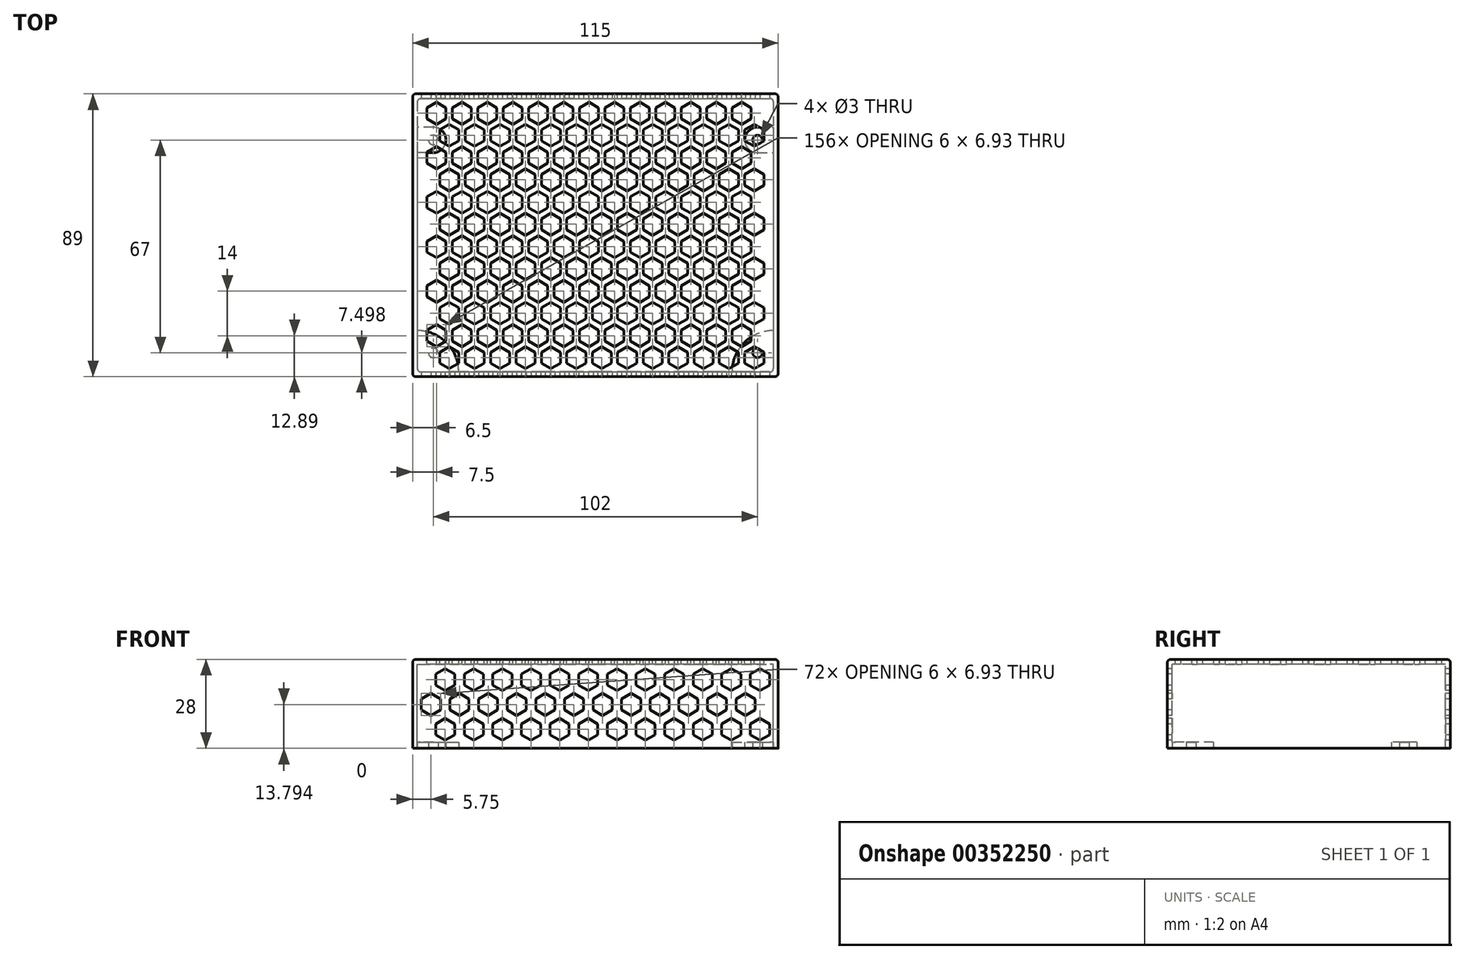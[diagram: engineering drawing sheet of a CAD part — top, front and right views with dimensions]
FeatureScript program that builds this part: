
annotation { "Feature Type Name" : "Feature", "Feature Type Description" : "" }
export const myFeature = defineFeature(function(context is Context, id is Id, definition is map)
    precondition{}
    {
        {
            var Q0;
            Q0=qCreatedBy(makeId("Top.planeOp"),FACE);
            var sketch = newSketch(context, id + "F0", { "sketchPlane" : qUnion([Q0])});
            skCircle(sketch, "E0.cCircle", {"center": v(-32, -14) * mm, "radius": 3 * mm, "construction": true});
            skLineSegment(sketch, "E0.0", {"start": v(-29, -15.73) * mm, "end": v(-32, -17.46) * mm});
            skLineSegment(sketch, "E0.1", {"start": v(-32, -17.46) * mm, "end": v(-35, -15.73) * mm});
            skLineSegment(sketch, "E0.2", {"start": v(-35, -15.73) * mm, "end": v(-35, -12.27) * mm});
            skLineSegment(sketch, "E0.3", {"start": v(-35, -12.27) * mm, "end": v(-32, -10.54) * mm});
            skLineSegment(sketch, "E0.4", {"start": v(-32, -10.54) * mm, "end": v(-29, -12.27) * mm});
            skLineSegment(sketch, "E0.5", {"start": v(-29, -12.27) * mm, "end": v(-29, -15.73) * mm});
            skPoint(sketch, "E0.0.midPoint", {"position": v(-30.5, -16.6) * mm});
            skCircle(sketch, "E1.cCircle", {"center": v(-28, -20.93) * mm, "radius": 3 * mm, "construction": true});
            skLineSegment(sketch, "E1.0", {"start": v(-25, -22.66) * mm, "end": v(-28, -24.4) * mm});
            skLineSegment(sketch, "E1.1", {"start": v(-28, -24.4) * mm, "end": v(-31, -22.66) * mm});
            skLineSegment(sketch, "E1.2", {"start": v(-31, -22.66) * mm, "end": v(-31, -19.2) * mm});
            skLineSegment(sketch, "E1.3", {"start": v(-31, -19.2) * mm, "end": v(-28, -17.46) * mm});
            skLineSegment(sketch, "E1.4", {"start": v(-28, -17.46) * mm, "end": v(-25, -19.2) * mm});
            skLineSegment(sketch, "E1.5", {"start": v(-25, -19.2) * mm, "end": v(-25, -22.66) * mm});
            skPoint(sketch, "E1.0.midPoint", {"position": v(-26.5, -23.53) * mm});
            skCircle(sketch, "E2.0.1.0", {"center": v(-28, -6.93) * mm, "radius": 3 * mm, "construction": true});
            skLineSegment(sketch, "E2.0.1.1", {"start": v(-28, -10.4) * mm, "end": v(-31, -8.66) * mm});
            skLineSegment(sketch, "E2.0.1.2", {"start": v(-31, -8.66) * mm, "end": v(-31, -5.2) * mm});
            skLineSegment(sketch, "E2.0.1.3", {"start": v(-31, -5.2) * mm, "end": v(-28, -3.46) * mm});
            skLineSegment(sketch, "E2.0.1.4", {"start": v(-28, -3.46) * mm, "end": v(-25, -5.2) * mm});
            skPoint(sketch, "E2.0.1.5", {"position": v(-26.5, -9.53) * mm});
            skPoint(sketch, "E2.0.1.6", {"position": v(-30.5, -2.6) * mm});
            skLineSegment(sketch, "E2.0.1.7", {"start": v(-25, -5.2) * mm, "end": v(-25, -8.66) * mm});
            skLineSegment(sketch, "E2.0.1.8", {"start": v(-29, 1.73) * mm, "end": v(-29, -1.73) * mm});
            skLineSegment(sketch, "E2.0.1.9", {"start": v(-32, 3.46) * mm, "end": v(-29, 1.73) * mm});
            skLineSegment(sketch, "E2.0.1.10", {"start": v(-35, 1.73) * mm, "end": v(-32, 3.46) * mm});
            skLineSegment(sketch, "E2.0.1.11", {"start": v(-35, -1.73) * mm, "end": v(-35, 1.73) * mm});
            skLineSegment(sketch, "E2.0.1.12", {"start": v(-32, -3.46) * mm, "end": v(-35, -1.73) * mm});
            skCircle(sketch, "E2.0.1.13", {"center": v(-32, 0) * mm, "radius": 3 * mm, "construction": true});
            skLineSegment(sketch, "E2.0.1.14", {"start": v(-25, -8.66) * mm, "end": v(-28, -10.4) * mm});
            skLineSegment(sketch, "E2.0.1.15", {"start": v(-29, -1.73) * mm, "end": v(-32, -3.46) * mm});
            skCircle(sketch, "E2.0.2.0", {"center": v(-28, 7.07) * mm, "radius": 3 * mm, "construction": true});
            skLineSegment(sketch, "E2.0.2.1", {"start": v(-28, 3.6) * mm, "end": v(-31, 5.34) * mm});
            skLineSegment(sketch, "E2.0.2.2", {"start": v(-31, 5.34) * mm, "end": v(-31, 8.8) * mm});
            skLineSegment(sketch, "E2.0.2.3", {"start": v(-31, 8.8) * mm, "end": v(-28, 10.54) * mm});
            skLineSegment(sketch, "E2.0.2.4", {"start": v(-28, 10.54) * mm, "end": v(-25, 8.8) * mm});
            skPoint(sketch, "E2.0.2.5", {"position": v(-26.5, 4.47) * mm});
            skPoint(sketch, "E2.0.2.6", {"position": v(-30.5, 11.4) * mm});
            skLineSegment(sketch, "E2.0.2.7", {"start": v(-25, 8.8) * mm, "end": v(-25, 5.34) * mm});
            skLineSegment(sketch, "E2.0.2.8", {"start": v(-29, 15.73) * mm, "end": v(-29, 12.27) * mm});
            skLineSegment(sketch, "E2.0.2.9", {"start": v(-32, 17.46) * mm, "end": v(-29, 15.73) * mm});
            skLineSegment(sketch, "E2.0.2.10", {"start": v(-35, 15.73) * mm, "end": v(-32, 17.46) * mm});
            skLineSegment(sketch, "E2.0.2.11", {"start": v(-35, 12.27) * mm, "end": v(-35, 15.73) * mm});
            skLineSegment(sketch, "E2.0.2.12", {"start": v(-32, 10.54) * mm, "end": v(-35, 12.27) * mm});
            skCircle(sketch, "E2.0.2.13", {"center": v(-32, 14) * mm, "radius": 3 * mm, "construction": true});
            skLineSegment(sketch, "E2.0.2.14", {"start": v(-25, 5.34) * mm, "end": v(-28, 3.6) * mm});
            skLineSegment(sketch, "E2.0.2.15", {"start": v(-29, 12.27) * mm, "end": v(-32, 10.54) * mm});
            skCircle(sketch, "E2.0.3.0", {"center": v(-28, 21.07) * mm, "radius": 3 * mm, "construction": true});
            skLineSegment(sketch, "E2.0.3.1", {"start": v(-28, 17.6) * mm, "end": v(-31, 19.34) * mm});
            skLineSegment(sketch, "E2.0.3.2", {"start": v(-31, 19.34) * mm, "end": v(-31, 22.8) * mm});
            skLineSegment(sketch, "E2.0.3.3", {"start": v(-31, 22.8) * mm, "end": v(-28, 24.54) * mm});
            skLineSegment(sketch, "E2.0.3.4", {"start": v(-28, 24.54) * mm, "end": v(-25, 22.8) * mm});
            skPoint(sketch, "E2.0.3.5", {"position": v(-26.5, 18.47) * mm});
            skPoint(sketch, "E2.0.3.6", {"position": v(-30.5, 25.4) * mm});
            skLineSegment(sketch, "E2.0.3.7", {"start": v(-25, 22.8) * mm, "end": v(-25, 19.34) * mm});
            skLineSegment(sketch, "E2.0.3.8", {"start": v(-29, 29.73) * mm, "end": v(-29, 26.27) * mm});
            skLineSegment(sketch, "E2.0.3.9", {"start": v(-32, 31.46) * mm, "end": v(-29, 29.73) * mm});
            skLineSegment(sketch, "E2.0.3.10", {"start": v(-35, 29.73) * mm, "end": v(-32, 31.46) * mm});
            skLineSegment(sketch, "E2.0.3.11", {"start": v(-35, 26.27) * mm, "end": v(-35, 29.73) * mm});
            skLineSegment(sketch, "E2.0.3.12", {"start": v(-32, 24.54) * mm, "end": v(-35, 26.27) * mm});
            skCircle(sketch, "E2.0.3.13", {"center": v(-32, 28) * mm, "radius": 3 * mm, "construction": true});
            skLineSegment(sketch, "E2.0.3.14", {"start": v(-25, 19.34) * mm, "end": v(-28, 17.6) * mm});
            skLineSegment(sketch, "E2.0.3.15", {"start": v(-29, 26.27) * mm, "end": v(-32, 24.54) * mm});
            skCircle(sketch, "E2.1.0.0", {"center": v(-20, -20.93) * mm, "radius": 3 * mm, "construction": true});
            skLineSegment(sketch, "E2.1.0.1", {"start": v(-20, -24.4) * mm, "end": v(-23, -22.66) * mm});
            skLineSegment(sketch, "E2.1.0.2", {"start": v(-23, -22.66) * mm, "end": v(-23, -19.2) * mm});
            skLineSegment(sketch, "E2.1.0.3", {"start": v(-23, -19.2) * mm, "end": v(-20, -17.46) * mm});
            skLineSegment(sketch, "E2.1.0.4", {"start": v(-20, -17.46) * mm, "end": v(-17, -19.2) * mm});
            skPoint(sketch, "E2.1.0.5", {"position": v(-18.5, -23.53) * mm});
            skPoint(sketch, "E2.1.0.6", {"position": v(-22.5, -16.6) * mm});
            skLineSegment(sketch, "E2.1.0.7", {"start": v(-17, -19.2) * mm, "end": v(-17, -22.66) * mm});
            skLineSegment(sketch, "E2.1.0.8", {"start": v(-21, -12.27) * mm, "end": v(-21, -15.73) * mm});
            skLineSegment(sketch, "E2.1.0.9", {"start": v(-24, -10.54) * mm, "end": v(-21, -12.27) * mm});
            skLineSegment(sketch, "E2.1.0.10", {"start": v(-27, -12.27) * mm, "end": v(-24, -10.54) * mm});
            skLineSegment(sketch, "E2.1.0.11", {"start": v(-27, -15.73) * mm, "end": v(-27, -12.27) * mm});
            skLineSegment(sketch, "E2.1.0.12", {"start": v(-24, -17.46) * mm, "end": v(-27, -15.73) * mm});
            skCircle(sketch, "E2.1.0.13", {"center": v(-24, -14) * mm, "radius": 3 * mm, "construction": true});
            skLineSegment(sketch, "E2.1.0.14", {"start": v(-17, -22.66) * mm, "end": v(-20, -24.4) * mm});
            skLineSegment(sketch, "E2.1.0.15", {"start": v(-21, -15.73) * mm, "end": v(-24, -17.46) * mm});
            skCircle(sketch, "E2.1.1.0", {"center": v(-20, -6.93) * mm, "radius": 3 * mm, "construction": true});
            skLineSegment(sketch, "E2.1.1.1", {"start": v(-20, -10.4) * mm, "end": v(-23, -8.66) * mm});
            skLineSegment(sketch, "E2.1.1.2", {"start": v(-23, -8.66) * mm, "end": v(-23, -5.2) * mm});
            skLineSegment(sketch, "E2.1.1.3", {"start": v(-23, -5.2) * mm, "end": v(-20, -3.46) * mm});
            skLineSegment(sketch, "E2.1.1.4", {"start": v(-20, -3.46) * mm, "end": v(-17, -5.2) * mm});
            skPoint(sketch, "E2.1.1.5", {"position": v(-18.5, -9.53) * mm});
            skPoint(sketch, "E2.1.1.6", {"position": v(-22.5, -2.6) * mm});
            skLineSegment(sketch, "E2.1.1.7", {"start": v(-17, -5.2) * mm, "end": v(-17, -8.66) * mm});
            skLineSegment(sketch, "E2.1.1.8", {"start": v(-21, 1.73) * mm, "end": v(-21, -1.73) * mm});
            skLineSegment(sketch, "E2.1.1.9", {"start": v(-24, 3.46) * mm, "end": v(-21, 1.73) * mm});
            skLineSegment(sketch, "E2.1.1.10", {"start": v(-27, 1.73) * mm, "end": v(-24, 3.46) * mm});
            skLineSegment(sketch, "E2.1.1.11", {"start": v(-27, -1.73) * mm, "end": v(-27, 1.73) * mm});
            skLineSegment(sketch, "E2.1.1.12", {"start": v(-24, -3.46) * mm, "end": v(-27, -1.73) * mm});
            skCircle(sketch, "E2.1.1.13", {"center": v(-24, 0) * mm, "radius": 3 * mm, "construction": true});
            skLineSegment(sketch, "E2.1.1.14", {"start": v(-17, -8.66) * mm, "end": v(-20, -10.4) * mm});
            skLineSegment(sketch, "E2.1.1.15", {"start": v(-21, -1.73) * mm, "end": v(-24, -3.46) * mm});
            skCircle(sketch, "E2.1.2.0", {"center": v(-20, 7.07) * mm, "radius": 3 * mm, "construction": true});
            skLineSegment(sketch, "E2.1.2.1", {"start": v(-20, 3.6) * mm, "end": v(-23, 5.34) * mm});
            skLineSegment(sketch, "E2.1.2.2", {"start": v(-23, 5.34) * mm, "end": v(-23, 8.8) * mm});
            skLineSegment(sketch, "E2.1.2.3", {"start": v(-23, 8.8) * mm, "end": v(-20, 10.54) * mm});
            skLineSegment(sketch, "E2.1.2.4", {"start": v(-20, 10.54) * mm, "end": v(-17, 8.8) * mm});
            skPoint(sketch, "E2.1.2.5", {"position": v(-18.5, 4.47) * mm});
            skPoint(sketch, "E2.1.2.6", {"position": v(-22.5, 11.4) * mm});
            skLineSegment(sketch, "E2.1.2.7", {"start": v(-17, 8.8) * mm, "end": v(-17, 5.34) * mm});
            skLineSegment(sketch, "E2.1.2.8", {"start": v(-21, 15.73) * mm, "end": v(-21, 12.27) * mm});
            skLineSegment(sketch, "E2.1.2.9", {"start": v(-24, 17.46) * mm, "end": v(-21, 15.73) * mm});
            skLineSegment(sketch, "E2.1.2.10", {"start": v(-27, 15.73) * mm, "end": v(-24, 17.46) * mm});
            skLineSegment(sketch, "E2.1.2.11", {"start": v(-27, 12.27) * mm, "end": v(-27, 15.73) * mm});
            skLineSegment(sketch, "E2.1.2.12", {"start": v(-24, 10.54) * mm, "end": v(-27, 12.27) * mm});
            skCircle(sketch, "E2.1.2.13", {"center": v(-24, 14) * mm, "radius": 3 * mm, "construction": true});
            skLineSegment(sketch, "E2.1.2.14", {"start": v(-17, 5.34) * mm, "end": v(-20, 3.6) * mm});
            skLineSegment(sketch, "E2.1.2.15", {"start": v(-21, 12.27) * mm, "end": v(-24, 10.54) * mm});
            skCircle(sketch, "E2.1.3.0", {"center": v(-20, 21.07) * mm, "radius": 3 * mm, "construction": true});
            skLineSegment(sketch, "E2.1.3.1", {"start": v(-20, 17.6) * mm, "end": v(-23, 19.34) * mm});
            skLineSegment(sketch, "E2.1.3.2", {"start": v(-23, 19.34) * mm, "end": v(-23, 22.8) * mm});
            skLineSegment(sketch, "E2.1.3.3", {"start": v(-23, 22.8) * mm, "end": v(-20, 24.54) * mm});
            skLineSegment(sketch, "E2.1.3.4", {"start": v(-20, 24.54) * mm, "end": v(-17, 22.8) * mm});
            skPoint(sketch, "E2.1.3.5", {"position": v(-18.5, 18.47) * mm});
            skPoint(sketch, "E2.1.3.6", {"position": v(-22.5, 25.4) * mm});
            skLineSegment(sketch, "E2.1.3.7", {"start": v(-17, 22.8) * mm, "end": v(-17, 19.34) * mm});
            skLineSegment(sketch, "E2.1.3.8", {"start": v(-21, 29.73) * mm, "end": v(-21, 26.27) * mm});
            skLineSegment(sketch, "E2.1.3.9", {"start": v(-24, 31.46) * mm, "end": v(-21, 29.73) * mm});
            skLineSegment(sketch, "E2.1.3.10", {"start": v(-27, 29.73) * mm, "end": v(-24, 31.46) * mm});
            skLineSegment(sketch, "E2.1.3.11", {"start": v(-27, 26.27) * mm, "end": v(-27, 29.73) * mm});
            skLineSegment(sketch, "E2.1.3.12", {"start": v(-24, 24.54) * mm, "end": v(-27, 26.27) * mm});
            skCircle(sketch, "E2.1.3.13", {"center": v(-24, 28) * mm, "radius": 3 * mm, "construction": true});
            skLineSegment(sketch, "E2.1.3.14", {"start": v(-17, 19.34) * mm, "end": v(-20, 17.6) * mm});
            skLineSegment(sketch, "E2.1.3.15", {"start": v(-21, 26.27) * mm, "end": v(-24, 24.54) * mm});
            skCircle(sketch, "E2.2.0.0", {"center": v(-12, -20.93) * mm, "radius": 3 * mm, "construction": true});
            skLineSegment(sketch, "E2.2.0.1", {"start": v(-12, -24.4) * mm, "end": v(-15, -22.66) * mm});
            skLineSegment(sketch, "E2.2.0.2", {"start": v(-15, -22.66) * mm, "end": v(-15, -19.2) * mm});
            skLineSegment(sketch, "E2.2.0.3", {"start": v(-15, -19.2) * mm, "end": v(-12, -17.46) * mm});
            skLineSegment(sketch, "E2.2.0.4", {"start": v(-12, -17.46) * mm, "end": v(-9, -19.2) * mm});
            skPoint(sketch, "E2.2.0.5", {"position": v(-10.5, -23.53) * mm});
            skPoint(sketch, "E2.2.0.6", {"position": v(-14.5, -16.6) * mm});
            skLineSegment(sketch, "E2.2.0.7", {"start": v(-9, -19.2) * mm, "end": v(-9, -22.66) * mm});
            skLineSegment(sketch, "E2.2.0.8", {"start": v(-13, -12.27) * mm, "end": v(-13, -15.73) * mm});
            skLineSegment(sketch, "E2.2.0.9", {"start": v(-16, -10.54) * mm, "end": v(-13, -12.27) * mm});
            skLineSegment(sketch, "E2.2.0.10", {"start": v(-19, -12.27) * mm, "end": v(-16, -10.54) * mm});
            skLineSegment(sketch, "E2.2.0.11", {"start": v(-19, -15.73) * mm, "end": v(-19, -12.27) * mm});
            skLineSegment(sketch, "E2.2.0.12", {"start": v(-16, -17.46) * mm, "end": v(-19, -15.73) * mm});
            skCircle(sketch, "E2.2.0.13", {"center": v(-16, -14) * mm, "radius": 3 * mm, "construction": true});
            skLineSegment(sketch, "E2.2.0.14", {"start": v(-9, -22.66) * mm, "end": v(-12, -24.4) * mm});
            skLineSegment(sketch, "E2.2.0.15", {"start": v(-13, -15.73) * mm, "end": v(-16, -17.46) * mm});
            skCircle(sketch, "E2.2.1.0", {"center": v(-12, -6.93) * mm, "radius": 3 * mm, "construction": true});
            skLineSegment(sketch, "E2.2.1.1", {"start": v(-12, -10.4) * mm, "end": v(-15, -8.66) * mm});
            skLineSegment(sketch, "E2.2.1.2", {"start": v(-15, -8.66) * mm, "end": v(-15, -5.2) * mm});
            skLineSegment(sketch, "E2.2.1.3", {"start": v(-15, -5.2) * mm, "end": v(-12, -3.46) * mm});
            skLineSegment(sketch, "E2.2.1.4", {"start": v(-12, -3.46) * mm, "end": v(-9, -5.2) * mm});
            skPoint(sketch, "E2.2.1.5", {"position": v(-10.5, -9.53) * mm});
            skPoint(sketch, "E2.2.1.6", {"position": v(-14.5, -2.6) * mm});
            skLineSegment(sketch, "E2.2.1.7", {"start": v(-9, -5.2) * mm, "end": v(-9, -8.66) * mm});
            skLineSegment(sketch, "E2.2.1.8", {"start": v(-13, 1.73) * mm, "end": v(-13, -1.73) * mm});
            skLineSegment(sketch, "E2.2.1.9", {"start": v(-16, 3.46) * mm, "end": v(-13, 1.73) * mm});
            skLineSegment(sketch, "E2.2.1.10", {"start": v(-19, 1.73) * mm, "end": v(-16, 3.46) * mm});
            skLineSegment(sketch, "E2.2.1.11", {"start": v(-19, -1.73) * mm, "end": v(-19, 1.73) * mm});
            skLineSegment(sketch, "E2.2.1.12", {"start": v(-16, -3.46) * mm, "end": v(-19, -1.73) * mm});
            skCircle(sketch, "E2.2.1.13", {"center": v(-16, 0) * mm, "radius": 3 * mm, "construction": true});
            skLineSegment(sketch, "E2.2.1.14", {"start": v(-9, -8.66) * mm, "end": v(-12, -10.4) * mm});
            skLineSegment(sketch, "E2.2.1.15", {"start": v(-13, -1.73) * mm, "end": v(-16, -3.46) * mm});
            skCircle(sketch, "E2.2.2.0", {"center": v(-12, 7.07) * mm, "radius": 3 * mm, "construction": true});
            skLineSegment(sketch, "E2.2.2.1", {"start": v(-12, 3.6) * mm, "end": v(-15, 5.34) * mm});
            skLineSegment(sketch, "E2.2.2.2", {"start": v(-15, 5.34) * mm, "end": v(-15, 8.8) * mm});
            skLineSegment(sketch, "E2.2.2.3", {"start": v(-15, 8.8) * mm, "end": v(-12, 10.54) * mm});
            skLineSegment(sketch, "E2.2.2.4", {"start": v(-12, 10.54) * mm, "end": v(-9, 8.8) * mm});
            skPoint(sketch, "E2.2.2.5", {"position": v(-10.5, 4.47) * mm});
            skPoint(sketch, "E2.2.2.6", {"position": v(-14.5, 11.4) * mm});
            skLineSegment(sketch, "E2.2.2.7", {"start": v(-9, 8.8) * mm, "end": v(-9, 5.34) * mm});
            skLineSegment(sketch, "E2.2.2.8", {"start": v(-13, 15.73) * mm, "end": v(-13, 12.27) * mm});
            skLineSegment(sketch, "E2.2.2.9", {"start": v(-16, 17.46) * mm, "end": v(-13, 15.73) * mm});
            skLineSegment(sketch, "E2.2.2.10", {"start": v(-19, 15.73) * mm, "end": v(-16, 17.46) * mm});
            skLineSegment(sketch, "E2.2.2.11", {"start": v(-19, 12.27) * mm, "end": v(-19, 15.73) * mm});
            skLineSegment(sketch, "E2.2.2.12", {"start": v(-16, 10.54) * mm, "end": v(-19, 12.27) * mm});
            skCircle(sketch, "E2.2.2.13", {"center": v(-16, 14) * mm, "radius": 3 * mm, "construction": true});
            skLineSegment(sketch, "E2.2.2.14", {"start": v(-9, 5.34) * mm, "end": v(-12, 3.6) * mm});
            skLineSegment(sketch, "E2.2.2.15", {"start": v(-13, 12.27) * mm, "end": v(-16, 10.54) * mm});
            skCircle(sketch, "E2.2.3.0", {"center": v(-12, 21.07) * mm, "radius": 3 * mm, "construction": true});
            skLineSegment(sketch, "E2.2.3.1", {"start": v(-12, 17.6) * mm, "end": v(-15, 19.34) * mm});
            skLineSegment(sketch, "E2.2.3.2", {"start": v(-15, 19.34) * mm, "end": v(-15, 22.8) * mm});
            skLineSegment(sketch, "E2.2.3.3", {"start": v(-15, 22.8) * mm, "end": v(-12, 24.54) * mm});
            skLineSegment(sketch, "E2.2.3.4", {"start": v(-12, 24.54) * mm, "end": v(-9, 22.8) * mm});
            skPoint(sketch, "E2.2.3.5", {"position": v(-10.5, 18.47) * mm});
            skPoint(sketch, "E2.2.3.6", {"position": v(-14.5, 25.4) * mm});
            skLineSegment(sketch, "E2.2.3.7", {"start": v(-9, 22.8) * mm, "end": v(-9, 19.34) * mm});
            skLineSegment(sketch, "E2.2.3.8", {"start": v(-13, 29.73) * mm, "end": v(-13, 26.27) * mm});
            skLineSegment(sketch, "E2.2.3.9", {"start": v(-16, 31.46) * mm, "end": v(-13, 29.73) * mm});
            skLineSegment(sketch, "E2.2.3.10", {"start": v(-19, 29.73) * mm, "end": v(-16, 31.46) * mm});
            skLineSegment(sketch, "E2.2.3.11", {"start": v(-19, 26.27) * mm, "end": v(-19, 29.73) * mm});
            skLineSegment(sketch, "E2.2.3.12", {"start": v(-16, 24.54) * mm, "end": v(-19, 26.27) * mm});
            skCircle(sketch, "E2.2.3.13", {"center": v(-16, 28) * mm, "radius": 3 * mm, "construction": true});
            skLineSegment(sketch, "E2.2.3.14", {"start": v(-9, 19.34) * mm, "end": v(-12, 17.6) * mm});
            skLineSegment(sketch, "E2.2.3.15", {"start": v(-13, 26.27) * mm, "end": v(-16, 24.54) * mm});
            skCircle(sketch, "E2.3.0.0", {"center": v(-4, -20.93) * mm, "radius": 3 * mm, "construction": true});
            skLineSegment(sketch, "E2.3.0.1", {"start": v(-4, -24.4) * mm, "end": v(-7, -22.66) * mm});
            skLineSegment(sketch, "E2.3.0.2", {"start": v(-7, -22.66) * mm, "end": v(-7, -19.2) * mm});
            skLineSegment(sketch, "E2.3.0.3", {"start": v(-7, -19.2) * mm, "end": v(-4, -17.46) * mm});
            skLineSegment(sketch, "E2.3.0.4", {"start": v(-4, -17.46) * mm, "end": v(-1, -19.2) * mm});
            skPoint(sketch, "E2.3.0.5", {"position": v(-2.5, -23.53) * mm});
            skPoint(sketch, "E2.3.0.6", {"position": v(-6.5, -16.6) * mm});
            skLineSegment(sketch, "E2.3.0.7", {"start": v(-1, -19.2) * mm, "end": v(-1, -22.66) * mm});
            skLineSegment(sketch, "E2.3.0.8", {"start": v(-5, -12.27) * mm, "end": v(-5, -15.73) * mm});
            skLineSegment(sketch, "E2.3.0.9", {"start": v(-8, -10.54) * mm, "end": v(-5, -12.27) * mm});
            skLineSegment(sketch, "E2.3.0.10", {"start": v(-11, -12.27) * mm, "end": v(-8, -10.54) * mm});
            skLineSegment(sketch, "E2.3.0.11", {"start": v(-11, -15.73) * mm, "end": v(-11, -12.27) * mm});
            skLineSegment(sketch, "E2.3.0.12", {"start": v(-8, -17.46) * mm, "end": v(-11, -15.73) * mm});
            skCircle(sketch, "E2.3.0.13", {"center": v(-8, -14) * mm, "radius": 3 * mm, "construction": true});
            skLineSegment(sketch, "E2.3.0.14", {"start": v(-1, -22.66) * mm, "end": v(-4, -24.4) * mm});
            skLineSegment(sketch, "E2.3.0.15", {"start": v(-5, -15.73) * mm, "end": v(-8, -17.46) * mm});
            skCircle(sketch, "E2.3.1.0", {"center": v(-4, -6.93) * mm, "radius": 3 * mm, "construction": true});
            skLineSegment(sketch, "E2.3.1.1", {"start": v(-4, -10.4) * mm, "end": v(-7, -8.66) * mm});
            skLineSegment(sketch, "E2.3.1.2", {"start": v(-7, -8.66) * mm, "end": v(-7, -5.2) * mm});
            skLineSegment(sketch, "E2.3.1.3", {"start": v(-7, -5.2) * mm, "end": v(-4, -3.46) * mm});
            skLineSegment(sketch, "E2.3.1.4", {"start": v(-4, -3.46) * mm, "end": v(-1, -5.2) * mm});
            skPoint(sketch, "E2.3.1.5", {"position": v(-2.5, -9.53) * mm});
            skPoint(sketch, "E2.3.1.6", {"position": v(-6.5, -2.6) * mm});
            skLineSegment(sketch, "E2.3.1.7", {"start": v(-1, -5.2) * mm, "end": v(-1, -8.66) * mm});
            skLineSegment(sketch, "E2.3.1.8", {"start": v(-5, 1.73) * mm, "end": v(-5, -1.73) * mm});
            skLineSegment(sketch, "E2.3.1.9", {"start": v(-8, 3.46) * mm, "end": v(-5, 1.73) * mm});
            skLineSegment(sketch, "E2.3.1.10", {"start": v(-11, 1.73) * mm, "end": v(-8, 3.46) * mm});
            skLineSegment(sketch, "E2.3.1.11", {"start": v(-11, -1.73) * mm, "end": v(-11, 1.73) * mm});
            skLineSegment(sketch, "E2.3.1.12", {"start": v(-8, -3.46) * mm, "end": v(-11, -1.73) * mm});
            skCircle(sketch, "E2.3.1.13", {"center": v(-8, 0) * mm, "radius": 3 * mm, "construction": true});
            skLineSegment(sketch, "E2.3.1.14", {"start": v(-1, -8.66) * mm, "end": v(-4, -10.4) * mm});
            skLineSegment(sketch, "E2.3.1.15", {"start": v(-5, -1.73) * mm, "end": v(-8, -3.46) * mm});
            skCircle(sketch, "E2.3.2.0", {"center": v(-4, 7.07) * mm, "radius": 3 * mm, "construction": true});
            skLineSegment(sketch, "E2.3.2.1", {"start": v(-4, 3.6) * mm, "end": v(-7, 5.34) * mm});
            skLineSegment(sketch, "E2.3.2.2", {"start": v(-7, 5.34) * mm, "end": v(-7, 8.8) * mm});
            skLineSegment(sketch, "E2.3.2.3", {"start": v(-7, 8.8) * mm, "end": v(-4, 10.54) * mm});
            skLineSegment(sketch, "E2.3.2.4", {"start": v(-4, 10.54) * mm, "end": v(-1, 8.8) * mm});
            skPoint(sketch, "E2.3.2.5", {"position": v(-2.5, 4.47) * mm});
            skPoint(sketch, "E2.3.2.6", {"position": v(-6.5, 11.4) * mm});
            skLineSegment(sketch, "E2.3.2.7", {"start": v(-1, 8.8) * mm, "end": v(-1, 5.34) * mm});
            skLineSegment(sketch, "E2.3.2.8", {"start": v(-5, 15.73) * mm, "end": v(-5, 12.27) * mm});
            skLineSegment(sketch, "E2.3.2.9", {"start": v(-8, 17.46) * mm, "end": v(-5, 15.73) * mm});
            skLineSegment(sketch, "E2.3.2.10", {"start": v(-11, 15.73) * mm, "end": v(-8, 17.46) * mm});
            skLineSegment(sketch, "E2.3.2.11", {"start": v(-11, 12.27) * mm, "end": v(-11, 15.73) * mm});
            skLineSegment(sketch, "E2.3.2.12", {"start": v(-8, 10.54) * mm, "end": v(-11, 12.27) * mm});
            skCircle(sketch, "E2.3.2.13", {"center": v(-8, 14) * mm, "radius": 3 * mm, "construction": true});
            skLineSegment(sketch, "E2.3.2.14", {"start": v(-1, 5.34) * mm, "end": v(-4, 3.6) * mm});
            skLineSegment(sketch, "E2.3.2.15", {"start": v(-5, 12.27) * mm, "end": v(-8, 10.54) * mm});
            skCircle(sketch, "E2.3.3.0", {"center": v(-4, 21.07) * mm, "radius": 3 * mm, "construction": true});
            skLineSegment(sketch, "E2.3.3.1", {"start": v(-4, 17.6) * mm, "end": v(-7, 19.34) * mm});
            skLineSegment(sketch, "E2.3.3.2", {"start": v(-7, 19.34) * mm, "end": v(-7, 22.8) * mm});
            skLineSegment(sketch, "E2.3.3.3", {"start": v(-7, 22.8) * mm, "end": v(-4, 24.54) * mm});
            skLineSegment(sketch, "E2.3.3.4", {"start": v(-4, 24.54) * mm, "end": v(-1, 22.8) * mm});
            skPoint(sketch, "E2.3.3.5", {"position": v(-2.5, 18.47) * mm});
            skPoint(sketch, "E2.3.3.6", {"position": v(-6.5, 25.4) * mm});
            skLineSegment(sketch, "E2.3.3.7", {"start": v(-1, 22.8) * mm, "end": v(-1, 19.34) * mm});
            skLineSegment(sketch, "E2.3.3.8", {"start": v(-5, 29.73) * mm, "end": v(-5, 26.27) * mm});
            skLineSegment(sketch, "E2.3.3.9", {"start": v(-8, 31.46) * mm, "end": v(-5, 29.73) * mm});
            skLineSegment(sketch, "E2.3.3.10", {"start": v(-11, 29.73) * mm, "end": v(-8, 31.46) * mm});
            skLineSegment(sketch, "E2.3.3.11", {"start": v(-11, 26.27) * mm, "end": v(-11, 29.73) * mm});
            skLineSegment(sketch, "E2.3.3.12", {"start": v(-8, 24.54) * mm, "end": v(-11, 26.27) * mm});
            skCircle(sketch, "E2.3.3.13", {"center": v(-8, 28) * mm, "radius": 3 * mm, "construction": true});
            skLineSegment(sketch, "E2.3.3.14", {"start": v(-1, 19.34) * mm, "end": v(-4, 17.6) * mm});
            skLineSegment(sketch, "E2.3.3.15", {"start": v(-5, 26.27) * mm, "end": v(-8, 24.54) * mm});
            skCircle(sketch, "E2.4.0.0", {"center": v(4, -20.93) * mm, "radius": 3 * mm, "construction": true});
            skLineSegment(sketch, "E2.4.0.1", {"start": v(4, -24.4) * mm, "end": v(1, -22.66) * mm});
            skLineSegment(sketch, "E2.4.0.2", {"start": v(1, -22.66) * mm, "end": v(1, -19.2) * mm});
            skLineSegment(sketch, "E2.4.0.3", {"start": v(1, -19.2) * mm, "end": v(4, -17.46) * mm});
            skLineSegment(sketch, "E2.4.0.4", {"start": v(4, -17.46) * mm, "end": v(7, -19.2) * mm});
            skPoint(sketch, "E2.4.0.5", {"position": v(5.5, -23.53) * mm});
            skPoint(sketch, "E2.4.0.6", {"position": v(1.5, -16.6) * mm});
            skLineSegment(sketch, "E2.4.0.7", {"start": v(7, -19.2) * mm, "end": v(7, -22.66) * mm});
            skLineSegment(sketch, "E2.4.0.8", {"start": v(3, -12.27) * mm, "end": v(3, -15.73) * mm});
            skLineSegment(sketch, "E2.4.0.9", {"start": v(0, -10.54) * mm, "end": v(3, -12.27) * mm});
            skLineSegment(sketch, "E2.4.0.10", {"start": v(-3, -12.27) * mm, "end": v(0, -10.54) * mm});
            skLineSegment(sketch, "E2.4.0.11", {"start": v(-3, -15.73) * mm, "end": v(-3, -12.27) * mm});
            skLineSegment(sketch, "E2.4.0.12", {"start": v(0, -17.46) * mm, "end": v(-3, -15.73) * mm});
            skCircle(sketch, "E2.4.0.13", {"center": v(0, -14) * mm, "radius": 3 * mm, "construction": true});
            skLineSegment(sketch, "E2.4.0.14", {"start": v(7, -22.66) * mm, "end": v(4, -24.4) * mm});
            skLineSegment(sketch, "E2.4.0.15", {"start": v(3, -15.73) * mm, "end": v(0, -17.46) * mm});
            skCircle(sketch, "E2.4.1.0", {"center": v(4, -6.93) * mm, "radius": 3 * mm, "construction": true});
            skLineSegment(sketch, "E2.4.1.1", {"start": v(4, -10.4) * mm, "end": v(1, -8.66) * mm});
            skLineSegment(sketch, "E2.4.1.2", {"start": v(1, -8.66) * mm, "end": v(1, -5.2) * mm});
            skLineSegment(sketch, "E2.4.1.3", {"start": v(1, -5.2) * mm, "end": v(4, -3.46) * mm});
            skLineSegment(sketch, "E2.4.1.4", {"start": v(4, -3.46) * mm, "end": v(7, -5.2) * mm});
            skPoint(sketch, "E2.4.1.5", {"position": v(5.5, -9.53) * mm});
            skPoint(sketch, "E2.4.1.6", {"position": v(1.5, -2.6) * mm});
            skLineSegment(sketch, "E2.4.1.7", {"start": v(7, -5.2) * mm, "end": v(7, -8.66) * mm});
            skLineSegment(sketch, "E2.4.1.8", {"start": v(3, 1.73) * mm, "end": v(3, -1.73) * mm});
            skLineSegment(sketch, "E2.4.1.9", {"start": v(0, 3.46) * mm, "end": v(3, 1.73) * mm});
            skLineSegment(sketch, "E2.4.1.10", {"start": v(-3, 1.73) * mm, "end": v(0, 3.46) * mm});
            skLineSegment(sketch, "E2.4.1.11", {"start": v(-3, -1.73) * mm, "end": v(-3, 1.73) * mm});
            skLineSegment(sketch, "E2.4.1.12", {"start": v(0, -3.46) * mm, "end": v(-3, -1.73) * mm});
            skCircle(sketch, "E2.4.1.13", {"center": v(0, 0) * mm, "radius": 3 * mm, "construction": true});
            skLineSegment(sketch, "E2.4.1.14", {"start": v(7, -8.66) * mm, "end": v(4, -10.4) * mm});
            skLineSegment(sketch, "E2.4.1.15", {"start": v(3, -1.73) * mm, "end": v(0, -3.46) * mm});
            skCircle(sketch, "E2.4.2.0", {"center": v(4, 7.07) * mm, "radius": 3 * mm, "construction": true});
            skLineSegment(sketch, "E2.4.2.1", {"start": v(4, 3.6) * mm, "end": v(1, 5.34) * mm});
            skLineSegment(sketch, "E2.4.2.2", {"start": v(1, 5.34) * mm, "end": v(1, 8.8) * mm});
            skLineSegment(sketch, "E2.4.2.3", {"start": v(1, 8.8) * mm, "end": v(4, 10.54) * mm});
            skLineSegment(sketch, "E2.4.2.4", {"start": v(4, 10.54) * mm, "end": v(7, 8.8) * mm});
            skPoint(sketch, "E2.4.2.5", {"position": v(5.5, 4.47) * mm});
            skPoint(sketch, "E2.4.2.6", {"position": v(1.5, 11.4) * mm});
            skLineSegment(sketch, "E2.4.2.7", {"start": v(7, 8.8) * mm, "end": v(7, 5.34) * mm});
            skLineSegment(sketch, "E2.4.2.8", {"start": v(3, 15.73) * mm, "end": v(3, 12.27) * mm});
            skLineSegment(sketch, "E2.4.2.9", {"start": v(0, 17.46) * mm, "end": v(3, 15.73) * mm});
            skLineSegment(sketch, "E2.4.2.10", {"start": v(-3, 15.73) * mm, "end": v(0, 17.46) * mm});
            skLineSegment(sketch, "E2.4.2.11", {"start": v(-3, 12.27) * mm, "end": v(-3, 15.73) * mm});
            skLineSegment(sketch, "E2.4.2.12", {"start": v(0, 10.54) * mm, "end": v(-3, 12.27) * mm});
            skCircle(sketch, "E2.4.2.13", {"center": v(0, 14) * mm, "radius": 3 * mm, "construction": true});
            skLineSegment(sketch, "E2.4.2.14", {"start": v(7, 5.34) * mm, "end": v(4, 3.6) * mm});
            skLineSegment(sketch, "E2.4.2.15", {"start": v(3, 12.27) * mm, "end": v(0, 10.54) * mm});
            skCircle(sketch, "E2.4.3.0", {"center": v(4, 21.07) * mm, "radius": 3 * mm, "construction": true});
            skLineSegment(sketch, "E2.4.3.1", {"start": v(4, 17.6) * mm, "end": v(1, 19.34) * mm});
            skLineSegment(sketch, "E2.4.3.2", {"start": v(1, 19.34) * mm, "end": v(1, 22.8) * mm});
            skLineSegment(sketch, "E2.4.3.3", {"start": v(1, 22.8) * mm, "end": v(4, 24.54) * mm});
            skLineSegment(sketch, "E2.4.3.4", {"start": v(4, 24.54) * mm, "end": v(7, 22.8) * mm});
            skPoint(sketch, "E2.4.3.5", {"position": v(5.5, 18.47) * mm});
            skPoint(sketch, "E2.4.3.6", {"position": v(1.5, 25.4) * mm});
            skLineSegment(sketch, "E2.4.3.7", {"start": v(7, 22.8) * mm, "end": v(7, 19.34) * mm});
            skLineSegment(sketch, "E2.4.3.8", {"start": v(3, 29.73) * mm, "end": v(3, 26.27) * mm});
            skLineSegment(sketch, "E2.4.3.9", {"start": v(0, 31.46) * mm, "end": v(3, 29.73) * mm});
            skLineSegment(sketch, "E2.4.3.10", {"start": v(-3, 29.73) * mm, "end": v(0, 31.46) * mm});
            skLineSegment(sketch, "E2.4.3.11", {"start": v(-3, 26.27) * mm, "end": v(-3, 29.73) * mm});
            skLineSegment(sketch, "E2.4.3.12", {"start": v(0, 24.54) * mm, "end": v(-3, 26.27) * mm});
            skCircle(sketch, "E2.4.3.13", {"center": v(0, 28) * mm, "radius": 3 * mm, "construction": true});
            skLineSegment(sketch, "E2.4.3.14", {"start": v(7, 19.34) * mm, "end": v(4, 17.6) * mm});
            skLineSegment(sketch, "E2.4.3.15", {"start": v(3, 26.27) * mm, "end": v(0, 24.54) * mm});
            skCircle(sketch, "E2.5.0.0", {"center": v(12, -20.93) * mm, "radius": 3 * mm, "construction": true});
            skLineSegment(sketch, "E2.5.0.1", {"start": v(12, -24.4) * mm, "end": v(9, -22.66) * mm});
            skLineSegment(sketch, "E2.5.0.2", {"start": v(9, -22.66) * mm, "end": v(9, -19.2) * mm});
            skLineSegment(sketch, "E2.5.0.3", {"start": v(9, -19.2) * mm, "end": v(12, -17.46) * mm});
            skLineSegment(sketch, "E2.5.0.4", {"start": v(12, -17.46) * mm, "end": v(15, -19.2) * mm});
            skPoint(sketch, "E2.5.0.5", {"position": v(13.5, -23.53) * mm});
            skPoint(sketch, "E2.5.0.6", {"position": v(9.5, -16.6) * mm});
            skLineSegment(sketch, "E2.5.0.7", {"start": v(15, -19.2) * mm, "end": v(15, -22.66) * mm});
            skLineSegment(sketch, "E2.5.0.8", {"start": v(11, -12.27) * mm, "end": v(11, -15.73) * mm});
            skLineSegment(sketch, "E2.5.0.9", {"start": v(8, -10.54) * mm, "end": v(11, -12.27) * mm});
            skLineSegment(sketch, "E2.5.0.10", {"start": v(5, -12.27) * mm, "end": v(8, -10.54) * mm});
            skLineSegment(sketch, "E2.5.0.11", {"start": v(5, -15.73) * mm, "end": v(5, -12.27) * mm});
            skLineSegment(sketch, "E2.5.0.12", {"start": v(8, -17.46) * mm, "end": v(5, -15.73) * mm});
            skCircle(sketch, "E2.5.0.13", {"center": v(8, -14) * mm, "radius": 3 * mm, "construction": true});
            skLineSegment(sketch, "E2.5.0.14", {"start": v(15, -22.66) * mm, "end": v(12, -24.4) * mm});
            skLineSegment(sketch, "E2.5.0.15", {"start": v(11, -15.73) * mm, "end": v(8, -17.46) * mm});
            skCircle(sketch, "E2.5.1.0", {"center": v(12, -6.93) * mm, "radius": 3 * mm, "construction": true});
            skLineSegment(sketch, "E2.5.1.1", {"start": v(12, -10.4) * mm, "end": v(9, -8.66) * mm});
            skLineSegment(sketch, "E2.5.1.2", {"start": v(9, -8.66) * mm, "end": v(9, -5.2) * mm});
            skLineSegment(sketch, "E2.5.1.3", {"start": v(9, -5.2) * mm, "end": v(12, -3.46) * mm});
            skLineSegment(sketch, "E2.5.1.4", {"start": v(12, -3.46) * mm, "end": v(15, -5.2) * mm});
            skPoint(sketch, "E2.5.1.5", {"position": v(13.5, -9.53) * mm});
            skPoint(sketch, "E2.5.1.6", {"position": v(9.5, -2.6) * mm});
            skLineSegment(sketch, "E2.5.1.7", {"start": v(15, -5.2) * mm, "end": v(15, -8.66) * mm});
            skLineSegment(sketch, "E2.5.1.8", {"start": v(11, 1.73) * mm, "end": v(11, -1.73) * mm});
            skLineSegment(sketch, "E2.5.1.9", {"start": v(8, 3.46) * mm, "end": v(11, 1.73) * mm});
            skLineSegment(sketch, "E2.5.1.10", {"start": v(5, 1.73) * mm, "end": v(8, 3.46) * mm});
            skLineSegment(sketch, "E2.5.1.11", {"start": v(5, -1.73) * mm, "end": v(5, 1.73) * mm});
            skLineSegment(sketch, "E2.5.1.12", {"start": v(8, -3.46) * mm, "end": v(5, -1.73) * mm});
            skCircle(sketch, "E2.5.1.13", {"center": v(8, 0) * mm, "radius": 3 * mm, "construction": true});
            skLineSegment(sketch, "E2.5.1.14", {"start": v(15, -8.66) * mm, "end": v(12, -10.4) * mm});
            skLineSegment(sketch, "E2.5.1.15", {"start": v(11, -1.73) * mm, "end": v(8, -3.46) * mm});
            skCircle(sketch, "E2.5.2.0", {"center": v(12, 7.07) * mm, "radius": 3 * mm, "construction": true});
            skLineSegment(sketch, "E2.5.2.1", {"start": v(12, 3.6) * mm, "end": v(9, 5.34) * mm});
            skLineSegment(sketch, "E2.5.2.2", {"start": v(9, 5.34) * mm, "end": v(9, 8.8) * mm});
            skLineSegment(sketch, "E2.5.2.3", {"start": v(9, 8.8) * mm, "end": v(12, 10.54) * mm});
            skLineSegment(sketch, "E2.5.2.4", {"start": v(12, 10.54) * mm, "end": v(15, 8.8) * mm});
            skPoint(sketch, "E2.5.2.5", {"position": v(13.5, 4.47) * mm});
            skPoint(sketch, "E2.5.2.6", {"position": v(9.5, 11.4) * mm});
            skLineSegment(sketch, "E2.5.2.7", {"start": v(15, 8.8) * mm, "end": v(15, 5.34) * mm});
            skLineSegment(sketch, "E2.5.2.8", {"start": v(11, 15.73) * mm, "end": v(11, 12.27) * mm});
            skLineSegment(sketch, "E2.5.2.9", {"start": v(8, 17.46) * mm, "end": v(11, 15.73) * mm});
            skLineSegment(sketch, "E2.5.2.10", {"start": v(5, 15.73) * mm, "end": v(8, 17.46) * mm});
            skLineSegment(sketch, "E2.5.2.11", {"start": v(5, 12.27) * mm, "end": v(5, 15.73) * mm});
            skLineSegment(sketch, "E2.5.2.12", {"start": v(8, 10.54) * mm, "end": v(5, 12.27) * mm});
            skCircle(sketch, "E2.5.2.13", {"center": v(8, 14) * mm, "radius": 3 * mm, "construction": true});
            skLineSegment(sketch, "E2.5.2.14", {"start": v(15, 5.34) * mm, "end": v(12, 3.6) * mm});
            skLineSegment(sketch, "E2.5.2.15", {"start": v(11, 12.27) * mm, "end": v(8, 10.54) * mm});
            skCircle(sketch, "E2.5.3.0", {"center": v(12, 21.07) * mm, "radius": 3 * mm, "construction": true});
            skLineSegment(sketch, "E2.5.3.1", {"start": v(12, 17.6) * mm, "end": v(9, 19.34) * mm});
            skLineSegment(sketch, "E2.5.3.2", {"start": v(9, 19.34) * mm, "end": v(9, 22.8) * mm});
            skLineSegment(sketch, "E2.5.3.3", {"start": v(9, 22.8) * mm, "end": v(12, 24.54) * mm});
            skLineSegment(sketch, "E2.5.3.4", {"start": v(12, 24.54) * mm, "end": v(15, 22.8) * mm});
            skPoint(sketch, "E2.5.3.5", {"position": v(13.5, 18.47) * mm});
            skPoint(sketch, "E2.5.3.6", {"position": v(9.5, 25.4) * mm});
            skLineSegment(sketch, "E2.5.3.7", {"start": v(15, 22.8) * mm, "end": v(15, 19.34) * mm});
            skLineSegment(sketch, "E2.5.3.8", {"start": v(11, 29.73) * mm, "end": v(11, 26.27) * mm});
            skLineSegment(sketch, "E2.5.3.9", {"start": v(8, 31.46) * mm, "end": v(11, 29.73) * mm});
            skLineSegment(sketch, "E2.5.3.10", {"start": v(5, 29.73) * mm, "end": v(8, 31.46) * mm});
            skLineSegment(sketch, "E2.5.3.11", {"start": v(5, 26.27) * mm, "end": v(5, 29.73) * mm});
            skLineSegment(sketch, "E2.5.3.12", {"start": v(8, 24.54) * mm, "end": v(5, 26.27) * mm});
            skCircle(sketch, "E2.5.3.13", {"center": v(8, 28) * mm, "radius": 3 * mm, "construction": true});
            skLineSegment(sketch, "E2.5.3.14", {"start": v(15, 19.34) * mm, "end": v(12, 17.6) * mm});
            skLineSegment(sketch, "E2.5.3.15", {"start": v(11, 26.27) * mm, "end": v(8, 24.54) * mm});
            skCircle(sketch, "E2.6.0.0", {"center": v(20, -20.93) * mm, "radius": 3 * mm, "construction": true});
            skLineSegment(sketch, "E2.6.0.1", {"start": v(20, -24.4) * mm, "end": v(17, -22.66) * mm});
            skLineSegment(sketch, "E2.6.0.2", {"start": v(17, -22.66) * mm, "end": v(17, -19.2) * mm});
            skLineSegment(sketch, "E2.6.0.3", {"start": v(17, -19.2) * mm, "end": v(20, -17.46) * mm});
            skLineSegment(sketch, "E2.6.0.4", {"start": v(20, -17.46) * mm, "end": v(23, -19.2) * mm});
            skPoint(sketch, "E2.6.0.5", {"position": v(21.5, -23.53) * mm});
            skPoint(sketch, "E2.6.0.6", {"position": v(17.5, -16.6) * mm});
            skLineSegment(sketch, "E2.6.0.7", {"start": v(23, -19.2) * mm, "end": v(23, -22.66) * mm});
            skLineSegment(sketch, "E2.6.0.8", {"start": v(19, -12.27) * mm, "end": v(19, -15.73) * mm});
            skLineSegment(sketch, "E2.6.0.9", {"start": v(16, -10.54) * mm, "end": v(19, -12.27) * mm});
            skLineSegment(sketch, "E2.6.0.10", {"start": v(13, -12.27) * mm, "end": v(16, -10.54) * mm});
            skLineSegment(sketch, "E2.6.0.11", {"start": v(13, -15.73) * mm, "end": v(13, -12.27) * mm});
            skLineSegment(sketch, "E2.6.0.12", {"start": v(16, -17.46) * mm, "end": v(13, -15.73) * mm});
            skCircle(sketch, "E2.6.0.13", {"center": v(16, -14) * mm, "radius": 3 * mm, "construction": true});
            skLineSegment(sketch, "E2.6.0.14", {"start": v(23, -22.66) * mm, "end": v(20, -24.4) * mm});
            skLineSegment(sketch, "E2.6.0.15", {"start": v(19, -15.73) * mm, "end": v(16, -17.46) * mm});
            skCircle(sketch, "E2.6.1.0", {"center": v(20, -6.93) * mm, "radius": 3 * mm, "construction": true});
            skLineSegment(sketch, "E2.6.1.1", {"start": v(20, -10.4) * mm, "end": v(17, -8.66) * mm});
            skLineSegment(sketch, "E2.6.1.2", {"start": v(17, -8.66) * mm, "end": v(17, -5.2) * mm});
            skLineSegment(sketch, "E2.6.1.3", {"start": v(17, -5.2) * mm, "end": v(20, -3.46) * mm});
            skLineSegment(sketch, "E2.6.1.4", {"start": v(20, -3.46) * mm, "end": v(23, -5.2) * mm});
            skPoint(sketch, "E2.6.1.5", {"position": v(21.5, -9.53) * mm});
            skPoint(sketch, "E2.6.1.6", {"position": v(17.5, -2.6) * mm});
            skLineSegment(sketch, "E2.6.1.7", {"start": v(23, -5.2) * mm, "end": v(23, -8.66) * mm});
            skLineSegment(sketch, "E2.6.1.8", {"start": v(19, 1.73) * mm, "end": v(19, -1.73) * mm});
            skLineSegment(sketch, "E2.6.1.9", {"start": v(16, 3.46) * mm, "end": v(19, 1.73) * mm});
            skLineSegment(sketch, "E2.6.1.10", {"start": v(13, 1.73) * mm, "end": v(16, 3.46) * mm});
            skLineSegment(sketch, "E2.6.1.11", {"start": v(13, -1.73) * mm, "end": v(13, 1.73) * mm});
            skLineSegment(sketch, "E2.6.1.12", {"start": v(16, -3.46) * mm, "end": v(13, -1.73) * mm});
            skCircle(sketch, "E2.6.1.13", {"center": v(16, 0) * mm, "radius": 3 * mm, "construction": true});
            skLineSegment(sketch, "E2.6.1.14", {"start": v(23, -8.66) * mm, "end": v(20, -10.4) * mm});
            skLineSegment(sketch, "E2.6.1.15", {"start": v(19, -1.73) * mm, "end": v(16, -3.46) * mm});
            skCircle(sketch, "E2.6.2.0", {"center": v(20, 7.07) * mm, "radius": 3 * mm, "construction": true});
            skLineSegment(sketch, "E2.6.2.1", {"start": v(20, 3.6) * mm, "end": v(17, 5.34) * mm});
            skLineSegment(sketch, "E2.6.2.2", {"start": v(17, 5.34) * mm, "end": v(17, 8.8) * mm});
            skLineSegment(sketch, "E2.6.2.3", {"start": v(17, 8.8) * mm, "end": v(20, 10.54) * mm});
            skLineSegment(sketch, "E2.6.2.4", {"start": v(20, 10.54) * mm, "end": v(23, 8.8) * mm});
            skPoint(sketch, "E2.6.2.5", {"position": v(21.5, 4.47) * mm});
            skPoint(sketch, "E2.6.2.6", {"position": v(17.5, 11.4) * mm});
            skLineSegment(sketch, "E2.6.2.7", {"start": v(23, 8.8) * mm, "end": v(23, 5.34) * mm});
            skLineSegment(sketch, "E2.6.2.8", {"start": v(19, 15.73) * mm, "end": v(19, 12.27) * mm});
            skLineSegment(sketch, "E2.6.2.9", {"start": v(16, 17.46) * mm, "end": v(19, 15.73) * mm});
            skLineSegment(sketch, "E2.6.2.10", {"start": v(13, 15.73) * mm, "end": v(16, 17.46) * mm});
            skLineSegment(sketch, "E2.6.2.11", {"start": v(13, 12.27) * mm, "end": v(13, 15.73) * mm});
            skLineSegment(sketch, "E2.6.2.12", {"start": v(16, 10.54) * mm, "end": v(13, 12.27) * mm});
            skCircle(sketch, "E2.6.2.13", {"center": v(16, 14) * mm, "radius": 3 * mm, "construction": true});
            skLineSegment(sketch, "E2.6.2.14", {"start": v(23, 5.34) * mm, "end": v(20, 3.6) * mm});
            skLineSegment(sketch, "E2.6.2.15", {"start": v(19, 12.27) * mm, "end": v(16, 10.54) * mm});
            skCircle(sketch, "E2.6.3.0", {"center": v(20, 21.07) * mm, "radius": 3 * mm, "construction": true});
            skLineSegment(sketch, "E2.6.3.1", {"start": v(20, 17.6) * mm, "end": v(17, 19.34) * mm});
            skLineSegment(sketch, "E2.6.3.2", {"start": v(17, 19.34) * mm, "end": v(17, 22.8) * mm});
            skLineSegment(sketch, "E2.6.3.3", {"start": v(17, 22.8) * mm, "end": v(20, 24.54) * mm});
            skLineSegment(sketch, "E2.6.3.4", {"start": v(20, 24.54) * mm, "end": v(23, 22.8) * mm});
            skPoint(sketch, "E2.6.3.5", {"position": v(21.5, 18.47) * mm});
            skPoint(sketch, "E2.6.3.6", {"position": v(17.5, 25.4) * mm});
            skLineSegment(sketch, "E2.6.3.7", {"start": v(23, 22.8) * mm, "end": v(23, 19.34) * mm});
            skLineSegment(sketch, "E2.6.3.8", {"start": v(19, 29.73) * mm, "end": v(19, 26.27) * mm});
            skLineSegment(sketch, "E2.6.3.9", {"start": v(16, 31.46) * mm, "end": v(19, 29.73) * mm});
            skLineSegment(sketch, "E2.6.3.10", {"start": v(13, 29.73) * mm, "end": v(16, 31.46) * mm});
            skLineSegment(sketch, "E2.6.3.11", {"start": v(13, 26.27) * mm, "end": v(13, 29.73) * mm});
            skLineSegment(sketch, "E2.6.3.12", {"start": v(16, 24.54) * mm, "end": v(13, 26.27) * mm});
            skCircle(sketch, "E2.6.3.13", {"center": v(16, 28) * mm, "radius": 3 * mm, "construction": true});
            skLineSegment(sketch, "E2.6.3.14", {"start": v(23, 19.34) * mm, "end": v(20, 17.6) * mm});
            skLineSegment(sketch, "E2.6.3.15", {"start": v(19, 26.27) * mm, "end": v(16, 24.54) * mm});
            skCircle(sketch, "E2.7.0.0", {"center": v(28, -20.93) * mm, "radius": 3 * mm, "construction": true});
            skLineSegment(sketch, "E2.7.0.1", {"start": v(28, -24.4) * mm, "end": v(25, -22.66) * mm});
            skLineSegment(sketch, "E2.7.0.2", {"start": v(25, -22.66) * mm, "end": v(25, -19.2) * mm});
            skLineSegment(sketch, "E2.7.0.3", {"start": v(25, -19.2) * mm, "end": v(28, -17.46) * mm});
            skLineSegment(sketch, "E2.7.0.4", {"start": v(28, -17.46) * mm, "end": v(31, -19.2) * mm});
            skPoint(sketch, "E2.7.0.5", {"position": v(29.5, -23.53) * mm});
            skPoint(sketch, "E2.7.0.6", {"position": v(25.5, -16.6) * mm});
            skLineSegment(sketch, "E2.7.0.7", {"start": v(31, -19.2) * mm, "end": v(31, -22.66) * mm});
            skLineSegment(sketch, "E2.7.0.8", {"start": v(27, -12.27) * mm, "end": v(27, -15.73) * mm});
            skLineSegment(sketch, "E2.7.0.9", {"start": v(24, -10.54) * mm, "end": v(27, -12.27) * mm});
            skLineSegment(sketch, "E2.7.0.10", {"start": v(21, -12.27) * mm, "end": v(24, -10.54) * mm});
            skLineSegment(sketch, "E2.7.0.11", {"start": v(21, -15.73) * mm, "end": v(21, -12.27) * mm});
            skLineSegment(sketch, "E2.7.0.12", {"start": v(24, -17.46) * mm, "end": v(21, -15.73) * mm});
            skCircle(sketch, "E2.7.0.13", {"center": v(24, -14) * mm, "radius": 3 * mm, "construction": true});
            skLineSegment(sketch, "E2.7.0.14", {"start": v(31, -22.66) * mm, "end": v(28, -24.4) * mm});
            skLineSegment(sketch, "E2.7.0.15", {"start": v(27, -15.73) * mm, "end": v(24, -17.46) * mm});
            skCircle(sketch, "E2.7.1.0", {"center": v(28, -6.93) * mm, "radius": 3 * mm, "construction": true});
            skLineSegment(sketch, "E2.7.1.1", {"start": v(28, -10.4) * mm, "end": v(25, -8.66) * mm});
            skLineSegment(sketch, "E2.7.1.2", {"start": v(25, -8.66) * mm, "end": v(25, -5.2) * mm});
            skLineSegment(sketch, "E2.7.1.3", {"start": v(25, -5.2) * mm, "end": v(28, -3.46) * mm});
            skLineSegment(sketch, "E2.7.1.4", {"start": v(28, -3.46) * mm, "end": v(31, -5.2) * mm});
            skPoint(sketch, "E2.7.1.5", {"position": v(29.5, -9.53) * mm});
            skPoint(sketch, "E2.7.1.6", {"position": v(25.5, -2.6) * mm});
            skLineSegment(sketch, "E2.7.1.7", {"start": v(31, -5.2) * mm, "end": v(31, -8.66) * mm});
            skLineSegment(sketch, "E2.7.1.8", {"start": v(27, 1.73) * mm, "end": v(27, -1.73) * mm});
            skLineSegment(sketch, "E2.7.1.9", {"start": v(24, 3.46) * mm, "end": v(27, 1.73) * mm});
            skLineSegment(sketch, "E2.7.1.10", {"start": v(21, 1.73) * mm, "end": v(24, 3.46) * mm});
            skLineSegment(sketch, "E2.7.1.11", {"start": v(21, -1.73) * mm, "end": v(21, 1.73) * mm});
            skLineSegment(sketch, "E2.7.1.12", {"start": v(24, -3.46) * mm, "end": v(21, -1.73) * mm});
            skCircle(sketch, "E2.7.1.13", {"center": v(24, 0) * mm, "radius": 3 * mm, "construction": true});
            skLineSegment(sketch, "E2.7.1.14", {"start": v(31, -8.66) * mm, "end": v(28, -10.4) * mm});
            skLineSegment(sketch, "E2.7.1.15", {"start": v(27, -1.73) * mm, "end": v(24, -3.46) * mm});
            skCircle(sketch, "E2.7.2.0", {"center": v(28, 7.07) * mm, "radius": 3 * mm, "construction": true});
            skLineSegment(sketch, "E2.7.2.1", {"start": v(28, 3.6) * mm, "end": v(25, 5.34) * mm});
            skLineSegment(sketch, "E2.7.2.2", {"start": v(25, 5.34) * mm, "end": v(25, 8.8) * mm});
            skLineSegment(sketch, "E2.7.2.3", {"start": v(25, 8.8) * mm, "end": v(28, 10.54) * mm});
            skLineSegment(sketch, "E2.7.2.4", {"start": v(28, 10.54) * mm, "end": v(31, 8.8) * mm});
            skPoint(sketch, "E2.7.2.5", {"position": v(29.5, 4.47) * mm});
            skPoint(sketch, "E2.7.2.6", {"position": v(25.5, 11.4) * mm});
            skLineSegment(sketch, "E2.7.2.7", {"start": v(31, 8.8) * mm, "end": v(31, 5.34) * mm});
            skLineSegment(sketch, "E2.7.2.8", {"start": v(27, 15.73) * mm, "end": v(27, 12.27) * mm});
            skLineSegment(sketch, "E2.7.2.9", {"start": v(24, 17.46) * mm, "end": v(27, 15.73) * mm});
            skLineSegment(sketch, "E2.7.2.10", {"start": v(21, 15.73) * mm, "end": v(24, 17.46) * mm});
            skLineSegment(sketch, "E2.7.2.11", {"start": v(21, 12.27) * mm, "end": v(21, 15.73) * mm});
            skLineSegment(sketch, "E2.7.2.12", {"start": v(24, 10.54) * mm, "end": v(21, 12.27) * mm});
            skCircle(sketch, "E2.7.2.13", {"center": v(24, 14) * mm, "radius": 3 * mm, "construction": true});
            skLineSegment(sketch, "E2.7.2.14", {"start": v(31, 5.34) * mm, "end": v(28, 3.6) * mm});
            skLineSegment(sketch, "E2.7.2.15", {"start": v(27, 12.27) * mm, "end": v(24, 10.54) * mm});
            skCircle(sketch, "E2.7.3.0", {"center": v(28, 21.07) * mm, "radius": 3 * mm, "construction": true});
            skLineSegment(sketch, "E2.7.3.1", {"start": v(28, 17.6) * mm, "end": v(25, 19.34) * mm});
            skLineSegment(sketch, "E2.7.3.2", {"start": v(25, 19.34) * mm, "end": v(25, 22.8) * mm});
            skLineSegment(sketch, "E2.7.3.3", {"start": v(25, 22.8) * mm, "end": v(28, 24.54) * mm});
            skLineSegment(sketch, "E2.7.3.4", {"start": v(28, 24.54) * mm, "end": v(31, 22.8) * mm});
            skPoint(sketch, "E2.7.3.5", {"position": v(29.5, 18.47) * mm});
            skPoint(sketch, "E2.7.3.6", {"position": v(25.5, 25.4) * mm});
            skLineSegment(sketch, "E2.7.3.7", {"start": v(31, 22.8) * mm, "end": v(31, 19.34) * mm});
            skLineSegment(sketch, "E2.7.3.8", {"start": v(27, 29.73) * mm, "end": v(27, 26.27) * mm});
            skLineSegment(sketch, "E2.7.3.9", {"start": v(24, 31.46) * mm, "end": v(27, 29.73) * mm});
            skLineSegment(sketch, "E2.7.3.10", {"start": v(21, 29.73) * mm, "end": v(24, 31.46) * mm});
            skLineSegment(sketch, "E2.7.3.11", {"start": v(21, 26.27) * mm, "end": v(21, 29.73) * mm});
            skLineSegment(sketch, "E2.7.3.12", {"start": v(24, 24.54) * mm, "end": v(21, 26.27) * mm});
            skCircle(sketch, "E2.7.3.13", {"center": v(24, 28) * mm, "radius": 3 * mm, "construction": true});
            skLineSegment(sketch, "E2.7.3.14", {"start": v(31, 19.34) * mm, "end": v(28, 17.6) * mm});
            skLineSegment(sketch, "E2.7.3.15", {"start": v(27, 26.27) * mm, "end": v(24, 24.54) * mm});
            skLineSegment(sketch, "E2.direction1", {"start": v(-31, -22.66) * mm, "end": v(-23, -22.66) * mm, "construction": true});
            skLineSegment(sketch, "E2.direction2", {"start": v(-31, -22.66) * mm, "end": v(-31, -8.66) * mm, "construction": true});
            skLineSegment(sketch, "E3.bottom", {"start": v(-38, 60.6) * mm, "end": v(74, 60.6) * mm});
            skLineSegment(sketch, "E3.top", {"start": v(-38, -25.4) * mm, "end": v(74, -25.4) * mm});
            skLineSegment(sketch, "E3.left", {"start": v(-38, 60.6) * mm, "end": v(-38, -25.4) * mm});
            skLineSegment(sketch, "E3.right", {"start": v(74, 60.6) * mm, "end": v(74, -25.4) * mm});
            skCircle(sketch, "E4.0.8.0", {"center": v(36, -20.93) * mm, "radius": 3 * mm, "construction": true});
            skLineSegment(sketch, "E4.2.8.0", {"start": v(36, -24.4) * mm, "end": v(33, -22.66) * mm});
            skLineSegment(sketch, "E4.5.8.0", {"start": v(33, -22.66) * mm, "end": v(33, -19.2) * mm});
            skLineSegment(sketch, "E4.8.8.0", {"start": v(33, -19.2) * mm, "end": v(36, -17.46) * mm});
            skLineSegment(sketch, "E4.11.8.0", {"start": v(36, -17.46) * mm, "end": v(39, -19.2) * mm});
            skPoint(sketch, "E4.14.8.0", {"position": v(37.5, -23.53) * mm});
            skPoint(sketch, "E4.15.8.0", {"position": v(33.5, -16.6) * mm});
            skLineSegment(sketch, "E4.16.8.0", {"start": v(39, -19.2) * mm, "end": v(39, -22.66) * mm});
            skLineSegment(sketch, "E4.19.8.0", {"start": v(35, -12.27) * mm, "end": v(35, -15.73) * mm});
            skLineSegment(sketch, "E4.22.8.0", {"start": v(32, -10.54) * mm, "end": v(35, -12.27) * mm});
            skLineSegment(sketch, "E4.25.8.0", {"start": v(29, -12.27) * mm, "end": v(32, -10.54) * mm});
            skLineSegment(sketch, "E4.28.8.0", {"start": v(29, -15.73) * mm, "end": v(29, -12.27) * mm});
            skLineSegment(sketch, "E4.31.8.0", {"start": v(32, -17.46) * mm, "end": v(29, -15.73) * mm});
            skCircle(sketch, "E4.34.8.0", {"center": v(32, -14) * mm, "radius": 3 * mm, "construction": true});
            skLineSegment(sketch, "E4.36.8.0", {"start": v(39, -22.66) * mm, "end": v(36, -24.4) * mm});
            skLineSegment(sketch, "E4.39.8.0", {"start": v(35, -15.73) * mm, "end": v(32, -17.46) * mm});
            skCircle(sketch, "E4.0.8.1", {"center": v(36, -6.93) * mm, "radius": 3 * mm, "construction": true});
            skLineSegment(sketch, "E4.2.8.1", {"start": v(36, -10.4) * mm, "end": v(33, -8.66) * mm});
            skLineSegment(sketch, "E4.5.8.1", {"start": v(33, -8.66) * mm, "end": v(33, -5.2) * mm});
            skLineSegment(sketch, "E4.8.8.1", {"start": v(33, -5.2) * mm, "end": v(36, -3.46) * mm});
            skLineSegment(sketch, "E4.11.8.1", {"start": v(36, -3.46) * mm, "end": v(39, -5.2) * mm});
            skPoint(sketch, "E4.14.8.1", {"position": v(37.5, -9.53) * mm});
            skPoint(sketch, "E4.15.8.1", {"position": v(33.5, -2.6) * mm});
            skLineSegment(sketch, "E4.16.8.1", {"start": v(39, -5.2) * mm, "end": v(39, -8.66) * mm});
            skLineSegment(sketch, "E4.19.8.1", {"start": v(35, 1.73) * mm, "end": v(35, -1.73) * mm});
            skLineSegment(sketch, "E4.22.8.1", {"start": v(32, 3.46) * mm, "end": v(35, 1.73) * mm});
            skLineSegment(sketch, "E4.25.8.1", {"start": v(29, 1.73) * mm, "end": v(32, 3.46) * mm});
            skLineSegment(sketch, "E4.28.8.1", {"start": v(29, -1.73) * mm, "end": v(29, 1.73) * mm});
            skLineSegment(sketch, "E4.31.8.1", {"start": v(32, -3.46) * mm, "end": v(29, -1.73) * mm});
            skCircle(sketch, "E4.34.8.1", {"center": v(32, 0) * mm, "radius": 3 * mm, "construction": true});
            skLineSegment(sketch, "E4.36.8.1", {"start": v(39, -8.66) * mm, "end": v(36, -10.4) * mm});
            skLineSegment(sketch, "E4.39.8.1", {"start": v(35, -1.73) * mm, "end": v(32, -3.46) * mm});
            skCircle(sketch, "E4.0.8.2", {"center": v(36, 7.07) * mm, "radius": 3 * mm, "construction": true});
            skLineSegment(sketch, "E4.2.8.2", {"start": v(36, 3.6) * mm, "end": v(33, 5.34) * mm});
            skLineSegment(sketch, "E4.5.8.2", {"start": v(33, 5.34) * mm, "end": v(33, 8.8) * mm});
            skLineSegment(sketch, "E4.8.8.2", {"start": v(33, 8.8) * mm, "end": v(36, 10.54) * mm});
            skLineSegment(sketch, "E4.11.8.2", {"start": v(36, 10.54) * mm, "end": v(39, 8.8) * mm});
            skPoint(sketch, "E4.14.8.2", {"position": v(37.5, 4.47) * mm});
            skPoint(sketch, "E4.15.8.2", {"position": v(33.5, 11.4) * mm});
            skLineSegment(sketch, "E4.16.8.2", {"start": v(39, 8.8) * mm, "end": v(39, 5.34) * mm});
            skLineSegment(sketch, "E4.19.8.2", {"start": v(35, 15.73) * mm, "end": v(35, 12.27) * mm});
            skLineSegment(sketch, "E4.22.8.2", {"start": v(32, 17.46) * mm, "end": v(35, 15.73) * mm});
            skLineSegment(sketch, "E4.25.8.2", {"start": v(29, 15.73) * mm, "end": v(32, 17.46) * mm});
            skLineSegment(sketch, "E4.28.8.2", {"start": v(29, 12.27) * mm, "end": v(29, 15.73) * mm});
            skLineSegment(sketch, "E4.31.8.2", {"start": v(32, 10.54) * mm, "end": v(29, 12.27) * mm});
            skCircle(sketch, "E4.34.8.2", {"center": v(32, 14) * mm, "radius": 3 * mm, "construction": true});
            skLineSegment(sketch, "E4.36.8.2", {"start": v(39, 5.34) * mm, "end": v(36, 3.6) * mm});
            skLineSegment(sketch, "E4.39.8.2", {"start": v(35, 12.27) * mm, "end": v(32, 10.54) * mm});
            skCircle(sketch, "E4.0.8.3", {"center": v(36, 21.07) * mm, "radius": 3 * mm, "construction": true});
            skLineSegment(sketch, "E4.2.8.3", {"start": v(36, 17.6) * mm, "end": v(33, 19.34) * mm});
            skLineSegment(sketch, "E4.5.8.3", {"start": v(33, 19.34) * mm, "end": v(33, 22.8) * mm});
            skLineSegment(sketch, "E4.8.8.3", {"start": v(33, 22.8) * mm, "end": v(36, 24.54) * mm});
            skLineSegment(sketch, "E4.11.8.3", {"start": v(36, 24.54) * mm, "end": v(39, 22.8) * mm});
            skPoint(sketch, "E4.14.8.3", {"position": v(37.5, 18.47) * mm});
            skPoint(sketch, "E4.15.8.3", {"position": v(33.5, 25.4) * mm});
            skLineSegment(sketch, "E4.16.8.3", {"start": v(39, 22.8) * mm, "end": v(39, 19.34) * mm});
            skLineSegment(sketch, "E4.19.8.3", {"start": v(35, 29.73) * mm, "end": v(35, 26.27) * mm});
            skLineSegment(sketch, "E4.22.8.3", {"start": v(32, 31.46) * mm, "end": v(35, 29.73) * mm});
            skLineSegment(sketch, "E4.25.8.3", {"start": v(29, 29.73) * mm, "end": v(32, 31.46) * mm});
            skLineSegment(sketch, "E4.28.8.3", {"start": v(29, 26.27) * mm, "end": v(29, 29.73) * mm});
            skLineSegment(sketch, "E4.31.8.3", {"start": v(32, 24.54) * mm, "end": v(29, 26.27) * mm});
            skCircle(sketch, "E4.34.8.3", {"center": v(32, 28) * mm, "radius": 3 * mm, "construction": true});
            skLineSegment(sketch, "E4.36.8.3", {"start": v(39, 19.34) * mm, "end": v(36, 17.6) * mm});
            skLineSegment(sketch, "E4.39.8.3", {"start": v(35, 26.27) * mm, "end": v(32, 24.54) * mm});
            skCircle(sketch, "E4.0.9.0", {"center": v(44, -20.93) * mm, "radius": 3 * mm, "construction": true});
            skLineSegment(sketch, "E4.2.9.0", {"start": v(44, -24.4) * mm, "end": v(41, -22.66) * mm});
            skLineSegment(sketch, "E4.5.9.0", {"start": v(41, -22.66) * mm, "end": v(41, -19.2) * mm});
            skLineSegment(sketch, "E4.8.9.0", {"start": v(41, -19.2) * mm, "end": v(44, -17.46) * mm});
            skLineSegment(sketch, "E4.11.9.0", {"start": v(44, -17.46) * mm, "end": v(47, -19.2) * mm});
            skPoint(sketch, "E4.14.9.0", {"position": v(45.5, -23.53) * mm});
            skPoint(sketch, "E4.15.9.0", {"position": v(41.5, -16.6) * mm});
            skLineSegment(sketch, "E4.16.9.0", {"start": v(47, -19.2) * mm, "end": v(47, -22.66) * mm});
            skLineSegment(sketch, "E4.19.9.0", {"start": v(43, -12.27) * mm, "end": v(43, -15.73) * mm});
            skLineSegment(sketch, "E4.22.9.0", {"start": v(40, -10.54) * mm, "end": v(43, -12.27) * mm});
            skLineSegment(sketch, "E4.25.9.0", {"start": v(37, -12.27) * mm, "end": v(40, -10.54) * mm});
            skLineSegment(sketch, "E4.28.9.0", {"start": v(37, -15.73) * mm, "end": v(37, -12.27) * mm});
            skLineSegment(sketch, "E4.31.9.0", {"start": v(40, -17.46) * mm, "end": v(37, -15.73) * mm});
            skCircle(sketch, "E4.34.9.0", {"center": v(40, -14) * mm, "radius": 3 * mm, "construction": true});
            skLineSegment(sketch, "E4.36.9.0", {"start": v(47, -22.66) * mm, "end": v(44, -24.4) * mm});
            skLineSegment(sketch, "E4.39.9.0", {"start": v(43, -15.73) * mm, "end": v(40, -17.46) * mm});
            skCircle(sketch, "E4.0.9.1", {"center": v(44, -6.93) * mm, "radius": 3 * mm, "construction": true});
            skLineSegment(sketch, "E4.2.9.1", {"start": v(44, -10.4) * mm, "end": v(41, -8.66) * mm});
            skLineSegment(sketch, "E4.5.9.1", {"start": v(41, -8.66) * mm, "end": v(41, -5.2) * mm});
            skLineSegment(sketch, "E4.8.9.1", {"start": v(41, -5.2) * mm, "end": v(44, -3.46) * mm});
            skLineSegment(sketch, "E4.11.9.1", {"start": v(44, -3.46) * mm, "end": v(47, -5.2) * mm});
            skPoint(sketch, "E4.14.9.1", {"position": v(45.5, -9.53) * mm});
            skPoint(sketch, "E4.15.9.1", {"position": v(41.5, -2.6) * mm});
            skLineSegment(sketch, "E4.16.9.1", {"start": v(47, -5.2) * mm, "end": v(47, -8.66) * mm});
            skLineSegment(sketch, "E4.19.9.1", {"start": v(43, 1.73) * mm, "end": v(43, -1.73) * mm});
            skLineSegment(sketch, "E4.22.9.1", {"start": v(40, 3.46) * mm, "end": v(43, 1.73) * mm});
            skLineSegment(sketch, "E4.25.9.1", {"start": v(37, 1.73) * mm, "end": v(40, 3.46) * mm});
            skLineSegment(sketch, "E4.28.9.1", {"start": v(37, -1.73) * mm, "end": v(37, 1.73) * mm});
            skLineSegment(sketch, "E4.31.9.1", {"start": v(40, -3.46) * mm, "end": v(37, -1.73) * mm});
            skCircle(sketch, "E4.34.9.1", {"center": v(40, 0) * mm, "radius": 3 * mm, "construction": true});
            skLineSegment(sketch, "E4.36.9.1", {"start": v(47, -8.66) * mm, "end": v(44, -10.4) * mm});
            skLineSegment(sketch, "E4.39.9.1", {"start": v(43, -1.73) * mm, "end": v(40, -3.46) * mm});
            skCircle(sketch, "E4.0.9.2", {"center": v(44, 7.07) * mm, "radius": 3 * mm, "construction": true});
            skLineSegment(sketch, "E4.2.9.2", {"start": v(44, 3.6) * mm, "end": v(41, 5.34) * mm});
            skLineSegment(sketch, "E4.5.9.2", {"start": v(41, 5.34) * mm, "end": v(41, 8.8) * mm});
            skLineSegment(sketch, "E4.8.9.2", {"start": v(41, 8.8) * mm, "end": v(44, 10.54) * mm});
            skLineSegment(sketch, "E4.11.9.2", {"start": v(44, 10.54) * mm, "end": v(47, 8.8) * mm});
            skPoint(sketch, "E4.14.9.2", {"position": v(45.5, 4.47) * mm});
            skPoint(sketch, "E4.15.9.2", {"position": v(41.5, 11.4) * mm});
            skLineSegment(sketch, "E4.16.9.2", {"start": v(47, 8.8) * mm, "end": v(47, 5.34) * mm});
            skLineSegment(sketch, "E4.19.9.2", {"start": v(43, 15.73) * mm, "end": v(43, 12.27) * mm});
            skLineSegment(sketch, "E4.22.9.2", {"start": v(40, 17.46) * mm, "end": v(43, 15.73) * mm});
            skLineSegment(sketch, "E4.25.9.2", {"start": v(37, 15.73) * mm, "end": v(40, 17.46) * mm});
            skLineSegment(sketch, "E4.28.9.2", {"start": v(37, 12.27) * mm, "end": v(37, 15.73) * mm});
            skLineSegment(sketch, "E4.31.9.2", {"start": v(40, 10.54) * mm, "end": v(37, 12.27) * mm});
            skCircle(sketch, "E4.34.9.2", {"center": v(40, 14) * mm, "radius": 3 * mm, "construction": true});
            skLineSegment(sketch, "E4.36.9.2", {"start": v(47, 5.34) * mm, "end": v(44, 3.6) * mm});
            skLineSegment(sketch, "E4.39.9.2", {"start": v(43, 12.27) * mm, "end": v(40, 10.54) * mm});
            skCircle(sketch, "E4.0.9.3", {"center": v(44, 21.07) * mm, "radius": 3 * mm, "construction": true});
            skLineSegment(sketch, "E4.2.9.3", {"start": v(44, 17.6) * mm, "end": v(41, 19.34) * mm});
            skLineSegment(sketch, "E4.5.9.3", {"start": v(41, 19.34) * mm, "end": v(41, 22.8) * mm});
            skLineSegment(sketch, "E4.8.9.3", {"start": v(41, 22.8) * mm, "end": v(44, 24.54) * mm});
            skLineSegment(sketch, "E4.11.9.3", {"start": v(44, 24.54) * mm, "end": v(47, 22.8) * mm});
            skPoint(sketch, "E4.14.9.3", {"position": v(45.5, 18.47) * mm});
            skPoint(sketch, "E4.15.9.3", {"position": v(41.5, 25.4) * mm});
            skLineSegment(sketch, "E4.16.9.3", {"start": v(47, 22.8) * mm, "end": v(47, 19.34) * mm});
            skLineSegment(sketch, "E4.19.9.3", {"start": v(43, 29.73) * mm, "end": v(43, 26.27) * mm});
            skLineSegment(sketch, "E4.22.9.3", {"start": v(40, 31.46) * mm, "end": v(43, 29.73) * mm});
            skLineSegment(sketch, "E4.25.9.3", {"start": v(37, 29.73) * mm, "end": v(40, 31.46) * mm});
            skLineSegment(sketch, "E4.28.9.3", {"start": v(37, 26.27) * mm, "end": v(37, 29.73) * mm});
            skLineSegment(sketch, "E4.31.9.3", {"start": v(40, 24.54) * mm, "end": v(37, 26.27) * mm});
            skCircle(sketch, "E4.34.9.3", {"center": v(40, 28) * mm, "radius": 3 * mm, "construction": true});
            skLineSegment(sketch, "E4.36.9.3", {"start": v(47, 19.34) * mm, "end": v(44, 17.6) * mm});
            skLineSegment(sketch, "E4.39.9.3", {"start": v(43, 26.27) * mm, "end": v(40, 24.54) * mm});
            skCircle(sketch, "E5.0.10.0", {"center": v(52, -20.93) * mm, "radius": 3 * mm, "construction": true});
            skLineSegment(sketch, "E5.2.10.0", {"start": v(52, -24.4) * mm, "end": v(49, -22.66) * mm});
            skLineSegment(sketch, "E5.5.10.0", {"start": v(49, -22.66) * mm, "end": v(49, -19.2) * mm});
            skLineSegment(sketch, "E5.8.10.0", {"start": v(49, -19.2) * mm, "end": v(52, -17.46) * mm});
            skLineSegment(sketch, "E5.11.10.0", {"start": v(52, -17.46) * mm, "end": v(55, -19.2) * mm});
            skPoint(sketch, "E5.14.10.0", {"position": v(53.5, -23.53) * mm});
            skPoint(sketch, "E5.15.10.0", {"position": v(49.5, -16.6) * mm});
            skLineSegment(sketch, "E5.16.10.0", {"start": v(55, -19.2) * mm, "end": v(55, -22.66) * mm});
            skLineSegment(sketch, "E5.19.10.0", {"start": v(51, -12.27) * mm, "end": v(51, -15.73) * mm});
            skLineSegment(sketch, "E5.22.10.0", {"start": v(48, -10.54) * mm, "end": v(51, -12.27) * mm});
            skLineSegment(sketch, "E5.25.10.0", {"start": v(45, -12.27) * mm, "end": v(48, -10.54) * mm});
            skLineSegment(sketch, "E5.28.10.0", {"start": v(45, -15.73) * mm, "end": v(45, -12.27) * mm});
            skLineSegment(sketch, "E5.31.10.0", {"start": v(48, -17.46) * mm, "end": v(45, -15.73) * mm});
            skCircle(sketch, "E5.34.10.0", {"center": v(48, -14) * mm, "radius": 3 * mm, "construction": true});
            skLineSegment(sketch, "E5.36.10.0", {"start": v(55, -22.66) * mm, "end": v(52, -24.4) * mm});
            skLineSegment(sketch, "E5.39.10.0", {"start": v(51, -15.73) * mm, "end": v(48, -17.46) * mm});
            skCircle(sketch, "E5.0.10.1", {"center": v(52, -6.93) * mm, "radius": 3 * mm, "construction": true});
            skLineSegment(sketch, "E5.2.10.1", {"start": v(52, -10.4) * mm, "end": v(49, -8.66) * mm});
            skLineSegment(sketch, "E5.5.10.1", {"start": v(49, -8.66) * mm, "end": v(49, -5.2) * mm});
            skLineSegment(sketch, "E5.8.10.1", {"start": v(49, -5.2) * mm, "end": v(52, -3.46) * mm});
            skLineSegment(sketch, "E5.11.10.1", {"start": v(52, -3.46) * mm, "end": v(55, -5.2) * mm});
            skPoint(sketch, "E5.14.10.1", {"position": v(53.5, -9.53) * mm});
            skPoint(sketch, "E5.15.10.1", {"position": v(49.5, -2.6) * mm});
            skLineSegment(sketch, "E5.16.10.1", {"start": v(55, -5.2) * mm, "end": v(55, -8.66) * mm});
            skLineSegment(sketch, "E5.19.10.1", {"start": v(51, 1.73) * mm, "end": v(51, -1.73) * mm});
            skLineSegment(sketch, "E5.22.10.1", {"start": v(48, 3.46) * mm, "end": v(51, 1.73) * mm});
            skLineSegment(sketch, "E5.25.10.1", {"start": v(45, 1.73) * mm, "end": v(48, 3.46) * mm});
            skLineSegment(sketch, "E5.28.10.1", {"start": v(45, -1.73) * mm, "end": v(45, 1.73) * mm});
            skLineSegment(sketch, "E5.31.10.1", {"start": v(48, -3.46) * mm, "end": v(45, -1.73) * mm});
            skCircle(sketch, "E5.34.10.1", {"center": v(48, 0) * mm, "radius": 3 * mm, "construction": true});
            skLineSegment(sketch, "E5.36.10.1", {"start": v(55, -8.66) * mm, "end": v(52, -10.4) * mm});
            skLineSegment(sketch, "E5.39.10.1", {"start": v(51, -1.73) * mm, "end": v(48, -3.46) * mm});
            skCircle(sketch, "E5.0.10.2", {"center": v(52, 7.07) * mm, "radius": 3 * mm, "construction": true});
            skLineSegment(sketch, "E5.2.10.2", {"start": v(52, 3.6) * mm, "end": v(49, 5.34) * mm});
            skLineSegment(sketch, "E5.5.10.2", {"start": v(49, 5.34) * mm, "end": v(49, 8.8) * mm});
            skLineSegment(sketch, "E5.8.10.2", {"start": v(49, 8.8) * mm, "end": v(52, 10.54) * mm});
            skLineSegment(sketch, "E5.11.10.2", {"start": v(52, 10.54) * mm, "end": v(55, 8.8) * mm});
            skPoint(sketch, "E5.14.10.2", {"position": v(53.5, 4.47) * mm});
            skPoint(sketch, "E5.15.10.2", {"position": v(49.5, 11.4) * mm});
            skLineSegment(sketch, "E5.16.10.2", {"start": v(55, 8.8) * mm, "end": v(55, 5.34) * mm});
            skLineSegment(sketch, "E5.19.10.2", {"start": v(51, 15.73) * mm, "end": v(51, 12.27) * mm});
            skLineSegment(sketch, "E5.22.10.2", {"start": v(48, 17.46) * mm, "end": v(51, 15.73) * mm});
            skLineSegment(sketch, "E5.25.10.2", {"start": v(45, 15.73) * mm, "end": v(48, 17.46) * mm});
            skLineSegment(sketch, "E5.28.10.2", {"start": v(45, 12.27) * mm, "end": v(45, 15.73) * mm});
            skLineSegment(sketch, "E5.31.10.2", {"start": v(48, 10.54) * mm, "end": v(45, 12.27) * mm});
            skCircle(sketch, "E5.34.10.2", {"center": v(48, 14) * mm, "radius": 3 * mm, "construction": true});
            skLineSegment(sketch, "E5.36.10.2", {"start": v(55, 5.34) * mm, "end": v(52, 3.6) * mm});
            skLineSegment(sketch, "E5.39.10.2", {"start": v(51, 12.27) * mm, "end": v(48, 10.54) * mm});
            skCircle(sketch, "E5.0.10.3", {"center": v(52, 21.07) * mm, "radius": 3 * mm, "construction": true});
            skLineSegment(sketch, "E5.2.10.3", {"start": v(52, 17.6) * mm, "end": v(49, 19.34) * mm});
            skLineSegment(sketch, "E5.5.10.3", {"start": v(49, 19.34) * mm, "end": v(49, 22.8) * mm});
            skLineSegment(sketch, "E5.8.10.3", {"start": v(49, 22.8) * mm, "end": v(52, 24.54) * mm});
            skLineSegment(sketch, "E5.11.10.3", {"start": v(52, 24.54) * mm, "end": v(55, 22.8) * mm});
            skPoint(sketch, "E5.14.10.3", {"position": v(53.5, 18.47) * mm});
            skPoint(sketch, "E5.15.10.3", {"position": v(49.5, 25.4) * mm});
            skLineSegment(sketch, "E5.16.10.3", {"start": v(55, 22.8) * mm, "end": v(55, 19.34) * mm});
            skLineSegment(sketch, "E5.19.10.3", {"start": v(51, 29.73) * mm, "end": v(51, 26.27) * mm});
            skLineSegment(sketch, "E5.22.10.3", {"start": v(48, 31.46) * mm, "end": v(51, 29.73) * mm});
            skLineSegment(sketch, "E5.25.10.3", {"start": v(45, 29.73) * mm, "end": v(48, 31.46) * mm});
            skLineSegment(sketch, "E5.28.10.3", {"start": v(45, 26.27) * mm, "end": v(45, 29.73) * mm});
            skLineSegment(sketch, "E5.31.10.3", {"start": v(48, 24.54) * mm, "end": v(45, 26.27) * mm});
            skCircle(sketch, "E5.34.10.3", {"center": v(48, 28) * mm, "radius": 3 * mm, "construction": true});
            skLineSegment(sketch, "E5.36.10.3", {"start": v(55, 19.34) * mm, "end": v(52, 17.6) * mm});
            skLineSegment(sketch, "E5.39.10.3", {"start": v(51, 26.27) * mm, "end": v(48, 24.54) * mm});
            skCircle(sketch, "E6.0.0.4", {"center": v(-28, 35.07) * mm, "radius": 3 * mm, "construction": true});
            skLineSegment(sketch, "E6.2.0.4", {"start": v(-28, 31.6) * mm, "end": v(-31, 33.34) * mm});
            skLineSegment(sketch, "E6.5.0.4", {"start": v(-31, 33.34) * mm, "end": v(-31, 36.8) * mm});
            skLineSegment(sketch, "E6.8.0.4", {"start": v(-31, 36.8) * mm, "end": v(-28, 38.54) * mm});
            skLineSegment(sketch, "E6.11.0.4", {"start": v(-28, 38.54) * mm, "end": v(-25, 36.8) * mm});
            skPoint(sketch, "E6.14.0.4", {"position": v(-26.5, 32.47) * mm});
            skPoint(sketch, "E6.15.0.4", {"position": v(-30.5, 39.4) * mm});
            skLineSegment(sketch, "E6.16.0.4", {"start": v(-25, 36.8) * mm, "end": v(-25, 33.34) * mm});
            skLineSegment(sketch, "E6.19.0.4", {"start": v(-29, 43.73) * mm, "end": v(-29, 40.27) * mm});
            skLineSegment(sketch, "E6.22.0.4", {"start": v(-32, 45.46) * mm, "end": v(-29, 43.73) * mm});
            skLineSegment(sketch, "E6.25.0.4", {"start": v(-35, 43.73) * mm, "end": v(-32, 45.46) * mm});
            skLineSegment(sketch, "E6.28.0.4", {"start": v(-35, 40.27) * mm, "end": v(-35, 43.73) * mm});
            skLineSegment(sketch, "E6.31.0.4", {"start": v(-32, 38.54) * mm, "end": v(-35, 40.27) * mm});
            skCircle(sketch, "E6.34.0.4", {"center": v(-32, 42) * mm, "radius": 3 * mm, "construction": true});
            skLineSegment(sketch, "E6.36.0.4", {"start": v(-25, 33.34) * mm, "end": v(-28, 31.6) * mm});
            skLineSegment(sketch, "E6.39.0.4", {"start": v(-29, 40.27) * mm, "end": v(-32, 38.54) * mm});
            skCircle(sketch, "E6.0.0.5", {"center": v(-28, 49.07) * mm, "radius": 3 * mm, "construction": true});
            skLineSegment(sketch, "E6.2.0.5", {"start": v(-28, 45.6) * mm, "end": v(-31, 47.34) * mm});
            skLineSegment(sketch, "E6.5.0.5", {"start": v(-31, 47.34) * mm, "end": v(-31, 50.8) * mm});
            skLineSegment(sketch, "E6.8.0.5", {"start": v(-31, 50.8) * mm, "end": v(-28, 52.54) * mm});
            skLineSegment(sketch, "E6.11.0.5", {"start": v(-28, 52.54) * mm, "end": v(-25, 50.8) * mm});
            skPoint(sketch, "E6.14.0.5", {"position": v(-26.5, 46.47) * mm});
            skPoint(sketch, "E6.15.0.5", {"position": v(-30.5, 53.4) * mm});
            skLineSegment(sketch, "E6.16.0.5", {"start": v(-25, 50.8) * mm, "end": v(-25, 47.34) * mm});
            skLineSegment(sketch, "E6.19.0.5", {"start": v(-29, 57.73) * mm, "end": v(-29, 54.27) * mm});
            skLineSegment(sketch, "E6.22.0.5", {"start": v(-32, 59.46) * mm, "end": v(-29, 57.73) * mm});
            skLineSegment(sketch, "E6.25.0.5", {"start": v(-35, 57.73) * mm, "end": v(-32, 59.46) * mm});
            skLineSegment(sketch, "E6.28.0.5", {"start": v(-35, 54.27) * mm, "end": v(-35, 57.73) * mm});
            skLineSegment(sketch, "E6.31.0.5", {"start": v(-32, 52.54) * mm, "end": v(-35, 54.27) * mm});
            skCircle(sketch, "E6.34.0.5", {"center": v(-32, 56) * mm, "radius": 3 * mm, "construction": true});
            skLineSegment(sketch, "E6.36.0.5", {"start": v(-25, 47.34) * mm, "end": v(-28, 45.6) * mm});
            skLineSegment(sketch, "E6.39.0.5", {"start": v(-29, 54.27) * mm, "end": v(-32, 52.54) * mm});
            skCircle(sketch, "E6.0.1.4", {"center": v(-20, 35.07) * mm, "radius": 3 * mm, "construction": true});
            skLineSegment(sketch, "E6.2.1.4", {"start": v(-20, 31.6) * mm, "end": v(-23, 33.34) * mm});
            skLineSegment(sketch, "E6.5.1.4", {"start": v(-23, 33.34) * mm, "end": v(-23, 36.8) * mm});
            skLineSegment(sketch, "E6.8.1.4", {"start": v(-23, 36.8) * mm, "end": v(-20, 38.54) * mm});
            skLineSegment(sketch, "E6.11.1.4", {"start": v(-20, 38.54) * mm, "end": v(-17, 36.8) * mm});
            skPoint(sketch, "E6.14.1.4", {"position": v(-18.5, 32.47) * mm});
            skPoint(sketch, "E6.15.1.4", {"position": v(-22.5, 39.4) * mm});
            skLineSegment(sketch, "E6.16.1.4", {"start": v(-17, 36.8) * mm, "end": v(-17, 33.34) * mm});
            skLineSegment(sketch, "E6.19.1.4", {"start": v(-21, 43.73) * mm, "end": v(-21, 40.27) * mm});
            skLineSegment(sketch, "E6.22.1.4", {"start": v(-24, 45.46) * mm, "end": v(-21, 43.73) * mm});
            skLineSegment(sketch, "E6.25.1.4", {"start": v(-27, 43.73) * mm, "end": v(-24, 45.46) * mm});
            skLineSegment(sketch, "E6.28.1.4", {"start": v(-27, 40.27) * mm, "end": v(-27, 43.73) * mm});
            skLineSegment(sketch, "E6.31.1.4", {"start": v(-24, 38.54) * mm, "end": v(-27, 40.27) * mm});
            skCircle(sketch, "E6.34.1.4", {"center": v(-24, 42) * mm, "radius": 3 * mm, "construction": true});
            skLineSegment(sketch, "E6.36.1.4", {"start": v(-17, 33.34) * mm, "end": v(-20, 31.6) * mm});
            skLineSegment(sketch, "E6.39.1.4", {"start": v(-21, 40.27) * mm, "end": v(-24, 38.54) * mm});
            skCircle(sketch, "E6.0.1.5", {"center": v(-20, 49.07) * mm, "radius": 3 * mm, "construction": true});
            skLineSegment(sketch, "E6.2.1.5", {"start": v(-20, 45.6) * mm, "end": v(-23, 47.34) * mm});
            skLineSegment(sketch, "E6.5.1.5", {"start": v(-23, 47.34) * mm, "end": v(-23, 50.8) * mm});
            skLineSegment(sketch, "E6.8.1.5", {"start": v(-23, 50.8) * mm, "end": v(-20, 52.54) * mm});
            skLineSegment(sketch, "E6.11.1.5", {"start": v(-20, 52.54) * mm, "end": v(-17, 50.8) * mm});
            skPoint(sketch, "E6.14.1.5", {"position": v(-18.5, 46.47) * mm});
            skPoint(sketch, "E6.15.1.5", {"position": v(-22.5, 53.4) * mm});
            skLineSegment(sketch, "E6.16.1.5", {"start": v(-17, 50.8) * mm, "end": v(-17, 47.34) * mm});
            skLineSegment(sketch, "E6.19.1.5", {"start": v(-21, 57.73) * mm, "end": v(-21, 54.27) * mm});
            skLineSegment(sketch, "E6.22.1.5", {"start": v(-24, 59.46) * mm, "end": v(-21, 57.73) * mm});
            skLineSegment(sketch, "E6.25.1.5", {"start": v(-27, 57.73) * mm, "end": v(-24, 59.46) * mm});
            skLineSegment(sketch, "E6.28.1.5", {"start": v(-27, 54.27) * mm, "end": v(-27, 57.73) * mm});
            skLineSegment(sketch, "E6.31.1.5", {"start": v(-24, 52.54) * mm, "end": v(-27, 54.27) * mm});
            skCircle(sketch, "E6.34.1.5", {"center": v(-24, 56) * mm, "radius": 3 * mm, "construction": true});
            skLineSegment(sketch, "E6.36.1.5", {"start": v(-17, 47.34) * mm, "end": v(-20, 45.6) * mm});
            skLineSegment(sketch, "E6.39.1.5", {"start": v(-21, 54.27) * mm, "end": v(-24, 52.54) * mm});
            skCircle(sketch, "E6.0.2.4", {"center": v(-12, 35.07) * mm, "radius": 3 * mm, "construction": true});
            skLineSegment(sketch, "E6.2.2.4", {"start": v(-12, 31.6) * mm, "end": v(-15, 33.34) * mm});
            skLineSegment(sketch, "E6.5.2.4", {"start": v(-15, 33.34) * mm, "end": v(-15, 36.8) * mm});
            skLineSegment(sketch, "E6.8.2.4", {"start": v(-15, 36.8) * mm, "end": v(-12, 38.54) * mm});
            skLineSegment(sketch, "E6.11.2.4", {"start": v(-12, 38.54) * mm, "end": v(-9, 36.8) * mm});
            skPoint(sketch, "E6.14.2.4", {"position": v(-10.5, 32.47) * mm});
            skPoint(sketch, "E6.15.2.4", {"position": v(-14.5, 39.4) * mm});
            skLineSegment(sketch, "E6.16.2.4", {"start": v(-9, 36.8) * mm, "end": v(-9, 33.34) * mm});
            skLineSegment(sketch, "E6.19.2.4", {"start": v(-13, 43.73) * mm, "end": v(-13, 40.27) * mm});
            skLineSegment(sketch, "E6.22.2.4", {"start": v(-16, 45.46) * mm, "end": v(-13, 43.73) * mm});
            skLineSegment(sketch, "E6.25.2.4", {"start": v(-19, 43.73) * mm, "end": v(-16, 45.46) * mm});
            skLineSegment(sketch, "E6.28.2.4", {"start": v(-19, 40.27) * mm, "end": v(-19, 43.73) * mm});
            skLineSegment(sketch, "E6.31.2.4", {"start": v(-16, 38.54) * mm, "end": v(-19, 40.27) * mm});
            skCircle(sketch, "E6.34.2.4", {"center": v(-16, 42) * mm, "radius": 3 * mm, "construction": true});
            skLineSegment(sketch, "E6.36.2.4", {"start": v(-9, 33.34) * mm, "end": v(-12, 31.6) * mm});
            skLineSegment(sketch, "E6.39.2.4", {"start": v(-13, 40.27) * mm, "end": v(-16, 38.54) * mm});
            skCircle(sketch, "E6.0.2.5", {"center": v(-12, 49.07) * mm, "radius": 3 * mm, "construction": true});
            skLineSegment(sketch, "E6.2.2.5", {"start": v(-12, 45.6) * mm, "end": v(-15, 47.34) * mm});
            skLineSegment(sketch, "E6.5.2.5", {"start": v(-15, 47.34) * mm, "end": v(-15, 50.8) * mm});
            skLineSegment(sketch, "E6.8.2.5", {"start": v(-15, 50.8) * mm, "end": v(-12, 52.54) * mm});
            skLineSegment(sketch, "E6.11.2.5", {"start": v(-12, 52.54) * mm, "end": v(-9, 50.8) * mm});
            skPoint(sketch, "E6.14.2.5", {"position": v(-10.5, 46.47) * mm});
            skPoint(sketch, "E6.15.2.5", {"position": v(-14.5, 53.4) * mm});
            skLineSegment(sketch, "E6.16.2.5", {"start": v(-9, 50.8) * mm, "end": v(-9, 47.34) * mm});
            skLineSegment(sketch, "E6.19.2.5", {"start": v(-13, 57.73) * mm, "end": v(-13, 54.27) * mm});
            skLineSegment(sketch, "E6.22.2.5", {"start": v(-16, 59.46) * mm, "end": v(-13, 57.73) * mm});
            skLineSegment(sketch, "E6.25.2.5", {"start": v(-19, 57.73) * mm, "end": v(-16, 59.46) * mm});
            skLineSegment(sketch, "E6.28.2.5", {"start": v(-19, 54.27) * mm, "end": v(-19, 57.73) * mm});
            skLineSegment(sketch, "E6.31.2.5", {"start": v(-16, 52.54) * mm, "end": v(-19, 54.27) * mm});
            skCircle(sketch, "E6.34.2.5", {"center": v(-16, 56) * mm, "radius": 3 * mm, "construction": true});
            skLineSegment(sketch, "E6.36.2.5", {"start": v(-9, 47.34) * mm, "end": v(-12, 45.6) * mm});
            skLineSegment(sketch, "E6.39.2.5", {"start": v(-13, 54.27) * mm, "end": v(-16, 52.54) * mm});
            skCircle(sketch, "E6.0.3.4", {"center": v(-4, 35.07) * mm, "radius": 3 * mm, "construction": true});
            skLineSegment(sketch, "E6.2.3.4", {"start": v(-4, 31.6) * mm, "end": v(-7, 33.34) * mm});
            skLineSegment(sketch, "E6.5.3.4", {"start": v(-7, 33.34) * mm, "end": v(-7, 36.8) * mm});
            skLineSegment(sketch, "E6.8.3.4", {"start": v(-7, 36.8) * mm, "end": v(-4, 38.54) * mm});
            skLineSegment(sketch, "E6.11.3.4", {"start": v(-4, 38.54) * mm, "end": v(-1, 36.8) * mm});
            skPoint(sketch, "E6.14.3.4", {"position": v(-2.5, 32.47) * mm});
            skPoint(sketch, "E6.15.3.4", {"position": v(-6.5, 39.4) * mm});
            skLineSegment(sketch, "E6.16.3.4", {"start": v(-1, 36.8) * mm, "end": v(-1, 33.34) * mm});
            skLineSegment(sketch, "E6.19.3.4", {"start": v(-5, 43.73) * mm, "end": v(-5, 40.27) * mm});
            skLineSegment(sketch, "E6.22.3.4", {"start": v(-8, 45.46) * mm, "end": v(-5, 43.73) * mm});
            skLineSegment(sketch, "E6.25.3.4", {"start": v(-11, 43.73) * mm, "end": v(-8, 45.46) * mm});
            skLineSegment(sketch, "E6.28.3.4", {"start": v(-11, 40.27) * mm, "end": v(-11, 43.73) * mm});
            skLineSegment(sketch, "E6.31.3.4", {"start": v(-8, 38.54) * mm, "end": v(-11, 40.27) * mm});
            skCircle(sketch, "E6.34.3.4", {"center": v(-8, 42) * mm, "radius": 3 * mm, "construction": true});
            skLineSegment(sketch, "E6.36.3.4", {"start": v(-1, 33.34) * mm, "end": v(-4, 31.6) * mm});
            skLineSegment(sketch, "E6.39.3.4", {"start": v(-5, 40.27) * mm, "end": v(-8, 38.54) * mm});
            skCircle(sketch, "E6.0.3.5", {"center": v(-4, 49.07) * mm, "radius": 3 * mm, "construction": true});
            skLineSegment(sketch, "E6.2.3.5", {"start": v(-4, 45.6) * mm, "end": v(-7, 47.34) * mm});
            skLineSegment(sketch, "E6.5.3.5", {"start": v(-7, 47.34) * mm, "end": v(-7, 50.8) * mm});
            skLineSegment(sketch, "E6.8.3.5", {"start": v(-7, 50.8) * mm, "end": v(-4, 52.54) * mm});
            skLineSegment(sketch, "E6.11.3.5", {"start": v(-4, 52.54) * mm, "end": v(-1, 50.8) * mm});
            skPoint(sketch, "E6.14.3.5", {"position": v(-2.5, 46.47) * mm});
            skPoint(sketch, "E6.15.3.5", {"position": v(-6.5, 53.4) * mm});
            skLineSegment(sketch, "E6.16.3.5", {"start": v(-1, 50.8) * mm, "end": v(-1, 47.34) * mm});
            skLineSegment(sketch, "E6.19.3.5", {"start": v(-5, 57.73) * mm, "end": v(-5, 54.27) * mm});
            skLineSegment(sketch, "E6.22.3.5", {"start": v(-8, 59.46) * mm, "end": v(-5, 57.73) * mm});
            skLineSegment(sketch, "E6.25.3.5", {"start": v(-11, 57.73) * mm, "end": v(-8, 59.46) * mm});
            skLineSegment(sketch, "E6.28.3.5", {"start": v(-11, 54.27) * mm, "end": v(-11, 57.73) * mm});
            skLineSegment(sketch, "E6.31.3.5", {"start": v(-8, 52.54) * mm, "end": v(-11, 54.27) * mm});
            skCircle(sketch, "E6.34.3.5", {"center": v(-8, 56) * mm, "radius": 3 * mm, "construction": true});
            skLineSegment(sketch, "E6.36.3.5", {"start": v(-1, 47.34) * mm, "end": v(-4, 45.6) * mm});
            skLineSegment(sketch, "E6.39.3.5", {"start": v(-5, 54.27) * mm, "end": v(-8, 52.54) * mm});
            skCircle(sketch, "E6.0.4.4", {"center": v(4, 35.07) * mm, "radius": 3 * mm, "construction": true});
            skLineSegment(sketch, "E6.2.4.4", {"start": v(4, 31.6) * mm, "end": v(1, 33.34) * mm});
            skLineSegment(sketch, "E6.5.4.4", {"start": v(1, 33.34) * mm, "end": v(1, 36.8) * mm});
            skLineSegment(sketch, "E6.8.4.4", {"start": v(1, 36.8) * mm, "end": v(4, 38.54) * mm});
            skLineSegment(sketch, "E6.11.4.4", {"start": v(4, 38.54) * mm, "end": v(7, 36.8) * mm});
            skPoint(sketch, "E6.14.4.4", {"position": v(5.5, 32.47) * mm});
            skPoint(sketch, "E6.15.4.4", {"position": v(1.5, 39.4) * mm});
            skLineSegment(sketch, "E6.16.4.4", {"start": v(7, 36.8) * mm, "end": v(7, 33.34) * mm});
            skLineSegment(sketch, "E6.19.4.4", {"start": v(3, 43.73) * mm, "end": v(3, 40.27) * mm});
            skLineSegment(sketch, "E6.22.4.4", {"start": v(0, 45.46) * mm, "end": v(3, 43.73) * mm});
            skLineSegment(sketch, "E6.25.4.4", {"start": v(-3, 43.73) * mm, "end": v(0, 45.46) * mm});
            skLineSegment(sketch, "E6.28.4.4", {"start": v(-3, 40.27) * mm, "end": v(-3, 43.73) * mm});
            skLineSegment(sketch, "E6.31.4.4", {"start": v(0, 38.54) * mm, "end": v(-3, 40.27) * mm});
            skCircle(sketch, "E6.34.4.4", {"center": v(0, 42) * mm, "radius": 3 * mm, "construction": true});
            skLineSegment(sketch, "E6.36.4.4", {"start": v(7, 33.34) * mm, "end": v(4, 31.6) * mm});
            skLineSegment(sketch, "E6.39.4.4", {"start": v(3, 40.27) * mm, "end": v(0, 38.54) * mm});
            skCircle(sketch, "E6.0.4.5", {"center": v(4, 49.07) * mm, "radius": 3 * mm, "construction": true});
            skLineSegment(sketch, "E6.2.4.5", {"start": v(4, 45.6) * mm, "end": v(1, 47.34) * mm});
            skLineSegment(sketch, "E6.5.4.5", {"start": v(1, 47.34) * mm, "end": v(1, 50.8) * mm});
            skLineSegment(sketch, "E6.8.4.5", {"start": v(1, 50.8) * mm, "end": v(4, 52.54) * mm});
            skLineSegment(sketch, "E6.11.4.5", {"start": v(4, 52.54) * mm, "end": v(7, 50.8) * mm});
            skPoint(sketch, "E6.14.4.5", {"position": v(5.5, 46.47) * mm});
            skPoint(sketch, "E6.15.4.5", {"position": v(1.5, 53.4) * mm});
            skLineSegment(sketch, "E6.16.4.5", {"start": v(7, 50.8) * mm, "end": v(7, 47.34) * mm});
            skLineSegment(sketch, "E6.19.4.5", {"start": v(3, 57.73) * mm, "end": v(3, 54.27) * mm});
            skLineSegment(sketch, "E6.22.4.5", {"start": v(0, 59.46) * mm, "end": v(3, 57.73) * mm});
            skLineSegment(sketch, "E6.25.4.5", {"start": v(-3, 57.73) * mm, "end": v(0, 59.46) * mm});
            skLineSegment(sketch, "E6.28.4.5", {"start": v(-3, 54.27) * mm, "end": v(-3, 57.73) * mm});
            skLineSegment(sketch, "E6.31.4.5", {"start": v(0, 52.54) * mm, "end": v(-3, 54.27) * mm});
            skCircle(sketch, "E6.34.4.5", {"center": v(0, 56) * mm, "radius": 3 * mm, "construction": true});
            skLineSegment(sketch, "E6.36.4.5", {"start": v(7, 47.34) * mm, "end": v(4, 45.6) * mm});
            skLineSegment(sketch, "E6.39.4.5", {"start": v(3, 54.27) * mm, "end": v(0, 52.54) * mm});
            skCircle(sketch, "E6.0.5.4", {"center": v(12, 35.07) * mm, "radius": 3 * mm, "construction": true});
            skLineSegment(sketch, "E6.2.5.4", {"start": v(12, 31.6) * mm, "end": v(9, 33.34) * mm});
            skLineSegment(sketch, "E6.5.5.4", {"start": v(9, 33.34) * mm, "end": v(9, 36.8) * mm});
            skLineSegment(sketch, "E6.8.5.4", {"start": v(9, 36.8) * mm, "end": v(12, 38.54) * mm});
            skLineSegment(sketch, "E6.11.5.4", {"start": v(12, 38.54) * mm, "end": v(15, 36.8) * mm});
            skPoint(sketch, "E6.14.5.4", {"position": v(13.5, 32.47) * mm});
            skPoint(sketch, "E6.15.5.4", {"position": v(9.5, 39.4) * mm});
            skLineSegment(sketch, "E6.16.5.4", {"start": v(15, 36.8) * mm, "end": v(15, 33.34) * mm});
            skLineSegment(sketch, "E6.19.5.4", {"start": v(11, 43.73) * mm, "end": v(11, 40.27) * mm});
            skLineSegment(sketch, "E6.22.5.4", {"start": v(8, 45.46) * mm, "end": v(11, 43.73) * mm});
            skLineSegment(sketch, "E6.25.5.4", {"start": v(5, 43.73) * mm, "end": v(8, 45.46) * mm});
            skLineSegment(sketch, "E6.28.5.4", {"start": v(5, 40.27) * mm, "end": v(5, 43.73) * mm});
            skLineSegment(sketch, "E6.31.5.4", {"start": v(8, 38.54) * mm, "end": v(5, 40.27) * mm});
            skCircle(sketch, "E6.34.5.4", {"center": v(8, 42) * mm, "radius": 3 * mm, "construction": true});
            skLineSegment(sketch, "E6.36.5.4", {"start": v(15, 33.34) * mm, "end": v(12, 31.6) * mm});
            skLineSegment(sketch, "E6.39.5.4", {"start": v(11, 40.27) * mm, "end": v(8, 38.54) * mm});
            skCircle(sketch, "E6.0.5.5", {"center": v(12, 49.07) * mm, "radius": 3 * mm, "construction": true});
            skLineSegment(sketch, "E6.2.5.5", {"start": v(12, 45.6) * mm, "end": v(9, 47.34) * mm});
            skLineSegment(sketch, "E6.5.5.5", {"start": v(9, 47.34) * mm, "end": v(9, 50.8) * mm});
            skLineSegment(sketch, "E6.8.5.5", {"start": v(9, 50.8) * mm, "end": v(12, 52.54) * mm});
            skLineSegment(sketch, "E6.11.5.5", {"start": v(12, 52.54) * mm, "end": v(15, 50.8) * mm});
            skPoint(sketch, "E6.14.5.5", {"position": v(13.5, 46.47) * mm});
            skPoint(sketch, "E6.15.5.5", {"position": v(9.5, 53.4) * mm});
            skLineSegment(sketch, "E6.16.5.5", {"start": v(15, 50.8) * mm, "end": v(15, 47.34) * mm});
            skLineSegment(sketch, "E6.19.5.5", {"start": v(11, 57.73) * mm, "end": v(11, 54.27) * mm});
            skLineSegment(sketch, "E6.22.5.5", {"start": v(8, 59.46) * mm, "end": v(11, 57.73) * mm});
            skLineSegment(sketch, "E6.25.5.5", {"start": v(5, 57.73) * mm, "end": v(8, 59.46) * mm});
            skLineSegment(sketch, "E6.28.5.5", {"start": v(5, 54.27) * mm, "end": v(5, 57.73) * mm});
            skLineSegment(sketch, "E6.31.5.5", {"start": v(8, 52.54) * mm, "end": v(5, 54.27) * mm});
            skCircle(sketch, "E6.34.5.5", {"center": v(8, 56) * mm, "radius": 3 * mm, "construction": true});
            skLineSegment(sketch, "E6.36.5.5", {"start": v(15, 47.34) * mm, "end": v(12, 45.6) * mm});
            skLineSegment(sketch, "E6.39.5.5", {"start": v(11, 54.27) * mm, "end": v(8, 52.54) * mm});
            skCircle(sketch, "E6.0.6.4", {"center": v(20, 35.07) * mm, "radius": 3 * mm, "construction": true});
            skLineSegment(sketch, "E6.2.6.4", {"start": v(20, 31.6) * mm, "end": v(17, 33.34) * mm});
            skLineSegment(sketch, "E6.5.6.4", {"start": v(17, 33.34) * mm, "end": v(17, 36.8) * mm});
            skLineSegment(sketch, "E6.8.6.4", {"start": v(17, 36.8) * mm, "end": v(20, 38.54) * mm});
            skLineSegment(sketch, "E6.11.6.4", {"start": v(20, 38.54) * mm, "end": v(23, 36.8) * mm});
            skPoint(sketch, "E6.14.6.4", {"position": v(21.5, 32.47) * mm});
            skPoint(sketch, "E6.15.6.4", {"position": v(17.5, 39.4) * mm});
            skLineSegment(sketch, "E6.16.6.4", {"start": v(23, 36.8) * mm, "end": v(23, 33.34) * mm});
            skLineSegment(sketch, "E6.19.6.4", {"start": v(19, 43.73) * mm, "end": v(19, 40.27) * mm});
            skLineSegment(sketch, "E6.22.6.4", {"start": v(16, 45.46) * mm, "end": v(19, 43.73) * mm});
            skLineSegment(sketch, "E6.25.6.4", {"start": v(13, 43.73) * mm, "end": v(16, 45.46) * mm});
            skLineSegment(sketch, "E6.28.6.4", {"start": v(13, 40.27) * mm, "end": v(13, 43.73) * mm});
            skLineSegment(sketch, "E6.31.6.4", {"start": v(16, 38.54) * mm, "end": v(13, 40.27) * mm});
            skCircle(sketch, "E6.34.6.4", {"center": v(16, 42) * mm, "radius": 3 * mm, "construction": true});
            skLineSegment(sketch, "E6.36.6.4", {"start": v(23, 33.34) * mm, "end": v(20, 31.6) * mm});
            skLineSegment(sketch, "E6.39.6.4", {"start": v(19, 40.27) * mm, "end": v(16, 38.54) * mm});
            skCircle(sketch, "E6.0.6.5", {"center": v(20, 49.07) * mm, "radius": 3 * mm, "construction": true});
            skLineSegment(sketch, "E6.2.6.5", {"start": v(20, 45.6) * mm, "end": v(17, 47.34) * mm});
            skLineSegment(sketch, "E6.5.6.5", {"start": v(17, 47.34) * mm, "end": v(17, 50.8) * mm});
            skLineSegment(sketch, "E6.8.6.5", {"start": v(17, 50.8) * mm, "end": v(20, 52.54) * mm});
            skLineSegment(sketch, "E6.11.6.5", {"start": v(20, 52.54) * mm, "end": v(23, 50.8) * mm});
            skPoint(sketch, "E6.14.6.5", {"position": v(21.5, 46.47) * mm});
            skPoint(sketch, "E6.15.6.5", {"position": v(17.5, 53.4) * mm});
            skLineSegment(sketch, "E6.16.6.5", {"start": v(23, 50.8) * mm, "end": v(23, 47.34) * mm});
            skLineSegment(sketch, "E6.19.6.5", {"start": v(19, 57.73) * mm, "end": v(19, 54.27) * mm});
            skLineSegment(sketch, "E6.22.6.5", {"start": v(16, 59.46) * mm, "end": v(19, 57.73) * mm});
            skLineSegment(sketch, "E6.25.6.5", {"start": v(13, 57.73) * mm, "end": v(16, 59.46) * mm});
            skLineSegment(sketch, "E6.28.6.5", {"start": v(13, 54.27) * mm, "end": v(13, 57.73) * mm});
            skLineSegment(sketch, "E6.31.6.5", {"start": v(16, 52.54) * mm, "end": v(13, 54.27) * mm});
            skCircle(sketch, "E6.34.6.5", {"center": v(16, 56) * mm, "radius": 3 * mm, "construction": true});
            skLineSegment(sketch, "E6.36.6.5", {"start": v(23, 47.34) * mm, "end": v(20, 45.6) * mm});
            skLineSegment(sketch, "E6.39.6.5", {"start": v(19, 54.27) * mm, "end": v(16, 52.54) * mm});
            skCircle(sketch, "E6.0.7.4", {"center": v(28, 35.07) * mm, "radius": 3 * mm, "construction": true});
            skLineSegment(sketch, "E6.2.7.4", {"start": v(28, 31.6) * mm, "end": v(25, 33.34) * mm});
            skLineSegment(sketch, "E6.5.7.4", {"start": v(25, 33.34) * mm, "end": v(25, 36.8) * mm});
            skLineSegment(sketch, "E6.8.7.4", {"start": v(25, 36.8) * mm, "end": v(28, 38.54) * mm});
            skLineSegment(sketch, "E6.11.7.4", {"start": v(28, 38.54) * mm, "end": v(31, 36.8) * mm});
            skPoint(sketch, "E6.14.7.4", {"position": v(29.5, 32.47) * mm});
            skPoint(sketch, "E6.15.7.4", {"position": v(25.5, 39.4) * mm});
            skLineSegment(sketch, "E6.16.7.4", {"start": v(31, 36.8) * mm, "end": v(31, 33.34) * mm});
            skLineSegment(sketch, "E6.19.7.4", {"start": v(27, 43.73) * mm, "end": v(27, 40.27) * mm});
            skLineSegment(sketch, "E6.22.7.4", {"start": v(24, 45.46) * mm, "end": v(27, 43.73) * mm});
            skLineSegment(sketch, "E6.25.7.4", {"start": v(21, 43.73) * mm, "end": v(24, 45.46) * mm});
            skLineSegment(sketch, "E6.28.7.4", {"start": v(21, 40.27) * mm, "end": v(21, 43.73) * mm});
            skLineSegment(sketch, "E6.31.7.4", {"start": v(24, 38.54) * mm, "end": v(21, 40.27) * mm});
            skCircle(sketch, "E6.34.7.4", {"center": v(24, 42) * mm, "radius": 3 * mm, "construction": true});
            skLineSegment(sketch, "E6.36.7.4", {"start": v(31, 33.34) * mm, "end": v(28, 31.6) * mm});
            skLineSegment(sketch, "E6.39.7.4", {"start": v(27, 40.27) * mm, "end": v(24, 38.54) * mm});
            skCircle(sketch, "E6.0.7.5", {"center": v(28, 49.07) * mm, "radius": 3 * mm, "construction": true});
            skLineSegment(sketch, "E6.2.7.5", {"start": v(28, 45.6) * mm, "end": v(25, 47.34) * mm});
            skLineSegment(sketch, "E6.5.7.5", {"start": v(25, 47.34) * mm, "end": v(25, 50.8) * mm});
            skLineSegment(sketch, "E6.8.7.5", {"start": v(25, 50.8) * mm, "end": v(28, 52.54) * mm});
            skLineSegment(sketch, "E6.11.7.5", {"start": v(28, 52.54) * mm, "end": v(31, 50.8) * mm});
            skPoint(sketch, "E6.14.7.5", {"position": v(29.5, 46.47) * mm});
            skPoint(sketch, "E6.15.7.5", {"position": v(25.5, 53.4) * mm});
            skLineSegment(sketch, "E6.16.7.5", {"start": v(31, 50.8) * mm, "end": v(31, 47.34) * mm});
            skLineSegment(sketch, "E6.19.7.5", {"start": v(27, 57.73) * mm, "end": v(27, 54.27) * mm});
            skLineSegment(sketch, "E6.22.7.5", {"start": v(24, 59.46) * mm, "end": v(27, 57.73) * mm});
            skLineSegment(sketch, "E6.25.7.5", {"start": v(21, 57.73) * mm, "end": v(24, 59.46) * mm});
            skLineSegment(sketch, "E6.28.7.5", {"start": v(21, 54.27) * mm, "end": v(21, 57.73) * mm});
            skLineSegment(sketch, "E6.31.7.5", {"start": v(24, 52.54) * mm, "end": v(21, 54.27) * mm});
            skCircle(sketch, "E6.34.7.5", {"center": v(24, 56) * mm, "radius": 3 * mm, "construction": true});
            skLineSegment(sketch, "E6.36.7.5", {"start": v(31, 47.34) * mm, "end": v(28, 45.6) * mm});
            skLineSegment(sketch, "E6.39.7.5", {"start": v(27, 54.27) * mm, "end": v(24, 52.54) * mm});
            skCircle(sketch, "E6.0.8.4", {"center": v(36, 35.07) * mm, "radius": 3 * mm, "construction": true});
            skLineSegment(sketch, "E6.2.8.4", {"start": v(36, 31.6) * mm, "end": v(33, 33.34) * mm});
            skLineSegment(sketch, "E6.5.8.4", {"start": v(33, 33.34) * mm, "end": v(33, 36.8) * mm});
            skLineSegment(sketch, "E6.8.8.4", {"start": v(33, 36.8) * mm, "end": v(36, 38.54) * mm});
            skLineSegment(sketch, "E6.11.8.4", {"start": v(36, 38.54) * mm, "end": v(39, 36.8) * mm});
            skPoint(sketch, "E6.14.8.4", {"position": v(37.5, 32.47) * mm});
            skPoint(sketch, "E6.15.8.4", {"position": v(33.5, 39.4) * mm});
            skLineSegment(sketch, "E6.16.8.4", {"start": v(39, 36.8) * mm, "end": v(39, 33.34) * mm});
            skLineSegment(sketch, "E6.19.8.4", {"start": v(35, 43.73) * mm, "end": v(35, 40.27) * mm});
            skLineSegment(sketch, "E6.22.8.4", {"start": v(32, 45.46) * mm, "end": v(35, 43.73) * mm});
            skLineSegment(sketch, "E6.25.8.4", {"start": v(29, 43.73) * mm, "end": v(32, 45.46) * mm});
            skLineSegment(sketch, "E6.28.8.4", {"start": v(29, 40.27) * mm, "end": v(29, 43.73) * mm});
            skLineSegment(sketch, "E6.31.8.4", {"start": v(32, 38.54) * mm, "end": v(29, 40.27) * mm});
            skCircle(sketch, "E6.34.8.4", {"center": v(32, 42) * mm, "radius": 3 * mm, "construction": true});
            skLineSegment(sketch, "E6.36.8.4", {"start": v(39, 33.34) * mm, "end": v(36, 31.6) * mm});
            skLineSegment(sketch, "E6.39.8.4", {"start": v(35, 40.27) * mm, "end": v(32, 38.54) * mm});
            skCircle(sketch, "E6.0.8.5", {"center": v(36, 49.07) * mm, "radius": 3 * mm, "construction": true});
            skLineSegment(sketch, "E6.2.8.5", {"start": v(36, 45.6) * mm, "end": v(33, 47.34) * mm});
            skLineSegment(sketch, "E6.5.8.5", {"start": v(33, 47.34) * mm, "end": v(33, 50.8) * mm});
            skLineSegment(sketch, "E6.8.8.5", {"start": v(33, 50.8) * mm, "end": v(36, 52.54) * mm});
            skLineSegment(sketch, "E6.11.8.5", {"start": v(36, 52.54) * mm, "end": v(39, 50.8) * mm});
            skPoint(sketch, "E6.14.8.5", {"position": v(37.5, 46.47) * mm});
            skPoint(sketch, "E6.15.8.5", {"position": v(33.5, 53.4) * mm});
            skLineSegment(sketch, "E6.16.8.5", {"start": v(39, 50.8) * mm, "end": v(39, 47.34) * mm});
            skLineSegment(sketch, "E6.19.8.5", {"start": v(35, 57.73) * mm, "end": v(35, 54.27) * mm});
            skLineSegment(sketch, "E6.22.8.5", {"start": v(32, 59.46) * mm, "end": v(35, 57.73) * mm});
            skLineSegment(sketch, "E6.25.8.5", {"start": v(29, 57.73) * mm, "end": v(32, 59.46) * mm});
            skLineSegment(sketch, "E6.28.8.5", {"start": v(29, 54.27) * mm, "end": v(29, 57.73) * mm});
            skLineSegment(sketch, "E6.31.8.5", {"start": v(32, 52.54) * mm, "end": v(29, 54.27) * mm});
            skCircle(sketch, "E6.34.8.5", {"center": v(32, 56) * mm, "radius": 3 * mm, "construction": true});
            skLineSegment(sketch, "E6.36.8.5", {"start": v(39, 47.34) * mm, "end": v(36, 45.6) * mm});
            skLineSegment(sketch, "E6.39.8.5", {"start": v(35, 54.27) * mm, "end": v(32, 52.54) * mm});
            skCircle(sketch, "E6.0.9.4", {"center": v(44, 35.07) * mm, "radius": 3 * mm, "construction": true});
            skLineSegment(sketch, "E6.2.9.4", {"start": v(44, 31.6) * mm, "end": v(41, 33.34) * mm});
            skLineSegment(sketch, "E6.5.9.4", {"start": v(41, 33.34) * mm, "end": v(41, 36.8) * mm});
            skLineSegment(sketch, "E6.8.9.4", {"start": v(41, 36.8) * mm, "end": v(44, 38.54) * mm});
            skLineSegment(sketch, "E6.11.9.4", {"start": v(44, 38.54) * mm, "end": v(47, 36.8) * mm});
            skPoint(sketch, "E6.14.9.4", {"position": v(45.5, 32.47) * mm});
            skPoint(sketch, "E6.15.9.4", {"position": v(41.5, 39.4) * mm});
            skLineSegment(sketch, "E6.16.9.4", {"start": v(47, 36.8) * mm, "end": v(47, 33.34) * mm});
            skLineSegment(sketch, "E6.19.9.4", {"start": v(43, 43.73) * mm, "end": v(43, 40.27) * mm});
            skLineSegment(sketch, "E6.22.9.4", {"start": v(40, 45.46) * mm, "end": v(43, 43.73) * mm});
            skLineSegment(sketch, "E6.25.9.4", {"start": v(37, 43.73) * mm, "end": v(40, 45.46) * mm});
            skLineSegment(sketch, "E6.28.9.4", {"start": v(37, 40.27) * mm, "end": v(37, 43.73) * mm});
            skLineSegment(sketch, "E6.31.9.4", {"start": v(40, 38.54) * mm, "end": v(37, 40.27) * mm});
            skCircle(sketch, "E6.34.9.4", {"center": v(40, 42) * mm, "radius": 3 * mm, "construction": true});
            skLineSegment(sketch, "E6.36.9.4", {"start": v(47, 33.34) * mm, "end": v(44, 31.6) * mm});
            skLineSegment(sketch, "E6.39.9.4", {"start": v(43, 40.27) * mm, "end": v(40, 38.54) * mm});
            skCircle(sketch, "E6.0.9.5", {"center": v(44, 49.07) * mm, "radius": 3 * mm, "construction": true});
            skLineSegment(sketch, "E6.2.9.5", {"start": v(44, 45.6) * mm, "end": v(41, 47.34) * mm});
            skLineSegment(sketch, "E6.5.9.5", {"start": v(41, 47.34) * mm, "end": v(41, 50.8) * mm});
            skLineSegment(sketch, "E6.8.9.5", {"start": v(41, 50.8) * mm, "end": v(44, 52.54) * mm});
            skLineSegment(sketch, "E6.11.9.5", {"start": v(44, 52.54) * mm, "end": v(47, 50.8) * mm});
            skPoint(sketch, "E6.14.9.5", {"position": v(45.5, 46.47) * mm});
            skPoint(sketch, "E6.15.9.5", {"position": v(41.5, 53.4) * mm});
            skLineSegment(sketch, "E6.16.9.5", {"start": v(47, 50.8) * mm, "end": v(47, 47.34) * mm});
            skLineSegment(sketch, "E6.19.9.5", {"start": v(43, 57.73) * mm, "end": v(43, 54.27) * mm});
            skLineSegment(sketch, "E6.22.9.5", {"start": v(40, 59.46) * mm, "end": v(43, 57.73) * mm});
            skLineSegment(sketch, "E6.25.9.5", {"start": v(37, 57.73) * mm, "end": v(40, 59.46) * mm});
            skLineSegment(sketch, "E6.28.9.5", {"start": v(37, 54.27) * mm, "end": v(37, 57.73) * mm});
            skLineSegment(sketch, "E6.31.9.5", {"start": v(40, 52.54) * mm, "end": v(37, 54.27) * mm});
            skCircle(sketch, "E6.34.9.5", {"center": v(40, 56) * mm, "radius": 3 * mm, "construction": true});
            skLineSegment(sketch, "E6.36.9.5", {"start": v(47, 47.34) * mm, "end": v(44, 45.6) * mm});
            skLineSegment(sketch, "E6.39.9.5", {"start": v(43, 54.27) * mm, "end": v(40, 52.54) * mm});
            skCircle(sketch, "E6.0.10.4", {"center": v(52, 35.07) * mm, "radius": 3 * mm, "construction": true});
            skLineSegment(sketch, "E6.2.10.4", {"start": v(52, 31.6) * mm, "end": v(49, 33.34) * mm});
            skLineSegment(sketch, "E6.5.10.4", {"start": v(49, 33.34) * mm, "end": v(49, 36.8) * mm});
            skLineSegment(sketch, "E6.8.10.4", {"start": v(49, 36.8) * mm, "end": v(52, 38.54) * mm});
            skLineSegment(sketch, "E6.11.10.4", {"start": v(52, 38.54) * mm, "end": v(55, 36.8) * mm});
            skPoint(sketch, "E6.14.10.4", {"position": v(53.5, 32.47) * mm});
            skPoint(sketch, "E6.15.10.4", {"position": v(49.5, 39.4) * mm});
            skLineSegment(sketch, "E6.16.10.4", {"start": v(55, 36.8) * mm, "end": v(55, 33.34) * mm});
            skLineSegment(sketch, "E6.19.10.4", {"start": v(51, 43.73) * mm, "end": v(51, 40.27) * mm});
            skLineSegment(sketch, "E6.22.10.4", {"start": v(48, 45.46) * mm, "end": v(51, 43.73) * mm});
            skLineSegment(sketch, "E6.25.10.4", {"start": v(45, 43.73) * mm, "end": v(48, 45.46) * mm});
            skLineSegment(sketch, "E6.28.10.4", {"start": v(45, 40.27) * mm, "end": v(45, 43.73) * mm});
            skLineSegment(sketch, "E6.31.10.4", {"start": v(48, 38.54) * mm, "end": v(45, 40.27) * mm});
            skCircle(sketch, "E6.34.10.4", {"center": v(48, 42) * mm, "radius": 3 * mm, "construction": true});
            skLineSegment(sketch, "E6.36.10.4", {"start": v(55, 33.34) * mm, "end": v(52, 31.6) * mm});
            skLineSegment(sketch, "E6.39.10.4", {"start": v(51, 40.27) * mm, "end": v(48, 38.54) * mm});
            skCircle(sketch, "E6.0.10.5", {"center": v(52, 49.07) * mm, "radius": 3 * mm, "construction": true});
            skLineSegment(sketch, "E6.2.10.5", {"start": v(52, 45.6) * mm, "end": v(49, 47.34) * mm});
            skLineSegment(sketch, "E6.5.10.5", {"start": v(49, 47.34) * mm, "end": v(49, 50.8) * mm});
            skLineSegment(sketch, "E6.8.10.5", {"start": v(49, 50.8) * mm, "end": v(52, 52.54) * mm});
            skLineSegment(sketch, "E6.11.10.5", {"start": v(52, 52.54) * mm, "end": v(55, 50.8) * mm});
            skPoint(sketch, "E6.14.10.5", {"position": v(53.5, 46.47) * mm});
            skPoint(sketch, "E6.15.10.5", {"position": v(49.5, 53.4) * mm});
            skLineSegment(sketch, "E6.16.10.5", {"start": v(55, 50.8) * mm, "end": v(55, 47.34) * mm});
            skLineSegment(sketch, "E6.19.10.5", {"start": v(51, 57.73) * mm, "end": v(51, 54.27) * mm});
            skLineSegment(sketch, "E6.22.10.5", {"start": v(48, 59.46) * mm, "end": v(51, 57.73) * mm});
            skLineSegment(sketch, "E6.25.10.5", {"start": v(45, 57.73) * mm, "end": v(48, 59.46) * mm});
            skLineSegment(sketch, "E6.28.10.5", {"start": v(45, 54.27) * mm, "end": v(45, 57.73) * mm});
            skLineSegment(sketch, "E6.31.10.5", {"start": v(48, 52.54) * mm, "end": v(45, 54.27) * mm});
            skCircle(sketch, "E6.34.10.5", {"center": v(48, 56) * mm, "radius": 3 * mm, "construction": true});
            skLineSegment(sketch, "E6.36.10.5", {"start": v(55, 47.34) * mm, "end": v(52, 45.6) * mm});
            skLineSegment(sketch, "E6.39.10.5", {"start": v(51, 54.27) * mm, "end": v(48, 52.54) * mm});
            skLineSegment(sketch, "E7.bottom", {"start": v(-39.5, 62.1) * mm, "end": v(75.5, 62.1) * mm});
            skLineSegment(sketch, "E7.top", {"start": v(-39.5, -26.9) * mm, "end": v(75.5, -26.9) * mm});
            skLineSegment(sketch, "E7.left", {"start": v(-39.5, 62.1) * mm, "end": v(-39.5, -26.9) * mm});
            skLineSegment(sketch, "E7.right", {"start": v(75.5, 62.1) * mm, "end": v(75.5, -26.9) * mm});
            skCircle(sketch, "E8.0.11.0", {"center": v(60, -20.93) * mm, "radius": 3 * mm, "construction": true});
            skLineSegment(sketch, "E8.2.11.0", {"start": v(60, -24.4) * mm, "end": v(57, -22.66) * mm});
            skLineSegment(sketch, "E8.5.11.0", {"start": v(57, -22.66) * mm, "end": v(57, -19.2) * mm});
            skLineSegment(sketch, "E8.8.11.0", {"start": v(57, -19.2) * mm, "end": v(60, -17.46) * mm});
            skLineSegment(sketch, "E8.11.11.0", {"start": v(60, -17.46) * mm, "end": v(63, -19.2) * mm});
            skPoint(sketch, "E8.14.11.0", {"position": v(61.5, -23.53) * mm});
            skPoint(sketch, "E8.15.11.0", {"position": v(57.5, -16.6) * mm});
            skLineSegment(sketch, "E8.16.11.0", {"start": v(63, -19.2) * mm, "end": v(63, -22.66) * mm});
            skLineSegment(sketch, "E8.19.11.0", {"start": v(59, -12.27) * mm, "end": v(59, -15.73) * mm});
            skLineSegment(sketch, "E8.22.11.0", {"start": v(56, -10.54) * mm, "end": v(59, -12.27) * mm});
            skLineSegment(sketch, "E8.25.11.0", {"start": v(53, -12.27) * mm, "end": v(56, -10.54) * mm});
            skLineSegment(sketch, "E8.28.11.0", {"start": v(53, -15.73) * mm, "end": v(53, -12.27) * mm});
            skLineSegment(sketch, "E8.31.11.0", {"start": v(56, -17.46) * mm, "end": v(53, -15.73) * mm});
            skCircle(sketch, "E8.34.11.0", {"center": v(56, -14) * mm, "radius": 3 * mm, "construction": true});
            skLineSegment(sketch, "E8.36.11.0", {"start": v(63, -22.66) * mm, "end": v(60, -24.4) * mm});
            skLineSegment(sketch, "E8.39.11.0", {"start": v(59, -15.73) * mm, "end": v(56, -17.46) * mm});
            skCircle(sketch, "E8.0.11.1", {"center": v(60, -6.93) * mm, "radius": 3 * mm, "construction": true});
            skLineSegment(sketch, "E8.2.11.1", {"start": v(60, -10.4) * mm, "end": v(57, -8.66) * mm});
            skLineSegment(sketch, "E8.5.11.1", {"start": v(57, -8.66) * mm, "end": v(57, -5.2) * mm});
            skLineSegment(sketch, "E8.8.11.1", {"start": v(57, -5.2) * mm, "end": v(60, -3.46) * mm});
            skLineSegment(sketch, "E8.11.11.1", {"start": v(60, -3.46) * mm, "end": v(63, -5.2) * mm});
            skPoint(sketch, "E8.14.11.1", {"position": v(61.5, -9.53) * mm});
            skPoint(sketch, "E8.15.11.1", {"position": v(57.5, -2.6) * mm});
            skLineSegment(sketch, "E8.16.11.1", {"start": v(63, -5.2) * mm, "end": v(63, -8.66) * mm});
            skLineSegment(sketch, "E8.19.11.1", {"start": v(59, 1.73) * mm, "end": v(59, -1.73) * mm});
            skLineSegment(sketch, "E8.22.11.1", {"start": v(56, 3.46) * mm, "end": v(59, 1.73) * mm});
            skLineSegment(sketch, "E8.25.11.1", {"start": v(53, 1.73) * mm, "end": v(56, 3.46) * mm});
            skLineSegment(sketch, "E8.28.11.1", {"start": v(53, -1.73) * mm, "end": v(53, 1.73) * mm});
            skLineSegment(sketch, "E8.31.11.1", {"start": v(56, -3.46) * mm, "end": v(53, -1.73) * mm});
            skCircle(sketch, "E8.34.11.1", {"center": v(56, 0) * mm, "radius": 3 * mm, "construction": true});
            skLineSegment(sketch, "E8.36.11.1", {"start": v(63, -8.66) * mm, "end": v(60, -10.4) * mm});
            skLineSegment(sketch, "E8.39.11.1", {"start": v(59, -1.73) * mm, "end": v(56, -3.46) * mm});
            skCircle(sketch, "E8.0.11.2", {"center": v(60, 7.07) * mm, "radius": 3 * mm, "construction": true});
            skLineSegment(sketch, "E8.2.11.2", {"start": v(60, 3.6) * mm, "end": v(57, 5.34) * mm});
            skLineSegment(sketch, "E8.5.11.2", {"start": v(57, 5.34) * mm, "end": v(57, 8.8) * mm});
            skLineSegment(sketch, "E8.8.11.2", {"start": v(57, 8.8) * mm, "end": v(60, 10.54) * mm});
            skLineSegment(sketch, "E8.11.11.2", {"start": v(60, 10.54) * mm, "end": v(63, 8.8) * mm});
            skPoint(sketch, "E8.14.11.2", {"position": v(61.5, 4.47) * mm});
            skPoint(sketch, "E8.15.11.2", {"position": v(57.5, 11.4) * mm});
            skLineSegment(sketch, "E8.16.11.2", {"start": v(63, 8.8) * mm, "end": v(63, 5.34) * mm});
            skLineSegment(sketch, "E8.19.11.2", {"start": v(59, 15.73) * mm, "end": v(59, 12.27) * mm});
            skLineSegment(sketch, "E8.22.11.2", {"start": v(56, 17.46) * mm, "end": v(59, 15.73) * mm});
            skLineSegment(sketch, "E8.25.11.2", {"start": v(53, 15.73) * mm, "end": v(56, 17.46) * mm});
            skLineSegment(sketch, "E8.28.11.2", {"start": v(53, 12.27) * mm, "end": v(53, 15.73) * mm});
            skLineSegment(sketch, "E8.31.11.2", {"start": v(56, 10.54) * mm, "end": v(53, 12.27) * mm});
            skCircle(sketch, "E8.34.11.2", {"center": v(56, 14) * mm, "radius": 3 * mm, "construction": true});
            skLineSegment(sketch, "E8.36.11.2", {"start": v(63, 5.34) * mm, "end": v(60, 3.6) * mm});
            skLineSegment(sketch, "E8.39.11.2", {"start": v(59, 12.27) * mm, "end": v(56, 10.54) * mm});
            skCircle(sketch, "E8.0.11.3", {"center": v(60, 21.07) * mm, "radius": 3 * mm, "construction": true});
            skLineSegment(sketch, "E8.2.11.3", {"start": v(60, 17.6) * mm, "end": v(57, 19.34) * mm});
            skLineSegment(sketch, "E8.5.11.3", {"start": v(57, 19.34) * mm, "end": v(57, 22.8) * mm});
            skLineSegment(sketch, "E8.8.11.3", {"start": v(57, 22.8) * mm, "end": v(60, 24.54) * mm});
            skLineSegment(sketch, "E8.11.11.3", {"start": v(60, 24.54) * mm, "end": v(63, 22.8) * mm});
            skPoint(sketch, "E8.14.11.3", {"position": v(61.5, 18.47) * mm});
            skPoint(sketch, "E8.15.11.3", {"position": v(57.5, 25.4) * mm});
            skLineSegment(sketch, "E8.16.11.3", {"start": v(63, 22.8) * mm, "end": v(63, 19.34) * mm});
            skLineSegment(sketch, "E8.19.11.3", {"start": v(59, 29.73) * mm, "end": v(59, 26.27) * mm});
            skLineSegment(sketch, "E8.22.11.3", {"start": v(56, 31.46) * mm, "end": v(59, 29.73) * mm});
            skLineSegment(sketch, "E8.25.11.3", {"start": v(53, 29.73) * mm, "end": v(56, 31.46) * mm});
            skLineSegment(sketch, "E8.28.11.3", {"start": v(53, 26.27) * mm, "end": v(53, 29.73) * mm});
            skLineSegment(sketch, "E8.31.11.3", {"start": v(56, 24.54) * mm, "end": v(53, 26.27) * mm});
            skCircle(sketch, "E8.34.11.3", {"center": v(56, 28) * mm, "radius": 3 * mm, "construction": true});
            skLineSegment(sketch, "E8.36.11.3", {"start": v(63, 19.34) * mm, "end": v(60, 17.6) * mm});
            skLineSegment(sketch, "E8.39.11.3", {"start": v(59, 26.27) * mm, "end": v(56, 24.54) * mm});
            skCircle(sketch, "E8.0.11.4", {"center": v(60, 35.07) * mm, "radius": 3 * mm, "construction": true});
            skLineSegment(sketch, "E8.2.11.4", {"start": v(60, 31.6) * mm, "end": v(57, 33.34) * mm});
            skLineSegment(sketch, "E8.5.11.4", {"start": v(57, 33.34) * mm, "end": v(57, 36.8) * mm});
            skLineSegment(sketch, "E8.8.11.4", {"start": v(57, 36.8) * mm, "end": v(60, 38.54) * mm});
            skLineSegment(sketch, "E8.11.11.4", {"start": v(60, 38.54) * mm, "end": v(63, 36.8) * mm});
            skPoint(sketch, "E8.14.11.4", {"position": v(61.5, 32.47) * mm});
            skPoint(sketch, "E8.15.11.4", {"position": v(57.5, 39.4) * mm});
            skLineSegment(sketch, "E8.16.11.4", {"start": v(63, 36.8) * mm, "end": v(63, 33.34) * mm});
            skLineSegment(sketch, "E8.19.11.4", {"start": v(59, 43.73) * mm, "end": v(59, 40.27) * mm});
            skLineSegment(sketch, "E8.22.11.4", {"start": v(56, 45.46) * mm, "end": v(59, 43.73) * mm});
            skLineSegment(sketch, "E8.25.11.4", {"start": v(53, 43.73) * mm, "end": v(56, 45.46) * mm});
            skLineSegment(sketch, "E8.28.11.4", {"start": v(53, 40.27) * mm, "end": v(53, 43.73) * mm});
            skLineSegment(sketch, "E8.31.11.4", {"start": v(56, 38.54) * mm, "end": v(53, 40.27) * mm});
            skCircle(sketch, "E8.34.11.4", {"center": v(56, 42) * mm, "radius": 3 * mm, "construction": true});
            skLineSegment(sketch, "E8.36.11.4", {"start": v(63, 33.34) * mm, "end": v(60, 31.6) * mm});
            skLineSegment(sketch, "E8.39.11.4", {"start": v(59, 40.27) * mm, "end": v(56, 38.54) * mm});
            skCircle(sketch, "E8.0.11.5", {"center": v(60, 49.07) * mm, "radius": 3 * mm, "construction": true});
            skLineSegment(sketch, "E8.2.11.5", {"start": v(60, 45.6) * mm, "end": v(57, 47.34) * mm});
            skLineSegment(sketch, "E8.5.11.5", {"start": v(57, 47.34) * mm, "end": v(57, 50.8) * mm});
            skLineSegment(sketch, "E8.8.11.5", {"start": v(57, 50.8) * mm, "end": v(60, 52.54) * mm});
            skLineSegment(sketch, "E8.11.11.5", {"start": v(60, 52.54) * mm, "end": v(63, 50.8) * mm});
            skPoint(sketch, "E8.14.11.5", {"position": v(61.5, 46.47) * mm});
            skPoint(sketch, "E8.15.11.5", {"position": v(57.5, 53.4) * mm});
            skLineSegment(sketch, "E8.16.11.5", {"start": v(63, 50.8) * mm, "end": v(63, 47.34) * mm});
            skLineSegment(sketch, "E8.19.11.5", {"start": v(59, 57.73) * mm, "end": v(59, 54.27) * mm});
            skLineSegment(sketch, "E8.22.11.5", {"start": v(56, 59.46) * mm, "end": v(59, 57.73) * mm});
            skLineSegment(sketch, "E8.25.11.5", {"start": v(53, 57.73) * mm, "end": v(56, 59.46) * mm});
            skLineSegment(sketch, "E8.28.11.5", {"start": v(53, 54.27) * mm, "end": v(53, 57.73) * mm});
            skLineSegment(sketch, "E8.31.11.5", {"start": v(56, 52.54) * mm, "end": v(53, 54.27) * mm});
            skCircle(sketch, "E8.34.11.5", {"center": v(56, 56) * mm, "radius": 3 * mm, "construction": true});
            skLineSegment(sketch, "E8.36.11.5", {"start": v(63, 47.34) * mm, "end": v(60, 45.6) * mm});
            skLineSegment(sketch, "E8.39.11.5", {"start": v(59, 54.27) * mm, "end": v(56, 52.54) * mm});
            skCircle(sketch, "E9.0.12.0", {"center": v(68, -20.93) * mm, "radius": 3 * mm, "construction": true});
            skLineSegment(sketch, "E9.2.12.0", {"start": v(68, -24.4) * mm, "end": v(65, -22.66) * mm});
            skLineSegment(sketch, "E9.5.12.0", {"start": v(65, -22.66) * mm, "end": v(65, -19.2) * mm});
            skLineSegment(sketch, "E9.8.12.0", {"start": v(65, -19.2) * mm, "end": v(68, -17.46) * mm});
            skLineSegment(sketch, "E9.11.12.0", {"start": v(68, -17.46) * mm, "end": v(71, -19.2) * mm});
            skPoint(sketch, "E9.14.12.0", {"position": v(69.5, -23.53) * mm});
            skPoint(sketch, "E9.15.12.0", {"position": v(65.5, -16.6) * mm});
            skLineSegment(sketch, "E9.16.12.0", {"start": v(71, -19.2) * mm, "end": v(71, -22.66) * mm});
            skLineSegment(sketch, "E9.19.12.0", {"start": v(67, -12.27) * mm, "end": v(67, -15.73) * mm});
            skLineSegment(sketch, "E9.22.12.0", {"start": v(64, -10.54) * mm, "end": v(67, -12.27) * mm});
            skLineSegment(sketch, "E9.25.12.0", {"start": v(61, -12.27) * mm, "end": v(64, -10.54) * mm});
            skLineSegment(sketch, "E9.28.12.0", {"start": v(61, -15.73) * mm, "end": v(61, -12.27) * mm});
            skLineSegment(sketch, "E9.31.12.0", {"start": v(64, -17.46) * mm, "end": v(61, -15.73) * mm});
            skCircle(sketch, "E9.34.12.0", {"center": v(64, -14) * mm, "radius": 3 * mm, "construction": true});
            skLineSegment(sketch, "E9.36.12.0", {"start": v(71, -22.66) * mm, "end": v(68, -24.4) * mm});
            skLineSegment(sketch, "E9.39.12.0", {"start": v(67, -15.73) * mm, "end": v(64, -17.46) * mm});
            skCircle(sketch, "E9.0.12.1", {"center": v(68, -6.93) * mm, "radius": 3 * mm, "construction": true});
            skLineSegment(sketch, "E9.2.12.1", {"start": v(68, -10.4) * mm, "end": v(65, -8.66) * mm});
            skLineSegment(sketch, "E9.5.12.1", {"start": v(65, -8.66) * mm, "end": v(65, -5.2) * mm});
            skLineSegment(sketch, "E9.8.12.1", {"start": v(65, -5.2) * mm, "end": v(68, -3.46) * mm});
            skLineSegment(sketch, "E9.11.12.1", {"start": v(68, -3.46) * mm, "end": v(71, -5.2) * mm});
            skPoint(sketch, "E9.14.12.1", {"position": v(69.5, -9.53) * mm});
            skPoint(sketch, "E9.15.12.1", {"position": v(65.5, -2.6) * mm});
            skLineSegment(sketch, "E9.16.12.1", {"start": v(71, -5.2) * mm, "end": v(71, -8.66) * mm});
            skLineSegment(sketch, "E9.19.12.1", {"start": v(67, 1.73) * mm, "end": v(67, -1.73) * mm});
            skLineSegment(sketch, "E9.22.12.1", {"start": v(64, 3.46) * mm, "end": v(67, 1.73) * mm});
            skLineSegment(sketch, "E9.25.12.1", {"start": v(61, 1.73) * mm, "end": v(64, 3.46) * mm});
            skLineSegment(sketch, "E9.28.12.1", {"start": v(61, -1.73) * mm, "end": v(61, 1.73) * mm});
            skLineSegment(sketch, "E9.31.12.1", {"start": v(64, -3.46) * mm, "end": v(61, -1.73) * mm});
            skCircle(sketch, "E9.34.12.1", {"center": v(64, 0) * mm, "radius": 3 * mm, "construction": true});
            skLineSegment(sketch, "E9.36.12.1", {"start": v(71, -8.66) * mm, "end": v(68, -10.4) * mm});
            skLineSegment(sketch, "E9.39.12.1", {"start": v(67, -1.73) * mm, "end": v(64, -3.46) * mm});
            skCircle(sketch, "E9.0.12.2", {"center": v(68, 7.07) * mm, "radius": 3 * mm, "construction": true});
            skLineSegment(sketch, "E9.2.12.2", {"start": v(68, 3.6) * mm, "end": v(65, 5.34) * mm});
            skLineSegment(sketch, "E9.5.12.2", {"start": v(65, 5.34) * mm, "end": v(65, 8.8) * mm});
            skLineSegment(sketch, "E9.8.12.2", {"start": v(65, 8.8) * mm, "end": v(68, 10.54) * mm});
            skLineSegment(sketch, "E9.11.12.2", {"start": v(68, 10.54) * mm, "end": v(71, 8.8) * mm});
            skPoint(sketch, "E9.14.12.2", {"position": v(69.5, 4.47) * mm});
            skPoint(sketch, "E9.15.12.2", {"position": v(65.5, 11.4) * mm});
            skLineSegment(sketch, "E9.16.12.2", {"start": v(71, 8.8) * mm, "end": v(71, 5.34) * mm});
            skLineSegment(sketch, "E9.19.12.2", {"start": v(67, 15.73) * mm, "end": v(67, 12.27) * mm});
            skLineSegment(sketch, "E9.22.12.2", {"start": v(64, 17.46) * mm, "end": v(67, 15.73) * mm});
            skLineSegment(sketch, "E9.25.12.2", {"start": v(61, 15.73) * mm, "end": v(64, 17.46) * mm});
            skLineSegment(sketch, "E9.28.12.2", {"start": v(61, 12.27) * mm, "end": v(61, 15.73) * mm});
            skLineSegment(sketch, "E9.31.12.2", {"start": v(64, 10.54) * mm, "end": v(61, 12.27) * mm});
            skCircle(sketch, "E9.34.12.2", {"center": v(64, 14) * mm, "radius": 3 * mm, "construction": true});
            skLineSegment(sketch, "E9.36.12.2", {"start": v(71, 5.34) * mm, "end": v(68, 3.6) * mm});
            skLineSegment(sketch, "E9.39.12.2", {"start": v(67, 12.27) * mm, "end": v(64, 10.54) * mm});
            skCircle(sketch, "E9.0.12.3", {"center": v(68, 21.07) * mm, "radius": 3 * mm, "construction": true});
            skLineSegment(sketch, "E9.2.12.3", {"start": v(68, 17.6) * mm, "end": v(65, 19.34) * mm});
            skLineSegment(sketch, "E9.5.12.3", {"start": v(65, 19.34) * mm, "end": v(65, 22.8) * mm});
            skLineSegment(sketch, "E9.8.12.3", {"start": v(65, 22.8) * mm, "end": v(68, 24.54) * mm});
            skLineSegment(sketch, "E9.11.12.3", {"start": v(68, 24.54) * mm, "end": v(71, 22.8) * mm});
            skPoint(sketch, "E9.14.12.3", {"position": v(69.5, 18.47) * mm});
            skPoint(sketch, "E9.15.12.3", {"position": v(65.5, 25.4) * mm});
            skLineSegment(sketch, "E9.16.12.3", {"start": v(71, 22.8) * mm, "end": v(71, 19.34) * mm});
            skLineSegment(sketch, "E9.19.12.3", {"start": v(67, 29.73) * mm, "end": v(67, 26.27) * mm});
            skLineSegment(sketch, "E9.22.12.3", {"start": v(64, 31.46) * mm, "end": v(67, 29.73) * mm});
            skLineSegment(sketch, "E9.25.12.3", {"start": v(61, 29.73) * mm, "end": v(64, 31.46) * mm});
            skLineSegment(sketch, "E9.28.12.3", {"start": v(61, 26.27) * mm, "end": v(61, 29.73) * mm});
            skLineSegment(sketch, "E9.31.12.3", {"start": v(64, 24.54) * mm, "end": v(61, 26.27) * mm});
            skCircle(sketch, "E9.34.12.3", {"center": v(64, 28) * mm, "radius": 3 * mm, "construction": true});
            skLineSegment(sketch, "E9.36.12.3", {"start": v(71, 19.34) * mm, "end": v(68, 17.6) * mm});
            skLineSegment(sketch, "E9.39.12.3", {"start": v(67, 26.27) * mm, "end": v(64, 24.54) * mm});
            skCircle(sketch, "E9.0.12.4", {"center": v(68, 35.07) * mm, "radius": 3 * mm, "construction": true});
            skLineSegment(sketch, "E9.2.12.4", {"start": v(68, 31.6) * mm, "end": v(65, 33.34) * mm});
            skLineSegment(sketch, "E9.5.12.4", {"start": v(65, 33.34) * mm, "end": v(65, 36.8) * mm});
            skLineSegment(sketch, "E9.8.12.4", {"start": v(65, 36.8) * mm, "end": v(68, 38.54) * mm});
            skLineSegment(sketch, "E9.11.12.4", {"start": v(68, 38.54) * mm, "end": v(71, 36.8) * mm});
            skPoint(sketch, "E9.14.12.4", {"position": v(69.5, 32.47) * mm});
            skPoint(sketch, "E9.15.12.4", {"position": v(65.5, 39.4) * mm});
            skLineSegment(sketch, "E9.16.12.4", {"start": v(71, 36.8) * mm, "end": v(71, 33.34) * mm});
            skLineSegment(sketch, "E9.19.12.4", {"start": v(67, 43.73) * mm, "end": v(67, 40.27) * mm});
            skLineSegment(sketch, "E9.22.12.4", {"start": v(64, 45.46) * mm, "end": v(67, 43.73) * mm});
            skLineSegment(sketch, "E9.25.12.4", {"start": v(61, 43.73) * mm, "end": v(64, 45.46) * mm});
            skLineSegment(sketch, "E9.28.12.4", {"start": v(61, 40.27) * mm, "end": v(61, 43.73) * mm});
            skLineSegment(sketch, "E9.31.12.4", {"start": v(64, 38.54) * mm, "end": v(61, 40.27) * mm});
            skCircle(sketch, "E9.34.12.4", {"center": v(64, 42) * mm, "radius": 3 * mm, "construction": true});
            skLineSegment(sketch, "E9.36.12.4", {"start": v(71, 33.34) * mm, "end": v(68, 31.6) * mm});
            skLineSegment(sketch, "E9.39.12.4", {"start": v(67, 40.27) * mm, "end": v(64, 38.54) * mm});
            skCircle(sketch, "E9.0.12.5", {"center": v(68, 49.07) * mm, "radius": 3 * mm, "construction": true});
            skLineSegment(sketch, "E9.2.12.5", {"start": v(68, 45.6) * mm, "end": v(65, 47.34) * mm});
            skLineSegment(sketch, "E9.5.12.5", {"start": v(65, 47.34) * mm, "end": v(65, 50.8) * mm});
            skLineSegment(sketch, "E9.8.12.5", {"start": v(65, 50.8) * mm, "end": v(68, 52.54) * mm});
            skLineSegment(sketch, "E9.11.12.5", {"start": v(68, 52.54) * mm, "end": v(71, 50.8) * mm});
            skPoint(sketch, "E9.14.12.5", {"position": v(69.5, 46.47) * mm});
            skPoint(sketch, "E9.15.12.5", {"position": v(65.5, 53.4) * mm});
            skLineSegment(sketch, "E9.16.12.5", {"start": v(71, 50.8) * mm, "end": v(71, 47.34) * mm});
            skLineSegment(sketch, "E9.19.12.5", {"start": v(67, 57.73) * mm, "end": v(67, 54.27) * mm});
            skLineSegment(sketch, "E9.22.12.5", {"start": v(64, 59.46) * mm, "end": v(67, 57.73) * mm});
            skLineSegment(sketch, "E9.25.12.5", {"start": v(61, 57.73) * mm, "end": v(64, 59.46) * mm});
            skLineSegment(sketch, "E9.28.12.5", {"start": v(61, 54.27) * mm, "end": v(61, 57.73) * mm});
            skLineSegment(sketch, "E9.31.12.5", {"start": v(64, 52.54) * mm, "end": v(61, 54.27) * mm});
            skCircle(sketch, "E9.34.12.5", {"center": v(64, 56) * mm, "radius": 3 * mm, "construction": true});
            skLineSegment(sketch, "E9.36.12.5", {"start": v(71, 47.34) * mm, "end": v(68, 45.6) * mm});
            skLineSegment(sketch, "E9.39.12.5", {"start": v(67, 54.27) * mm, "end": v(64, 52.54) * mm});
            skSolve(sketch);
        }
        {
            var Q0;
            Q0=makeQuery(id+"F0.imprint","IMPRINT",FACE,{"disambiguationData":[TD([[makeQuery(id+"F0.imprint","IMPRINT",EDGE,{"derivedFrom":sQuery(id+"F0.wireOp",EDGE,"E0.0")}),1.0]])]});
            extrude(context, id + "F1", {"entities" : qUnion([Q0]), "oppositeDirection" : true, "depth" : 1.5 * mm});
        }
        {
            var Q0;
            Q0=makeQuery(id+"F0.imprint","IMPRINT",FACE,{"disambiguationData":[TD([[makeQuery(id+"F0.imprint","IMPRINT",EDGE,{"derivedFrom":sQuery(id+"F0.wireOp",EDGE,"E3.bottom")}),1.0]])]});
            extrude(context, id + "F2", {"entities" : qUnion([Q0]), "operationType" : NewBodyOperationType.ADD, "oppositeDirection" : true, "depth" : 28 * mm});
        }
        {
            var Q0;
            Q0=makeQuery(id+"F2.opExtrude","SWEPT_FACE",FACE,{"disambiguationData":[OSD([sQuery(id+"F0.wireOp",EDGE,"E7.top")])]});
            var sketch = newSketch(context, id + "F3", { "sketchPlane" : qUnion([Q0])});
            skCircle(sketch, "E10.cCircle", {"center": v(-33.75, -14.2) * mm, "radius": 3 * mm, "construction": true});
            skLineSegment(sketch, "E10.0", {"start": v(-30.75, -15.94) * mm, "end": v(-33.75, -17.67) * mm});
            skLineSegment(sketch, "E10.1", {"start": v(-33.75, -17.67) * mm, "end": v(-36.75, -15.94) * mm});
            skLineSegment(sketch, "E10.2", {"start": v(-36.75, -15.94) * mm, "end": v(-36.75, -12.47) * mm});
            skLineSegment(sketch, "E10.3", {"start": v(-36.75, -12.47) * mm, "end": v(-33.75, -10.74) * mm});
            skLineSegment(sketch, "E10.4", {"start": v(-33.75, -10.74) * mm, "end": v(-30.75, -12.47) * mm});
            skLineSegment(sketch, "E10.5", {"start": v(-30.75, -12.47) * mm, "end": v(-30.75, -15.94) * mm});
            skPoint(sketch, "E10.0.midPoint", {"position": v(-32.25, -16.8) * mm});
            skCircle(sketch, "E11.cCircle", {"center": v(-29.25, -22) * mm, "radius": 3 * mm, "construction": true});
            skLineSegment(sketch, "E11.0", {"start": v(-26.25, -23.73) * mm, "end": v(-29.25, -25.46) * mm});
            skLineSegment(sketch, "E11.1", {"start": v(-29.25, -25.46) * mm, "end": v(-32.25, -23.73) * mm});
            skLineSegment(sketch, "E11.2", {"start": v(-32.25, -23.73) * mm, "end": v(-32.25, -20.27) * mm});
            skLineSegment(sketch, "E11.3", {"start": v(-32.25, -20.27) * mm, "end": v(-29.25, -18.54) * mm});
            skLineSegment(sketch, "E11.4", {"start": v(-29.25, -18.54) * mm, "end": v(-26.25, -20.27) * mm});
            skLineSegment(sketch, "E11.5", {"start": v(-26.25, -20.27) * mm, "end": v(-26.25, -23.73) * mm});
            skPoint(sketch, "E11.0.midPoint", {"position": v(-27.75, -24.6) * mm});
            skPoint(sketch, "E12.0.1.0", {"position": v(-27.75, -8.95) * mm});
            skLineSegment(sketch, "E12.0.1.3", {"start": v(-26.25, -4.62) * mm, "end": v(-26.25, -8.08) * mm});
            skCircle(sketch, "E12.0.1.4", {"center": v(-29.25, -6.35) * mm, "radius": 3 * mm, "construction": true});
            skLineSegment(sketch, "E12.0.1.5", {"start": v(-32.25, -4.62) * mm, "end": v(-29.25, -2.89) * mm});
            skLineSegment(sketch, "E12.0.1.6", {"start": v(-32.25, -8.08) * mm, "end": v(-32.25, -4.62) * mm});
            skLineSegment(sketch, "E12.0.1.7", {"start": v(-26.25, -8.08) * mm, "end": v(-29.25, -9.81) * mm});
            skLineSegment(sketch, "E12.0.1.9", {"start": v(-29.25, -2.89) * mm, "end": v(-26.25, -4.62) * mm});
            skLineSegment(sketch, "E12.0.1.10", {"start": v(-29.25, -9.81) * mm, "end": v(-32.25, -8.08) * mm});
            skPoint(sketch, "E12.1.0.0", {"position": v(-18.75, -24.6) * mm});
            skPoint(sketch, "E12.1.0.1", {"position": v(-23.25, -16.8) * mm});
            skCircle(sketch, "E12.1.0.2", {"center": v(-24.75, -14.2) * mm, "radius": 3 * mm, "construction": true});
            skLineSegment(sketch, "E12.1.0.3", {"start": v(-17.25, -20.27) * mm, "end": v(-17.25, -23.73) * mm});
            skCircle(sketch, "E12.1.0.4", {"center": v(-20.25, -22) * mm, "radius": 3 * mm, "construction": true});
            skLineSegment(sketch, "E12.1.0.5", {"start": v(-23.25, -20.27) * mm, "end": v(-20.25, -18.54) * mm});
            skLineSegment(sketch, "E12.1.0.6", {"start": v(-23.25, -23.73) * mm, "end": v(-23.25, -20.27) * mm});
            skLineSegment(sketch, "E12.1.0.7", {"start": v(-17.25, -23.73) * mm, "end": v(-20.25, -25.46) * mm});
            skLineSegment(sketch, "E12.1.0.8", {"start": v(-21.75, -12.47) * mm, "end": v(-21.75, -15.94) * mm});
            skLineSegment(sketch, "E12.1.0.9", {"start": v(-20.25, -18.54) * mm, "end": v(-17.25, -20.27) * mm});
            skLineSegment(sketch, "E12.1.0.10", {"start": v(-20.25, -25.46) * mm, "end": v(-23.25, -23.73) * mm});
            skLineSegment(sketch, "E12.1.0.11", {"start": v(-27.75, -15.94) * mm, "end": v(-27.75, -12.47) * mm});
            skLineSegment(sketch, "E12.1.0.12", {"start": v(-27.75, -12.47) * mm, "end": v(-24.75, -10.74) * mm});
            skLineSegment(sketch, "E12.1.0.13", {"start": v(-24.75, -10.74) * mm, "end": v(-21.75, -12.47) * mm});
            skLineSegment(sketch, "E12.1.0.14", {"start": v(-21.75, -15.94) * mm, "end": v(-24.75, -17.67) * mm});
            skLineSegment(sketch, "E12.1.0.15", {"start": v(-24.75, -17.67) * mm, "end": v(-27.75, -15.94) * mm});
            skPoint(sketch, "E12.1.1.0", {"position": v(-18.75, -8.95) * mm});
            skLineSegment(sketch, "E12.1.1.3", {"start": v(-17.25, -4.62) * mm, "end": v(-17.25, -8.08) * mm});
            skCircle(sketch, "E12.1.1.4", {"center": v(-20.25, -6.35) * mm, "radius": 3 * mm, "construction": true});
            skLineSegment(sketch, "E12.1.1.5", {"start": v(-23.25, -4.62) * mm, "end": v(-20.25, -2.89) * mm});
            skLineSegment(sketch, "E12.1.1.6", {"start": v(-23.25, -8.08) * mm, "end": v(-23.25, -4.62) * mm});
            skLineSegment(sketch, "E12.1.1.7", {"start": v(-17.25, -8.08) * mm, "end": v(-20.25, -9.81) * mm});
            skLineSegment(sketch, "E12.1.1.9", {"start": v(-20.25, -2.89) * mm, "end": v(-17.25, -4.62) * mm});
            skLineSegment(sketch, "E12.1.1.10", {"start": v(-20.25, -9.81) * mm, "end": v(-23.25, -8.08) * mm});
            skPoint(sketch, "E12.2.0.0", {"position": v(-9.75, -24.6) * mm});
            skPoint(sketch, "E12.2.0.1", {"position": v(-14.25, -16.8) * mm});
            skCircle(sketch, "E12.2.0.2", {"center": v(-15.75, -14.2) * mm, "radius": 3 * mm, "construction": true});
            skLineSegment(sketch, "E12.2.0.3", {"start": v(-8.25, -20.27) * mm, "end": v(-8.25, -23.73) * mm});
            skCircle(sketch, "E12.2.0.4", {"center": v(-11.25, -22) * mm, "radius": 3 * mm, "construction": true});
            skLineSegment(sketch, "E12.2.0.5", {"start": v(-14.25, -20.27) * mm, "end": v(-11.25, -18.54) * mm});
            skLineSegment(sketch, "E12.2.0.6", {"start": v(-14.25, -23.73) * mm, "end": v(-14.25, -20.27) * mm});
            skLineSegment(sketch, "E12.2.0.7", {"start": v(-8.25, -23.73) * mm, "end": v(-11.25, -25.46) * mm});
            skLineSegment(sketch, "E12.2.0.8", {"start": v(-12.75, -12.47) * mm, "end": v(-12.75, -15.94) * mm});
            skLineSegment(sketch, "E12.2.0.9", {"start": v(-11.25, -18.54) * mm, "end": v(-8.25, -20.27) * mm});
            skLineSegment(sketch, "E12.2.0.10", {"start": v(-11.25, -25.46) * mm, "end": v(-14.25, -23.73) * mm});
            skLineSegment(sketch, "E12.2.0.11", {"start": v(-18.75, -15.94) * mm, "end": v(-18.75, -12.47) * mm});
            skLineSegment(sketch, "E12.2.0.12", {"start": v(-18.75, -12.47) * mm, "end": v(-15.75, -10.74) * mm});
            skLineSegment(sketch, "E12.2.0.13", {"start": v(-15.75, -10.74) * mm, "end": v(-12.75, -12.47) * mm});
            skLineSegment(sketch, "E12.2.0.14", {"start": v(-12.75, -15.94) * mm, "end": v(-15.75, -17.67) * mm});
            skLineSegment(sketch, "E12.2.0.15", {"start": v(-15.75, -17.67) * mm, "end": v(-18.75, -15.94) * mm});
            skPoint(sketch, "E12.2.1.0", {"position": v(-9.75, -8.95) * mm});
            skLineSegment(sketch, "E12.2.1.3", {"start": v(-8.25, -4.62) * mm, "end": v(-8.25, -8.08) * mm});
            skCircle(sketch, "E12.2.1.4", {"center": v(-11.25, -6.35) * mm, "radius": 3 * mm, "construction": true});
            skLineSegment(sketch, "E12.2.1.5", {"start": v(-14.25, -4.62) * mm, "end": v(-11.25, -2.89) * mm});
            skLineSegment(sketch, "E12.2.1.6", {"start": v(-14.25, -8.08) * mm, "end": v(-14.25, -4.62) * mm});
            skLineSegment(sketch, "E12.2.1.7", {"start": v(-8.25, -8.08) * mm, "end": v(-11.25, -9.81) * mm});
            skLineSegment(sketch, "E12.2.1.9", {"start": v(-11.25, -2.89) * mm, "end": v(-8.25, -4.62) * mm});
            skLineSegment(sketch, "E12.2.1.10", {"start": v(-11.25, -9.81) * mm, "end": v(-14.25, -8.08) * mm});
            skLineSegment(sketch, "E12.direction1", {"start": v(-32.25, -23.73) * mm, "end": v(-23.25, -23.73) * mm, "construction": true});
            skLineSegment(sketch, "E12.direction2", {"start": v(-32.25, -23.73) * mm, "end": v(-32.25, -8.08) * mm, "construction": true});
            skPoint(sketch, "E13.0.3.0", {"position": v(-0.75, -24.6) * mm});
            skPoint(sketch, "E13.1.3.0", {"position": v(-5.25, -16.8) * mm});
            skCircle(sketch, "E13.2.3.0", {"center": v(-6.75, -14.2) * mm, "radius": 3 * mm, "construction": true});
            skLineSegment(sketch, "E13.4.3.0", {"start": v(0.75, -20.27) * mm, "end": v(0.75, -23.73) * mm});
            skCircle(sketch, "E13.7.3.0", {"center": v(-2.25, -22) * mm, "radius": 3 * mm, "construction": true});
            skLineSegment(sketch, "E13.9.3.0", {"start": v(-5.25, -20.27) * mm, "end": v(-2.25, -18.54) * mm});
            skLineSegment(sketch, "E13.12.3.0", {"start": v(-5.25, -23.73) * mm, "end": v(-5.25, -20.27) * mm});
            skLineSegment(sketch, "E13.15.3.0", {"start": v(0.75, -23.73) * mm, "end": v(-2.25, -25.46) * mm});
            skLineSegment(sketch, "E13.18.3.0", {"start": v(-3.75, -12.47) * mm, "end": v(-3.75, -15.94) * mm});
            skLineSegment(sketch, "E13.21.3.0", {"start": v(-2.25, -18.54) * mm, "end": v(0.75, -20.27) * mm});
            skLineSegment(sketch, "E13.24.3.0", {"start": v(-2.25, -25.46) * mm, "end": v(-5.25, -23.73) * mm});
            skLineSegment(sketch, "E13.27.3.0", {"start": v(-9.75, -15.94) * mm, "end": v(-9.75, -12.47) * mm});
            skLineSegment(sketch, "E13.30.3.0", {"start": v(-9.75, -12.47) * mm, "end": v(-6.75, -10.74) * mm});
            skLineSegment(sketch, "E13.33.3.0", {"start": v(-6.75, -10.74) * mm, "end": v(-3.75, -12.47) * mm});
            skLineSegment(sketch, "E13.36.3.0", {"start": v(-3.75, -15.94) * mm, "end": v(-6.75, -17.67) * mm});
            skLineSegment(sketch, "E13.39.3.0", {"start": v(-6.75, -17.67) * mm, "end": v(-9.75, -15.94) * mm});
            skPoint(sketch, "E13.0.3.1", {"position": v(-0.75, -8.95) * mm});
            skLineSegment(sketch, "E13.4.3.1", {"start": v(0.75, -4.62) * mm, "end": v(0.75, -8.08) * mm});
            skCircle(sketch, "E13.7.3.1", {"center": v(-2.25, -6.35) * mm, "radius": 3 * mm, "construction": true});
            skLineSegment(sketch, "E13.9.3.1", {"start": v(-5.25, -4.62) * mm, "end": v(-2.25, -2.89) * mm});
            skLineSegment(sketch, "E13.12.3.1", {"start": v(-5.25, -8.08) * mm, "end": v(-5.25, -4.62) * mm});
            skLineSegment(sketch, "E13.15.3.1", {"start": v(0.75, -8.08) * mm, "end": v(-2.25, -9.81) * mm});
            skLineSegment(sketch, "E13.21.3.1", {"start": v(-2.25, -2.89) * mm, "end": v(0.75, -4.62) * mm});
            skLineSegment(sketch, "E13.24.3.1", {"start": v(-2.25, -9.81) * mm, "end": v(-5.25, -8.08) * mm});
            skPoint(sketch, "E13.0.4.0", {"position": v(8.25, -24.6) * mm});
            skPoint(sketch, "E13.1.4.0", {"position": v(3.75, -16.8) * mm});
            skCircle(sketch, "E13.2.4.0", {"center": v(2.25, -14.2) * mm, "radius": 3 * mm, "construction": true});
            skLineSegment(sketch, "E13.4.4.0", {"start": v(9.75, -20.27) * mm, "end": v(9.75, -23.73) * mm});
            skCircle(sketch, "E13.7.4.0", {"center": v(6.75, -22) * mm, "radius": 3 * mm, "construction": true});
            skLineSegment(sketch, "E13.9.4.0", {"start": v(3.75, -20.27) * mm, "end": v(6.75, -18.54) * mm});
            skLineSegment(sketch, "E13.12.4.0", {"start": v(3.75, -23.73) * mm, "end": v(3.75, -20.27) * mm});
            skLineSegment(sketch, "E13.15.4.0", {"start": v(9.75, -23.73) * mm, "end": v(6.75, -25.46) * mm});
            skLineSegment(sketch, "E13.18.4.0", {"start": v(5.25, -12.47) * mm, "end": v(5.25, -15.94) * mm});
            skLineSegment(sketch, "E13.21.4.0", {"start": v(6.75, -18.54) * mm, "end": v(9.75, -20.27) * mm});
            skLineSegment(sketch, "E13.24.4.0", {"start": v(6.75, -25.46) * mm, "end": v(3.75, -23.73) * mm});
            skLineSegment(sketch, "E13.27.4.0", {"start": v(-0.75, -15.94) * mm, "end": v(-0.75, -12.47) * mm});
            skLineSegment(sketch, "E13.30.4.0", {"start": v(-0.75, -12.47) * mm, "end": v(2.25, -10.74) * mm});
            skLineSegment(sketch, "E13.33.4.0", {"start": v(2.25, -10.74) * mm, "end": v(5.25, -12.47) * mm});
            skLineSegment(sketch, "E13.36.4.0", {"start": v(5.25, -15.94) * mm, "end": v(2.25, -17.67) * mm});
            skLineSegment(sketch, "E13.39.4.0", {"start": v(2.25, -17.67) * mm, "end": v(-0.75, -15.94) * mm});
            skPoint(sketch, "E13.0.4.1", {"position": v(8.25, -8.95) * mm});
            skLineSegment(sketch, "E13.4.4.1", {"start": v(9.75, -4.62) * mm, "end": v(9.75, -8.08) * mm});
            skCircle(sketch, "E13.7.4.1", {"center": v(6.75, -6.35) * mm, "radius": 3 * mm, "construction": true});
            skLineSegment(sketch, "E13.9.4.1", {"start": v(3.75, -4.62) * mm, "end": v(6.75, -2.89) * mm});
            skLineSegment(sketch, "E13.12.4.1", {"start": v(3.75, -8.08) * mm, "end": v(3.75, -4.62) * mm});
            skLineSegment(sketch, "E13.15.4.1", {"start": v(9.75, -8.08) * mm, "end": v(6.75, -9.81) * mm});
            skLineSegment(sketch, "E13.21.4.1", {"start": v(6.75, -2.89) * mm, "end": v(9.75, -4.62) * mm});
            skLineSegment(sketch, "E13.24.4.1", {"start": v(6.75, -9.81) * mm, "end": v(3.75, -8.08) * mm});
            skPoint(sketch, "E13.0.5.0", {"position": v(17.25, -24.6) * mm});
            skPoint(sketch, "E13.1.5.0", {"position": v(12.75, -16.8) * mm});
            skCircle(sketch, "E13.2.5.0", {"center": v(11.25, -14.2) * mm, "radius": 3 * mm, "construction": true});
            skLineSegment(sketch, "E13.4.5.0", {"start": v(18.75, -20.27) * mm, "end": v(18.75, -23.73) * mm});
            skCircle(sketch, "E13.7.5.0", {"center": v(15.75, -22) * mm, "radius": 3 * mm, "construction": true});
            skLineSegment(sketch, "E13.9.5.0", {"start": v(12.75, -20.27) * mm, "end": v(15.75, -18.54) * mm});
            skLineSegment(sketch, "E13.12.5.0", {"start": v(12.75, -23.73) * mm, "end": v(12.75, -20.27) * mm});
            skLineSegment(sketch, "E13.15.5.0", {"start": v(18.75, -23.73) * mm, "end": v(15.75, -25.46) * mm});
            skLineSegment(sketch, "E13.18.5.0", {"start": v(14.25, -12.47) * mm, "end": v(14.25, -15.94) * mm});
            skLineSegment(sketch, "E13.21.5.0", {"start": v(15.75, -18.54) * mm, "end": v(18.75, -20.27) * mm});
            skLineSegment(sketch, "E13.24.5.0", {"start": v(15.75, -25.46) * mm, "end": v(12.75, -23.73) * mm});
            skLineSegment(sketch, "E13.27.5.0", {"start": v(8.25, -15.94) * mm, "end": v(8.25, -12.47) * mm});
            skLineSegment(sketch, "E13.30.5.0", {"start": v(8.25, -12.47) * mm, "end": v(11.25, -10.74) * mm});
            skLineSegment(sketch, "E13.33.5.0", {"start": v(11.25, -10.74) * mm, "end": v(14.25, -12.47) * mm});
            skLineSegment(sketch, "E13.36.5.0", {"start": v(14.25, -15.94) * mm, "end": v(11.25, -17.67) * mm});
            skLineSegment(sketch, "E13.39.5.0", {"start": v(11.25, -17.67) * mm, "end": v(8.25, -15.94) * mm});
            skPoint(sketch, "E13.0.5.1", {"position": v(17.25, -8.95) * mm});
            skLineSegment(sketch, "E13.4.5.1", {"start": v(18.75, -4.62) * mm, "end": v(18.75, -8.08) * mm});
            skCircle(sketch, "E13.7.5.1", {"center": v(15.75, -6.35) * mm, "radius": 3 * mm, "construction": true});
            skLineSegment(sketch, "E13.9.5.1", {"start": v(12.75, -4.62) * mm, "end": v(15.75, -2.89) * mm});
            skLineSegment(sketch, "E13.12.5.1", {"start": v(12.75, -8.08) * mm, "end": v(12.75, -4.62) * mm});
            skLineSegment(sketch, "E13.15.5.1", {"start": v(18.75, -8.08) * mm, "end": v(15.75, -9.81) * mm});
            skLineSegment(sketch, "E13.21.5.1", {"start": v(15.75, -2.89) * mm, "end": v(18.75, -4.62) * mm});
            skLineSegment(sketch, "E13.24.5.1", {"start": v(15.75, -9.81) * mm, "end": v(12.75, -8.08) * mm});
            skPoint(sketch, "E13.0.6.0", {"position": v(26.25, -24.6) * mm});
            skPoint(sketch, "E13.1.6.0", {"position": v(21.75, -16.8) * mm});
            skCircle(sketch, "E13.2.6.0", {"center": v(20.25, -14.2) * mm, "radius": 3 * mm, "construction": true});
            skLineSegment(sketch, "E13.4.6.0", {"start": v(27.75, -20.27) * mm, "end": v(27.75, -23.73) * mm});
            skCircle(sketch, "E13.7.6.0", {"center": v(24.75, -22) * mm, "radius": 3 * mm, "construction": true});
            skLineSegment(sketch, "E13.9.6.0", {"start": v(21.75, -20.27) * mm, "end": v(24.75, -18.54) * mm});
            skLineSegment(sketch, "E13.12.6.0", {"start": v(21.75, -23.73) * mm, "end": v(21.75, -20.27) * mm});
            skLineSegment(sketch, "E13.15.6.0", {"start": v(27.75, -23.73) * mm, "end": v(24.75, -25.46) * mm});
            skLineSegment(sketch, "E13.18.6.0", {"start": v(23.25, -12.47) * mm, "end": v(23.25, -15.94) * mm});
            skLineSegment(sketch, "E13.21.6.0", {"start": v(24.75, -18.54) * mm, "end": v(27.75, -20.27) * mm});
            skLineSegment(sketch, "E13.24.6.0", {"start": v(24.75, -25.46) * mm, "end": v(21.75, -23.73) * mm});
            skLineSegment(sketch, "E13.27.6.0", {"start": v(17.25, -15.94) * mm, "end": v(17.25, -12.47) * mm});
            skLineSegment(sketch, "E13.30.6.0", {"start": v(17.25, -12.47) * mm, "end": v(20.25, -10.74) * mm});
            skLineSegment(sketch, "E13.33.6.0", {"start": v(20.25, -10.74) * mm, "end": v(23.25, -12.47) * mm});
            skLineSegment(sketch, "E13.36.6.0", {"start": v(23.25, -15.94) * mm, "end": v(20.25, -17.67) * mm});
            skLineSegment(sketch, "E13.39.6.0", {"start": v(20.25, -17.67) * mm, "end": v(17.25, -15.94) * mm});
            skPoint(sketch, "E13.0.6.1", {"position": v(26.25, -8.95) * mm});
            skLineSegment(sketch, "E13.4.6.1", {"start": v(27.75, -4.62) * mm, "end": v(27.75, -8.08) * mm});
            skCircle(sketch, "E13.7.6.1", {"center": v(24.75, -6.35) * mm, "radius": 3 * mm, "construction": true});
            skLineSegment(sketch, "E13.9.6.1", {"start": v(21.75, -4.62) * mm, "end": v(24.75, -2.89) * mm});
            skLineSegment(sketch, "E13.12.6.1", {"start": v(21.75, -8.08) * mm, "end": v(21.75, -4.62) * mm});
            skLineSegment(sketch, "E13.15.6.1", {"start": v(27.75, -8.08) * mm, "end": v(24.75, -9.81) * mm});
            skLineSegment(sketch, "E13.21.6.1", {"start": v(24.75, -2.89) * mm, "end": v(27.75, -4.62) * mm});
            skLineSegment(sketch, "E13.24.6.1", {"start": v(24.75, -9.81) * mm, "end": v(21.75, -8.08) * mm});
            skPoint(sketch, "E13.0.7.0", {"position": v(35.25, -24.6) * mm});
            skPoint(sketch, "E13.1.7.0", {"position": v(30.75, -16.8) * mm});
            skCircle(sketch, "E13.2.7.0", {"center": v(29.25, -14.2) * mm, "radius": 3 * mm, "construction": true});
            skLineSegment(sketch, "E13.4.7.0", {"start": v(36.75, -20.27) * mm, "end": v(36.75, -23.73) * mm});
            skCircle(sketch, "E13.7.7.0", {"center": v(33.75, -22) * mm, "radius": 3 * mm, "construction": true});
            skLineSegment(sketch, "E13.9.7.0", {"start": v(30.75, -20.27) * mm, "end": v(33.75, -18.54) * mm});
            skLineSegment(sketch, "E13.12.7.0", {"start": v(30.75, -23.73) * mm, "end": v(30.75, -20.27) * mm});
            skLineSegment(sketch, "E13.15.7.0", {"start": v(36.75, -23.73) * mm, "end": v(33.75, -25.46) * mm});
            skLineSegment(sketch, "E13.18.7.0", {"start": v(32.25, -12.47) * mm, "end": v(32.25, -15.94) * mm});
            skLineSegment(sketch, "E13.21.7.0", {"start": v(33.75, -18.54) * mm, "end": v(36.75, -20.27) * mm});
            skLineSegment(sketch, "E13.24.7.0", {"start": v(33.75, -25.46) * mm, "end": v(30.75, -23.73) * mm});
            skLineSegment(sketch, "E13.27.7.0", {"start": v(26.25, -15.94) * mm, "end": v(26.25, -12.47) * mm});
            skLineSegment(sketch, "E13.30.7.0", {"start": v(26.25, -12.47) * mm, "end": v(29.25, -10.74) * mm});
            skLineSegment(sketch, "E13.33.7.0", {"start": v(29.25, -10.74) * mm, "end": v(32.25, -12.47) * mm});
            skLineSegment(sketch, "E13.36.7.0", {"start": v(32.25, -15.94) * mm, "end": v(29.25, -17.67) * mm});
            skLineSegment(sketch, "E13.39.7.0", {"start": v(29.25, -17.67) * mm, "end": v(26.25, -15.94) * mm});
            skPoint(sketch, "E13.0.7.1", {"position": v(35.25, -8.95) * mm});
            skLineSegment(sketch, "E13.4.7.1", {"start": v(36.75, -4.62) * mm, "end": v(36.75, -8.08) * mm});
            skCircle(sketch, "E13.7.7.1", {"center": v(33.75, -6.35) * mm, "radius": 3 * mm, "construction": true});
            skLineSegment(sketch, "E13.9.7.1", {"start": v(30.75, -4.62) * mm, "end": v(33.75, -2.89) * mm});
            skLineSegment(sketch, "E13.12.7.1", {"start": v(30.75, -8.08) * mm, "end": v(30.75, -4.62) * mm});
            skLineSegment(sketch, "E13.15.7.1", {"start": v(36.75, -8.08) * mm, "end": v(33.75, -9.81) * mm});
            skLineSegment(sketch, "E13.21.7.1", {"start": v(33.75, -2.89) * mm, "end": v(36.75, -4.62) * mm});
            skLineSegment(sketch, "E13.24.7.1", {"start": v(33.75, -9.81) * mm, "end": v(30.75, -8.08) * mm});
            skPoint(sketch, "E13.0.8.0", {"position": v(44.25, -24.6) * mm});
            skPoint(sketch, "E13.1.8.0", {"position": v(39.75, -16.8) * mm});
            skCircle(sketch, "E13.2.8.0", {"center": v(38.25, -14.2) * mm, "radius": 3 * mm, "construction": true});
            skLineSegment(sketch, "E13.4.8.0", {"start": v(45.75, -20.27) * mm, "end": v(45.75, -23.73) * mm});
            skCircle(sketch, "E13.7.8.0", {"center": v(42.75, -22) * mm, "radius": 3 * mm, "construction": true});
            skLineSegment(sketch, "E13.9.8.0", {"start": v(39.75, -20.27) * mm, "end": v(42.75, -18.54) * mm});
            skLineSegment(sketch, "E13.12.8.0", {"start": v(39.75, -23.73) * mm, "end": v(39.75, -20.27) * mm});
            skLineSegment(sketch, "E13.15.8.0", {"start": v(45.75, -23.73) * mm, "end": v(42.75, -25.46) * mm});
            skLineSegment(sketch, "E13.18.8.0", {"start": v(41.25, -12.47) * mm, "end": v(41.25, -15.94) * mm});
            skLineSegment(sketch, "E13.21.8.0", {"start": v(42.75, -18.54) * mm, "end": v(45.75, -20.27) * mm});
            skLineSegment(sketch, "E13.24.8.0", {"start": v(42.75, -25.46) * mm, "end": v(39.75, -23.73) * mm});
            skLineSegment(sketch, "E13.27.8.0", {"start": v(35.25, -15.94) * mm, "end": v(35.25, -12.47) * mm});
            skLineSegment(sketch, "E13.30.8.0", {"start": v(35.25, -12.47) * mm, "end": v(38.25, -10.74) * mm});
            skLineSegment(sketch, "E13.33.8.0", {"start": v(38.25, -10.74) * mm, "end": v(41.25, -12.47) * mm});
            skLineSegment(sketch, "E13.36.8.0", {"start": v(41.25, -15.94) * mm, "end": v(38.25, -17.67) * mm});
            skLineSegment(sketch, "E13.39.8.0", {"start": v(38.25, -17.67) * mm, "end": v(35.25, -15.94) * mm});
            skPoint(sketch, "E13.0.8.1", {"position": v(44.25, -8.95) * mm});
            skLineSegment(sketch, "E13.4.8.1", {"start": v(45.75, -4.62) * mm, "end": v(45.75, -8.08) * mm});
            skCircle(sketch, "E13.7.8.1", {"center": v(42.75, -6.35) * mm, "radius": 3 * mm, "construction": true});
            skLineSegment(sketch, "E13.9.8.1", {"start": v(39.75, -4.62) * mm, "end": v(42.75, -2.89) * mm});
            skLineSegment(sketch, "E13.12.8.1", {"start": v(39.75, -8.08) * mm, "end": v(39.75, -4.62) * mm});
            skLineSegment(sketch, "E13.15.8.1", {"start": v(45.75, -8.08) * mm, "end": v(42.75, -9.81) * mm});
            skLineSegment(sketch, "E13.21.8.1", {"start": v(42.75, -2.89) * mm, "end": v(45.75, -4.62) * mm});
            skLineSegment(sketch, "E13.24.8.1", {"start": v(42.75, -9.81) * mm, "end": v(39.75, -8.08) * mm});
            skPoint(sketch, "E13.0.9.0", {"position": v(53.25, -24.6) * mm});
            skPoint(sketch, "E13.1.9.0", {"position": v(48.75, -16.8) * mm});
            skCircle(sketch, "E13.2.9.0", {"center": v(47.25, -14.2) * mm, "radius": 3 * mm, "construction": true});
            skLineSegment(sketch, "E13.4.9.0", {"start": v(54.75, -20.27) * mm, "end": v(54.75, -23.73) * mm});
            skCircle(sketch, "E13.7.9.0", {"center": v(51.75, -22) * mm, "radius": 3 * mm, "construction": true});
            skLineSegment(sketch, "E13.9.9.0", {"start": v(48.75, -20.27) * mm, "end": v(51.75, -18.54) * mm});
            skLineSegment(sketch, "E13.12.9.0", {"start": v(48.75, -23.73) * mm, "end": v(48.75, -20.27) * mm});
            skLineSegment(sketch, "E13.15.9.0", {"start": v(54.75, -23.73) * mm, "end": v(51.75, -25.46) * mm});
            skLineSegment(sketch, "E13.18.9.0", {"start": v(50.25, -12.47) * mm, "end": v(50.25, -15.94) * mm});
            skLineSegment(sketch, "E13.21.9.0", {"start": v(51.75, -18.54) * mm, "end": v(54.75, -20.27) * mm});
            skLineSegment(sketch, "E13.24.9.0", {"start": v(51.75, -25.46) * mm, "end": v(48.75, -23.73) * mm});
            skLineSegment(sketch, "E13.27.9.0", {"start": v(44.25, -15.94) * mm, "end": v(44.25, -12.47) * mm});
            skLineSegment(sketch, "E13.30.9.0", {"start": v(44.25, -12.47) * mm, "end": v(47.25, -10.74) * mm});
            skLineSegment(sketch, "E13.33.9.0", {"start": v(47.25, -10.74) * mm, "end": v(50.25, -12.47) * mm});
            skLineSegment(sketch, "E13.36.9.0", {"start": v(50.25, -15.94) * mm, "end": v(47.25, -17.67) * mm});
            skLineSegment(sketch, "E13.39.9.0", {"start": v(47.25, -17.67) * mm, "end": v(44.25, -15.94) * mm});
            skPoint(sketch, "E13.0.9.1", {"position": v(53.25, -8.95) * mm});
            skLineSegment(sketch, "E13.4.9.1", {"start": v(54.75, -4.62) * mm, "end": v(54.75, -8.08) * mm});
            skCircle(sketch, "E13.7.9.1", {"center": v(51.75, -6.35) * mm, "radius": 3 * mm, "construction": true});
            skLineSegment(sketch, "E13.9.9.1", {"start": v(48.75, -4.62) * mm, "end": v(51.75, -2.89) * mm});
            skLineSegment(sketch, "E13.12.9.1", {"start": v(48.75, -8.08) * mm, "end": v(48.75, -4.62) * mm});
            skLineSegment(sketch, "E13.15.9.1", {"start": v(54.75, -8.08) * mm, "end": v(51.75, -9.81) * mm});
            skLineSegment(sketch, "E13.21.9.1", {"start": v(51.75, -2.89) * mm, "end": v(54.75, -4.62) * mm});
            skLineSegment(sketch, "E13.24.9.1", {"start": v(51.75, -9.81) * mm, "end": v(48.75, -8.08) * mm});
            skPoint(sketch, "E13.0.10.0", {"position": v(62.25, -24.6) * mm});
            skPoint(sketch, "E13.1.10.0", {"position": v(57.75, -16.8) * mm});
            skCircle(sketch, "E13.2.10.0", {"center": v(56.25, -14.2) * mm, "radius": 3 * mm, "construction": true});
            skLineSegment(sketch, "E13.4.10.0", {"start": v(63.75, -20.27) * mm, "end": v(63.75, -23.73) * mm});
            skCircle(sketch, "E13.7.10.0", {"center": v(60.75, -22) * mm, "radius": 3 * mm, "construction": true});
            skLineSegment(sketch, "E13.9.10.0", {"start": v(57.75, -20.27) * mm, "end": v(60.75, -18.54) * mm});
            skLineSegment(sketch, "E13.12.10.0", {"start": v(57.75, -23.73) * mm, "end": v(57.75, -20.27) * mm});
            skLineSegment(sketch, "E13.15.10.0", {"start": v(63.75, -23.73) * mm, "end": v(60.75, -25.46) * mm});
            skLineSegment(sketch, "E13.18.10.0", {"start": v(59.25, -12.47) * mm, "end": v(59.25, -15.94) * mm});
            skLineSegment(sketch, "E13.21.10.0", {"start": v(60.75, -18.54) * mm, "end": v(63.75, -20.27) * mm});
            skLineSegment(sketch, "E13.24.10.0", {"start": v(60.75, -25.46) * mm, "end": v(57.75, -23.73) * mm});
            skLineSegment(sketch, "E13.27.10.0", {"start": v(53.25, -15.94) * mm, "end": v(53.25, -12.47) * mm});
            skLineSegment(sketch, "E13.30.10.0", {"start": v(53.25, -12.47) * mm, "end": v(56.25, -10.74) * mm});
            skLineSegment(sketch, "E13.33.10.0", {"start": v(56.25, -10.74) * mm, "end": v(59.25, -12.47) * mm});
            skLineSegment(sketch, "E13.36.10.0", {"start": v(59.25, -15.94) * mm, "end": v(56.25, -17.67) * mm});
            skLineSegment(sketch, "E13.39.10.0", {"start": v(56.25, -17.67) * mm, "end": v(53.25, -15.94) * mm});
            skPoint(sketch, "E13.0.10.1", {"position": v(62.25, -8.95) * mm});
            skLineSegment(sketch, "E13.4.10.1", {"start": v(63.75, -4.62) * mm, "end": v(63.75, -8.08) * mm});
            skCircle(sketch, "E13.7.10.1", {"center": v(60.75, -6.35) * mm, "radius": 3 * mm, "construction": true});
            skLineSegment(sketch, "E13.9.10.1", {"start": v(57.75, -4.62) * mm, "end": v(60.75, -2.89) * mm});
            skLineSegment(sketch, "E13.12.10.1", {"start": v(57.75, -8.08) * mm, "end": v(57.75, -4.62) * mm});
            skLineSegment(sketch, "E13.15.10.1", {"start": v(63.75, -8.08) * mm, "end": v(60.75, -9.81) * mm});
            skLineSegment(sketch, "E13.21.10.1", {"start": v(60.75, -2.89) * mm, "end": v(63.75, -4.62) * mm});
            skLineSegment(sketch, "E13.24.10.1", {"start": v(60.75, -9.81) * mm, "end": v(57.75, -8.08) * mm});
            skPoint(sketch, "E13.0.11.0", {"position": v(71.25, -24.6) * mm});
            skPoint(sketch, "E13.1.11.0", {"position": v(66.75, -16.8) * mm});
            skCircle(sketch, "E13.2.11.0", {"center": v(65.25, -14.2) * mm, "radius": 3 * mm, "construction": true});
            skLineSegment(sketch, "E13.4.11.0", {"start": v(72.75, -20.27) * mm, "end": v(72.75, -23.73) * mm});
            skCircle(sketch, "E13.7.11.0", {"center": v(69.75, -22) * mm, "radius": 3 * mm, "construction": true});
            skLineSegment(sketch, "E13.9.11.0", {"start": v(66.75, -20.27) * mm, "end": v(69.75, -18.54) * mm});
            skLineSegment(sketch, "E13.12.11.0", {"start": v(66.75, -23.73) * mm, "end": v(66.75, -20.27) * mm});
            skLineSegment(sketch, "E13.15.11.0", {"start": v(72.75, -23.73) * mm, "end": v(69.75, -25.46) * mm});
            skLineSegment(sketch, "E13.18.11.0", {"start": v(68.25, -12.47) * mm, "end": v(68.25, -15.94) * mm});
            skLineSegment(sketch, "E13.21.11.0", {"start": v(69.75, -18.54) * mm, "end": v(72.75, -20.27) * mm});
            skLineSegment(sketch, "E13.24.11.0", {"start": v(69.75, -25.46) * mm, "end": v(66.75, -23.73) * mm});
            skLineSegment(sketch, "E13.27.11.0", {"start": v(62.25, -15.94) * mm, "end": v(62.25, -12.47) * mm});
            skLineSegment(sketch, "E13.30.11.0", {"start": v(62.25, -12.47) * mm, "end": v(65.25, -10.74) * mm});
            skLineSegment(sketch, "E13.33.11.0", {"start": v(65.25, -10.74) * mm, "end": v(68.25, -12.47) * mm});
            skLineSegment(sketch, "E13.36.11.0", {"start": v(68.25, -15.94) * mm, "end": v(65.25, -17.67) * mm});
            skLineSegment(sketch, "E13.39.11.0", {"start": v(65.25, -17.67) * mm, "end": v(62.25, -15.94) * mm});
            skPoint(sketch, "E13.0.11.1", {"position": v(71.25, -8.95) * mm});
            skLineSegment(sketch, "E13.4.11.1", {"start": v(72.75, -4.62) * mm, "end": v(72.75, -8.08) * mm});
            skCircle(sketch, "E13.7.11.1", {"center": v(69.75, -6.35) * mm, "radius": 3 * mm, "construction": true});
            skLineSegment(sketch, "E13.9.11.1", {"start": v(66.75, -4.62) * mm, "end": v(69.75, -2.89) * mm});
            skLineSegment(sketch, "E13.12.11.1", {"start": v(66.75, -8.08) * mm, "end": v(66.75, -4.62) * mm});
            skLineSegment(sketch, "E13.15.11.1", {"start": v(72.75, -8.08) * mm, "end": v(69.75, -9.81) * mm});
            skLineSegment(sketch, "E13.21.11.1", {"start": v(69.75, -2.89) * mm, "end": v(72.75, -4.62) * mm});
            skLineSegment(sketch, "E13.24.11.1", {"start": v(69.75, -9.81) * mm, "end": v(66.75, -8.08) * mm});
            skSolve(sketch);
        }
        {
            var Q0;
            Q0=makeQuery(id+"F3.imprint","IMPRINT",FACE,{"disambiguationData":[TD([[makeQuery(id+"F3.imprint","IMPRINT",EDGE,{"derivedFrom":sQuery(id+"F3.wireOp",EDGE,"E10.0")}),1.0]])]});
            extrude(context, id + "F4", {"entities" : qUnion([Q0]), "operationType" : NewBodyOperationType.INTERSECT, "oppositeDirection" : true, "depth" : 100 * mm});
        }
        {
            var Q0;
            Q0=makeQuery(id+"F2.opExtrude","CAP_FACE",FACE,{"disambiguationData":[OSD([sQuery(id+"F0.wireOp",EDGE,"E3.bottom"),sQuery(id+"F0.wireOp",EDGE,"E3.top"),sQuery(id+"F0.wireOp",EDGE,"E3.left"),sQuery(id+"F0.wireOp",EDGE,"E3.right"),sQuery(id+"F0.wireOp",EDGE,"E7.bottom"),sQuery(id+"F0.wireOp",EDGE,"E7.top"),sQuery(id+"F0.wireOp",EDGE,"E7.left"),sQuery(id+"F0.wireOp",EDGE,"E7.right")])],"isStart":false});
            var sketch = newSketch(context, id + "F5", { "sketchPlane" : qUnion([Q0])});
            skCircle(sketch, "E14", {"center": v(-33, 19.4) * mm, "radius": 1.5 * mm});
            skCircle(sketch, "E15", {"center": v(69, 19.4) * mm, "radius": 1.5 * mm});
            skCircle(sketch, "E16", {"center": v(-33, -47.6) * mm, "radius": 1.5 * mm});
            skCircle(sketch, "E17", {"center": v(-33, -47.6) * mm, "radius": 4 * mm});
            skLineSegment(sketch, "E18", {"start": v(-33, -43.6) * mm, "end": v(-38, -43.6) * mm});
            skLineSegment(sketch, "E19", {"start": v(-33, -51.6) * mm, "end": v(-38, -51.6) * mm});
            skCircle(sketch, "E20", {"center": v(69, -47.6) * mm, "radius": 1.5 * mm});
            skCircle(sketch, "E21", {"center": v(69, -47.6) * mm, "radius": 4 * mm});
            skLineSegment(sketch, "E22", {"start": v(69, -43.6) * mm, "end": v(74, -43.6) * mm});
            skLineSegment(sketch, "E23", {"start": v(69, -51.6) * mm, "end": v(74, -51.6) * mm});
            skArc(sketch, "E24", {"start": v(61, 25.4) * mm, "mid": v(64.8, 16.2) * mm, "end": v(74, 12.4) * mm});
            skArc(sketch, "E25", {"start": v(-38, 12.4) * mm, "mid": v(-28.8, 16.2) * mm, "end": v(-25, 25.4) * mm});
            skSolve(sketch);
        }
        {
            var Q0;
            Q0=makeQuery(id+"F5.imprint","IMPRINT",FACE,{"disambiguationData":[TD([[makeQuery(id+"F5.imprint","IMPRINT",EDGE,{"derivedFrom":sQuery(id+"F5.wireOp",EDGE,"E14")}),-1.0]])]});
            var Q1;
            Q1=makeQuery(id+"F5.imprint","IMPRINT",FACE,{"disambiguationData":[TD([[makeQuery(id+"F5.imprint","IMPRINT",EDGE,{"derivedFrom":sQuery(id+"F5.wireOp",EDGE,"E15")}),-1.0]])]});
            var Q2;
            {var subQ0=sQuery(id+"F5.wireOp",EDGE,"E22");Q2=makeQuery(id+"F5.imprint","IMPRINT",FACE,{"disambiguationData":[TD([[makeQuery(id+"F5.imprint","IMPRINT",EDGE,{"derivedFrom":subQ0}),-1.0]])]});}
            var Q3;
            Q3=makeQuery(id+"F5.imprint","IMPRINT",FACE,{"disambiguationData":[TD([[makeQuery(id+"F5.imprint","IMPRINT",EDGE,{"derivedFrom":sQuery(id+"F5.wireOp",EDGE,"E20")}),-1.0]])]});
            var Q4;
            {var subQ0=sQuery(id+"F5.wireOp",EDGE,"E18");Q4=makeQuery(id+"F5.imprint","IMPRINT",FACE,{"disambiguationData":[TD([[makeQuery(id+"F5.imprint","IMPRINT",EDGE,{"derivedFrom":subQ0}),1.0]])]});}
            var Q5;
            Q5=makeQuery(id+"F5.imprint","IMPRINT",FACE,{"disambiguationData":[TD([[makeQuery(id+"F5.imprint","IMPRINT",EDGE,{"derivedFrom":sQuery(id+"F5.wireOp",EDGE,"E16")}),-1.0]])]});
            extrude(context, id + "F6", {"entities" : qUnion([Q0, Q1, Q2, Q3, Q4, Q5]), "operationType" : NewBodyOperationType.ADD, "oppositeDirection" : true, "depth" : 2 * mm});
        }
        {
            var Q0;
            Q0=makeQuery(id+"F1.opExtrude","CAP_EDGE",EDGE,{"disambiguationData":[OSD([sQuery(id+"F0.wireOp",EDGE,"E3.left")])],"isStart":false});
            var Q1;
            Q1=makeQuery(id+"F1.opExtrude","CAP_EDGE",EDGE,{"disambiguationData":[OSD([sQuery(id+"F0.wireOp",EDGE,"E3.bottom")])],"isStart":false});
            var Q2;
            Q2=makeQuery(id+"F2.opExtrude","SWEPT_EDGE",EDGE,{"disambiguationData":[OSD([sQuery(id+"F0.wireOp",EDGE,"E3.bottom"),sQuery(id+"F0.wireOp",EDGE,"E3.left")])]});
            var Q3;
            Q3=makeQuery(id+"F2.opExtrude","SWEPT_EDGE",EDGE,{"disambiguationData":[OSD([sQuery(id+"F0.wireOp",EDGE,"E3.bottom"),sQuery(id+"F0.wireOp",EDGE,"E3.right")])]});
            var Q4;
            Q4=makeQuery(id+"F1.opExtrude","CAP_EDGE",EDGE,{"disambiguationData":[OSD([sQuery(id+"F0.wireOp",EDGE,"E3.right")])],"isStart":false});
            var Q5;
            Q5=makeQuery(id+"F2.opExtrude","SWEPT_EDGE",EDGE,{"disambiguationData":[OSD([sQuery(id+"F0.wireOp",EDGE,"E3.top"),sQuery(id+"F0.wireOp",EDGE,"E3.right")])]});
            var Q6;
            Q6=makeQuery(id+"F1.opExtrude","CAP_EDGE",EDGE,{"disambiguationData":[OSD([sQuery(id+"F0.wireOp",EDGE,"E3.top")])],"isStart":false});
            var Q7;
            Q7=makeQuery(id+"F2.opExtrude","SWEPT_EDGE",EDGE,{"disambiguationData":[OSD([sQuery(id+"F0.wireOp",EDGE,"E3.top"),sQuery(id+"F0.wireOp",EDGE,"E3.left")])]});
            var Q8;
            Q8=makeQuery(id+"F2.opExtrude","SWEPT_EDGE",EDGE,{"disambiguationData":[OSD([sQuery(id+"F0.wireOp",EDGE,"E7.bottom"),sQuery(id+"F0.wireOp",EDGE,"E7.left")])]});
            var Q9;
            Q9=makeQuery(id+"F2.opExtrude","CAP_EDGE",EDGE,{"disambiguationData":[OSD([sQuery(id+"F0.wireOp",EDGE,"E7.left")])],"isStart":true});
            var Q10;
            Q10=makeQuery(id+"F2.opExtrude","SWEPT_EDGE",EDGE,{"disambiguationData":[OSD([sQuery(id+"F0.wireOp",EDGE,"E7.top"),sQuery(id+"F0.wireOp",EDGE,"E7.right")])]});
            var Q11;
            Q11=makeQuery(id+"F2.opExtrude","CAP_EDGE",EDGE,{"disambiguationData":[OSD([sQuery(id+"F0.wireOp",EDGE,"E7.right")])],"isStart":true});
            var Q12;
            Q12=makeQuery(id+"F2.opExtrude","SWEPT_EDGE",EDGE,{"disambiguationData":[OSD([sQuery(id+"F0.wireOp",EDGE,"E7.top"),sQuery(id+"F0.wireOp",EDGE,"E7.left")])]});
            var Q13;
            Q13=makeQuery(id+"F2.opExtrude","CAP_EDGE",EDGE,{"disambiguationData":[OSD([sQuery(id+"F0.wireOp",EDGE,"E7.bottom")])],"isStart":true});
            var Q14;
            Q14=makeQuery(id+"F2.opExtrude","SWEPT_EDGE",EDGE,{"disambiguationData":[OSD([sQuery(id+"F0.wireOp",EDGE,"E7.bottom"),sQuery(id+"F0.wireOp",EDGE,"E7.right")])]});
            var Q15;
            Q15=makeQuery(id+"F2.opExtrude","CAP_EDGE",EDGE,{"disambiguationData":[OSD([sQuery(id+"F0.wireOp",EDGE,"E7.top")])],"isStart":true});
            var Q16;
            {var subQ0=sQuery(id+"F0.wireOp",EDGE,"E3.left");var subQ1=makeQuery(id+"F2.opExtrude","CAP_EDGE",EDGE,{"disambiguationData":[OSD([subQ0])],"isStart":false});Q16=makeQuery(id+"F6.opExtrude","CAP_EDGE",EDGE,{"disambiguationData":[OSD([subQ0]),TDD([makeQuery(id+"F5.imprint","IMPRINT",EDGE,{"disambiguationData":[TD([[makeQuery(id+"F5.imprint","INTERSECT",VERTEX,{"derivedFrom":[subQ1,sQuery(id+"F5.wireOp",EDGE,"E18")]}),1.0]])],"derivedFrom":subQ1})])],"isStart":false});}
            var Q17;
            {var subQ0=sQuery(id+"F0.wireOp",EDGE,"E3.left");var subQ1=makeQuery(id+"F2.opExtrude","CAP_EDGE",EDGE,{"disambiguationData":[OSD([subQ0])],"isStart":false});Q17=makeQuery(id+"F6.opExtrude","CAP_EDGE",EDGE,{"disambiguationData":[OSD([subQ0]),TDD([makeQuery(id+"F5.imprint","IMPRINT",EDGE,{"disambiguationData":[TD([[makeQuery(id+"F5.imprint","INTERSECT",VERTEX,{"derivedFrom":[makeQuery(id+"F2.opExtrude","CAP_EDGE",EDGE,{"disambiguationData":[OSD([sQuery(id+"F0.wireOp",EDGE,"E3.top")])],"isStart":false}),subQ1]}),1.0]])],"derivedFrom":subQ1})])],"isStart":false});}
            var Q18;
            {var subQ0=sQuery(id+"F0.wireOp",EDGE,"E3.top");var subQ1=makeQuery(id+"F2.opExtrude","CAP_EDGE",EDGE,{"disambiguationData":[OSD([subQ0])],"isStart":false});Q18=makeQuery(id+"F6.opExtrude","CAP_EDGE",EDGE,{"disambiguationData":[OSD([subQ0]),TDD([makeQuery(id+"F5.imprint","IMPRINT",EDGE,{"disambiguationData":[TD([[makeQuery(id+"F5.imprint","INTERSECT",VERTEX,{"derivedFrom":[subQ1,makeQuery(id+"F2.opExtrude","CAP_EDGE",EDGE,{"disambiguationData":[OSD([sQuery(id+"F0.wireOp",EDGE,"E3.left")])],"isStart":false})]}),-1.0]])],"derivedFrom":subQ1})])],"isStart":false});}
            var Q19;
            {var subQ0=sQuery(id+"F0.wireOp",EDGE,"E3.right");var subQ1=makeQuery(id+"F2.opExtrude","CAP_EDGE",EDGE,{"disambiguationData":[OSD([subQ0])],"isStart":false});Q19=makeQuery(id+"F6.opExtrude","CAP_EDGE",EDGE,{"disambiguationData":[OSD([subQ0]),TDD([makeQuery(id+"F5.imprint","IMPRINT",EDGE,{"disambiguationData":[TD([[makeQuery(id+"F5.imprint","INTERSECT",VERTEX,{"derivedFrom":[subQ1,sQuery(id+"F5.wireOp",EDGE,"E22")]}),1.0]])],"derivedFrom":subQ1})])],"isStart":false});}
            var Q20;
            {var subQ0=sQuery(id+"F0.wireOp",EDGE,"E3.right");var subQ1=makeQuery(id+"F2.opExtrude","CAP_EDGE",EDGE,{"disambiguationData":[OSD([subQ0])],"isStart":false});Q20=makeQuery(id+"F6.opExtrude","CAP_EDGE",EDGE,{"disambiguationData":[OSD([subQ0]),TDD([makeQuery(id+"F5.imprint","IMPRINT",EDGE,{"disambiguationData":[TD([[makeQuery(id+"F5.imprint","INTERSECT",VERTEX,{"derivedFrom":[makeQuery(id+"F2.opExtrude","CAP_EDGE",EDGE,{"disambiguationData":[OSD([sQuery(id+"F0.wireOp",EDGE,"E3.top")])],"isStart":false}),subQ1]}),1.0]])],"derivedFrom":subQ1})])],"isStart":false});}
            var Q21;
            {var subQ0=sQuery(id+"F0.wireOp",EDGE,"E3.top");var subQ1=makeQuery(id+"F2.opExtrude","CAP_EDGE",EDGE,{"disambiguationData":[OSD([subQ0])],"isStart":false});Q21=makeQuery(id+"F6.opExtrude","CAP_EDGE",EDGE,{"disambiguationData":[OSD([subQ0]),TDD([makeQuery(id+"F5.imprint","IMPRINT",EDGE,{"disambiguationData":[TD([[makeQuery(id+"F5.imprint","INTERSECT",VERTEX,{"derivedFrom":[subQ1,makeQuery(id+"F2.opExtrude","CAP_EDGE",EDGE,{"disambiguationData":[OSD([sQuery(id+"F0.wireOp",EDGE,"E3.right")])],"isStart":false})]}),1.0]])],"derivedFrom":subQ1})])],"isStart":false});}
            fillet(context, id + "F7", {"entities" : qUnion([Q0, Q1, Q2, Q3, Q4, Q5, Q6, Q7, Q8, Q9, Q10, Q11, Q12, Q13, Q14, Q15, Q16, Q17, Q18, Q19, Q20, Q21]), "radius" : 1 * mm, "tangentPropagation" : true, "allowEdgeOverflow" : false});
        }
    });
